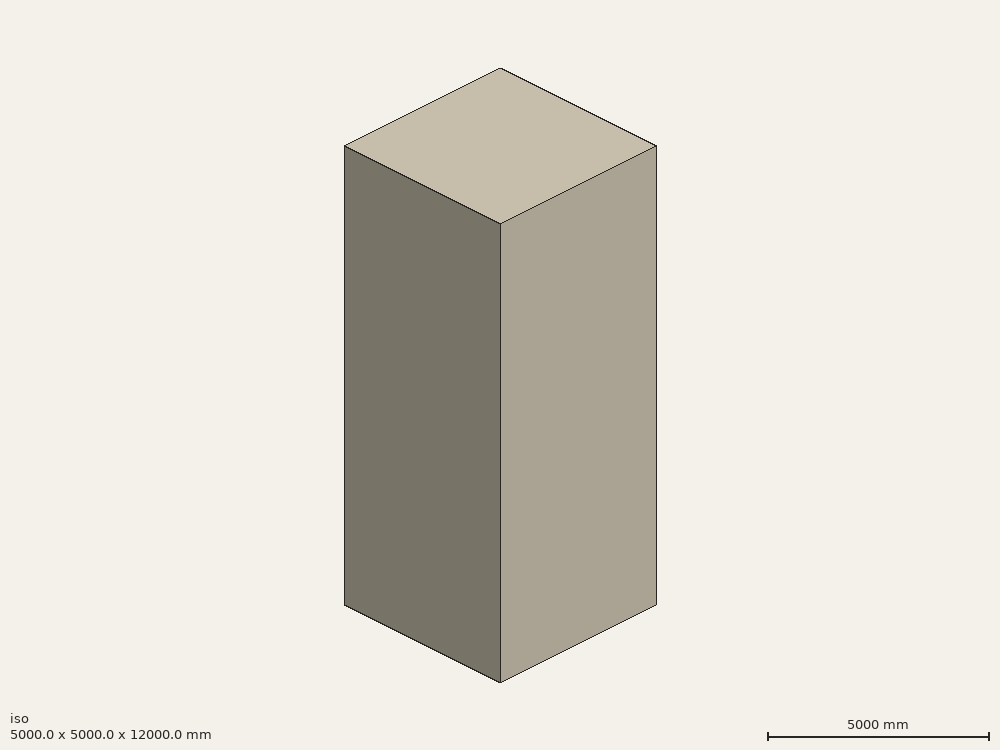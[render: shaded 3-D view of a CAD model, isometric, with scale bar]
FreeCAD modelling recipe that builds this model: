
FCSTD DOCUMENT  (FreeCAD 0.21R33694 (Git))
Label: revolveTester-6
License: All rights reserved
LicenseURL: http://en.wikipedia.org/wiki/All_rights_reserved
objects: App::DocumentObjectGroupPython×1248, App::Part×2, Part::FeaturePython×1, Sketcher::SketchObject×1, Part::Revolution×1, Part::Cylinder×1, Part::Cut×1
note: 5 computed .brp shape members not serialized (recipe doc carries the construction recipe); baked Part::Feature solids carry a one-line shape summary decoded from their .brp

FEATURE [App::DocumentObjectGroupPython] HALFPI  # scripted group (container) (typed FeaturePython)
  name = HALFPI
  value = pi/2.
FEATURE [App::DocumentObjectGroupPython] PI  # scripted group (container) (typed FeaturePython)
  name = PI
  value = 1.*pi
FEATURE [App::DocumentObjectGroupPython] TWOPI  # scripted group (container) (typed FeaturePython)
  name = TWOPI
  value = 2.*pi
FEATURE [App::DocumentObjectGroupPython] Constants  # scripted group (container) (typed FeaturePython)
  Group = -> [HALFPI,PI,TWOPI]
FEATURE [App::DocumentObjectGroupPython] Variables  # scripted group (container) (typed FeaturePython)
FEATURE [App::DocumentObjectGroupPython] Quantities  # scripted group (container) (typed FeaturePython)
FEATURE [App::DocumentObjectGroupPython] Isotopes  # scripted group (container) (typed FeaturePython)
FEATURE [App::DocumentObjectGroupPython] Elements  # scripted group (container) (typed FeaturePython)
FEATURE [App::DocumentObjectGroupPython] G4Isotopes  # scripted group (container) (typed FeaturePython)
FEATURE [App::DocumentObjectGroupPython] H_element  # scripted group (container) (typed FeaturePython)
  Z = 1
  atom_value = 1.008
  formula = H
  name = H_element
FEATURE [App::DocumentObjectGroupPython] He_element  # scripted group (container) (typed FeaturePython)
  Z = 2
  atom_value = 4.0026
  formula = He
  name = He_element
FEATURE [App::DocumentObjectGroupPython] Li_element  # scripted group (container) (typed FeaturePython)
  Z = 3
  atom_value = 6.94
  formula = Li
  name = Li_element
FEATURE [App::DocumentObjectGroupPython] Be_element  # scripted group (container) (typed FeaturePython)
  Z = 4
  atom_value = 9.01218
  formula = Be
  name = Be_element
FEATURE [App::DocumentObjectGroupPython] B_element  # scripted group (container) (typed FeaturePython)
  Z = 5
  atom_value = 10.81
  formula = B
  name = B_element
FEATURE [App::DocumentObjectGroupPython] C_element  # scripted group (container) (typed FeaturePython)
  Z = 6
  atom_value = 12.011
  formula = C
  name = C_element
FEATURE [App::DocumentObjectGroupPython] N_element  # scripted group (container) (typed FeaturePython)
  Z = 7
  atom_value = 14.007
  formula = N
  name = N_element
FEATURE [App::DocumentObjectGroupPython] O_element  # scripted group (container) (typed FeaturePython)
  Z = 8
  atom_value = 15.999
  formula = O
  name = O_element
FEATURE [App::DocumentObjectGroupPython] F_element  # scripted group (container) (typed FeaturePython)
  Z = 9
  atom_value = 18.9984
  formula = F
  name = F_element
FEATURE [App::DocumentObjectGroupPython] Ne_element  # scripted group (container) (typed FeaturePython)
  Z = 10
  atom_value = 20.1797
  formula = Ne
  name = Ne_element
FEATURE [App::DocumentObjectGroupPython] Na_element  # scripted group (container) (typed FeaturePython)
  Z = 11
  atom_value = 22.9898
  formula = Na
  name = Na_element
FEATURE [App::DocumentObjectGroupPython] Mg_element  # scripted group (container) (typed FeaturePython)
  Z = 12
  atom_value = 24.305
  formula = Mg
  name = Mg_element
FEATURE [App::DocumentObjectGroupPython] Al_element  # scripted group (container) (typed FeaturePython)
  Z = 13
  atom_value = 26.9815
  formula = Al
  name = Al_element
FEATURE [App::DocumentObjectGroupPython] Si_element  # scripted group (container) (typed FeaturePython)
  Z = 14
  atom_value = 28.085
  formula = Si
  name = Si_element
FEATURE [App::DocumentObjectGroupPython] P_element  # scripted group (container) (typed FeaturePython)
  Z = 15
  atom_value = 30.9738
  formula = P
  name = P_element
FEATURE [App::DocumentObjectGroupPython] S_element  # scripted group (container) (typed FeaturePython)
  Z = 16
  atom_value = 32.06
  formula = S
  name = S_element
FEATURE [App::DocumentObjectGroupPython] Cl_element  # scripted group (container) (typed FeaturePython)
  Z = 17
  atom_value = 35.45
  formula = Cl
  name = Cl_element
FEATURE [App::DocumentObjectGroupPython] Ar_element  # scripted group (container) (typed FeaturePython)
  Z = 18
  atom_value = 39.95
  formula = Ar
  name = Ar_element
FEATURE [App::DocumentObjectGroupPython] K_element  # scripted group (container) (typed FeaturePython)
  Z = 19
  atom_value = 39.0983
  formula = K
  name = K_element
FEATURE [App::DocumentObjectGroupPython] Ca_element  # scripted group (container) (typed FeaturePython)
  Z = 20
  atom_value = 40.078
  formula = Ca
  name = Ca_element
FEATURE [App::DocumentObjectGroupPython] Sc_element  # scripted group (container) (typed FeaturePython)
  Z = 21
  atom_value = 44.9559
  formula = Sc
  name = Sc_element
FEATURE [App::DocumentObjectGroupPython] Ti_element  # scripted group (container) (typed FeaturePython)
  Z = 22
  atom_value = 47.867
  formula = Ti
  name = Ti_element
FEATURE [App::DocumentObjectGroupPython] V_element  # scripted group (container) (typed FeaturePython)
  Z = 23
  atom_value = 50.9415
  formula = V
  name = V_element
FEATURE [App::DocumentObjectGroupPython] Cr_element  # scripted group (container) (typed FeaturePython)
  Z = 24
  atom_value = 51.9961
  formula = Cr
  name = Cr_element
FEATURE [App::DocumentObjectGroupPython] Mn_element  # scripted group (container) (typed FeaturePython)
  Z = 25
  atom_value = 54.938
  formula = Mn
  name = Mn_element
FEATURE [App::DocumentObjectGroupPython] Fe_element  # scripted group (container) (typed FeaturePython)
  Z = 26
  atom_value = 55.845
  formula = Fe
  name = Fe_element
FEATURE [App::DocumentObjectGroupPython] Co_element  # scripted group (container) (typed FeaturePython)
  Z = 27
  atom_value = 58.9332
  formula = Co
  name = Co_element
FEATURE [App::DocumentObjectGroupPython] Ni_element  # scripted group (container) (typed FeaturePython)
  Z = 28
  atom_value = 58.6934
  formula = Ni
  name = Ni_element
FEATURE [App::DocumentObjectGroupPython] Cu_element  # scripted group (container) (typed FeaturePython)
  Z = 29
  atom_value = 63.546
  formula = Cu
  name = Cu_element
FEATURE [App::DocumentObjectGroupPython] Zn_element  # scripted group (container) (typed FeaturePython)
  Z = 30
  atom_value = 65.38
  formula = Zn
  name = Zn_element
FEATURE [App::DocumentObjectGroupPython] Ga_element  # scripted group (container) (typed FeaturePython)
  Z = 31
  atom_value = 69.723
  formula = Ga
  name = Ga_element
FEATURE [App::DocumentObjectGroupPython] Ge_element  # scripted group (container) (typed FeaturePython)
  Z = 32
  atom_value = 72.63
  formula = Ge
  name = Ge_element
FEATURE [App::DocumentObjectGroupPython] As_element  # scripted group (container) (typed FeaturePython)
  Z = 33
  atom_value = 74.9216
  formula = As
  name = As_element
FEATURE [App::DocumentObjectGroupPython] Se_element  # scripted group (container) (typed FeaturePython)
  Z = 34
  atom_value = 78.971
  formula = Se
  name = Se_element
FEATURE [App::DocumentObjectGroupPython] Br_element  # scripted group (container) (typed FeaturePython)
  Z = 35
  atom_value = 79.904
  formula = Br
  name = Br_element
FEATURE [App::DocumentObjectGroupPython] Kr_element  # scripted group (container) (typed FeaturePython)
  Z = 36
  atom_value = 83.798
  formula = Kr
  name = Kr_element
FEATURE [App::DocumentObjectGroupPython] Rb_element  # scripted group (container) (typed FeaturePython)
  Z = 37
  atom_value = 85.4678
  formula = Rb
  name = Rb_element
FEATURE [App::DocumentObjectGroupPython] Sr_element  # scripted group (container) (typed FeaturePython)
  Z = 38
  atom_value = 87.62
  formula = Sr
  name = Sr_element
FEATURE [App::DocumentObjectGroupPython] Y_element  # scripted group (container) (typed FeaturePython)
  Z = 39
  atom_value = 88.9058
  formula = Y
  name = Y_element
FEATURE [App::DocumentObjectGroupPython] Zr_element  # scripted group (container) (typed FeaturePython)
  Z = 40
  atom_value = 91.224
  formula = Zr
  name = Zr_element
FEATURE [App::DocumentObjectGroupPython] Nb_element  # scripted group (container) (typed FeaturePython)
  Z = 41
  atom_value = 92.9064
  formula = Nb
  name = Nb_element
FEATURE [App::DocumentObjectGroupPython] Mo_element  # scripted group (container) (typed FeaturePython)
  Z = 42
  atom_value = 95.95
  formula = Mo
  name = Mo_element
FEATURE [App::DocumentObjectGroupPython] Tc_element  # scripted group (container) (typed FeaturePython)
  Z = 43
  atom_value = 97
  formula = Tc
  name = Tc_element
FEATURE [App::DocumentObjectGroupPython] Ru_element  # scripted group (container) (typed FeaturePython)
  Z = 44
  atom_value = 101.07
  formula = Ru
  name = Ru_element
FEATURE [App::DocumentObjectGroupPython] Rh_element  # scripted group (container) (typed FeaturePython)
  Z = 45
  atom_value = 102.905
  formula = Rh
  name = Rh_element
FEATURE [App::DocumentObjectGroupPython] Pd_element  # scripted group (container) (typed FeaturePython)
  Z = 46
  atom_value = 106.42
  formula = Pd
  name = Pd_element
FEATURE [App::DocumentObjectGroupPython] Ag_element  # scripted group (container) (typed FeaturePython)
  Z = 47
  atom_value = 107.868
  formula = Ag
  name = Ag_element
FEATURE [App::DocumentObjectGroupPython] Cd_element  # scripted group (container) (typed FeaturePython)
  Z = 48
  atom_value = 112.414
  formula = Cd
  name = Cd_element
FEATURE [App::DocumentObjectGroupPython] In_element  # scripted group (container) (typed FeaturePython)
  Z = 49
  atom_value = 114.818
  formula = In
  name = In_element
FEATURE [App::DocumentObjectGroupPython] Sn_element  # scripted group (container) (typed FeaturePython)
  Z = 50
  atom_value = 118.71
  formula = Sn
  name = Sn_element
FEATURE [App::DocumentObjectGroupPython] Sb_element  # scripted group (container) (typed FeaturePython)
  Z = 51
  atom_value = 121.76
  formula = Sb
  name = Sb_element
FEATURE [App::DocumentObjectGroupPython] Te_element  # scripted group (container) (typed FeaturePython)
  Z = 52
  atom_value = 127.6
  formula = Te
  name = Te_element
FEATURE [App::DocumentObjectGroupPython] I_element  # scripted group (container) (typed FeaturePython)
  Z = 53
  atom_value = 126.904
  formula = I
  name = I_element
FEATURE [App::DocumentObjectGroupPython] Xe_element  # scripted group (container) (typed FeaturePython)
  Z = 54
  atom_value = 131.293
  formula = Xe
  name = Xe_element
FEATURE [App::DocumentObjectGroupPython] Cs_element  # scripted group (container) (typed FeaturePython)
  Z = 55
  atom_value = 132.905
  formula = Cs
  name = Cs_element
FEATURE [App::DocumentObjectGroupPython] Ba_element  # scripted group (container) (typed FeaturePython)
  Z = 56
  atom_value = 137.327
  formula = Ba
  name = Ba_element
FEATURE [App::DocumentObjectGroupPython] La_element  # scripted group (container) (typed FeaturePython)
  Z = 57
  atom_value = 138.905
  formula = La
  name = La_element
FEATURE [App::DocumentObjectGroupPython] Ce_element  # scripted group (container) (typed FeaturePython)
  Z = 58
  atom_value = 140.116
  formula = Ce
  name = Ce_element
FEATURE [App::DocumentObjectGroupPython] Pr_element  # scripted group (container) (typed FeaturePython)
  Z = 59
  atom_value = 140.908
  formula = Pr
  name = Pr_element
FEATURE [App::DocumentObjectGroupPython] Nd_element  # scripted group (container) (typed FeaturePython)
  Z = 60
  atom_value = 144.242
  formula = Nd
  name = Nd_element
FEATURE [App::DocumentObjectGroupPython] Pm_element  # scripted group (container) (typed FeaturePython)
  Z = 61
  atom_value = 145
  formula = Pm
  name = Pm_element
FEATURE [App::DocumentObjectGroupPython] Sm_element  # scripted group (container) (typed FeaturePython)
  Z = 62
  atom_value = 150.36
  formula = Sm
  name = Sm_element
FEATURE [App::DocumentObjectGroupPython] Eu_element  # scripted group (container) (typed FeaturePython)
  Z = 63
  atom_value = 151.964
  formula = Eu
  name = Eu_element
FEATURE [App::DocumentObjectGroupPython] Gd_element  # scripted group (container) (typed FeaturePython)
  Z = 64
  atom_value = 157.25
  formula = Gd
  name = Gd_element
FEATURE [App::DocumentObjectGroupPython] Tb_element  # scripted group (container) (typed FeaturePython)
  Z = 65
  atom_value = 158.925
  formula = Tb
  name = Tb_element
FEATURE [App::DocumentObjectGroupPython] Dy_element  # scripted group (container) (typed FeaturePython)
  Z = 66
  atom_value = 162.5
  formula = Dy
  name = Dy_element
FEATURE [App::DocumentObjectGroupPython] Ho_element  # scripted group (container) (typed FeaturePython)
  Z = 67
  atom_value = 164.93
  formula = Ho
  name = Ho_element
FEATURE [App::DocumentObjectGroupPython] Er_element  # scripted group (container) (typed FeaturePython)
  Z = 68
  atom_value = 167.259
  formula = Er
  name = Er_element
FEATURE [App::DocumentObjectGroupPython] Tm_element  # scripted group (container) (typed FeaturePython)
  Z = 69
  atom_value = 168.934
  formula = Tm
  name = Tm_element
FEATURE [App::DocumentObjectGroupPython] Yb_element  # scripted group (container) (typed FeaturePython)
  Z = 70
  atom_value = 173.045
  formula = Yb
  name = Yb_element
FEATURE [App::DocumentObjectGroupPython] Lu_element  # scripted group (container) (typed FeaturePython)
  Z = 71
  atom_value = 174.967
  formula = Lu
  name = Lu_element
FEATURE [App::DocumentObjectGroupPython] Hf_element  # scripted group (container) (typed FeaturePython)
  Z = 72
  atom_value = 178.49
  formula = Hf
  name = Hf_element
FEATURE [App::DocumentObjectGroupPython] Ta_element  # scripted group (container) (typed FeaturePython)
  Z = 73
  atom_value = 180.948
  formula = Ta
  name = Ta_element
FEATURE [App::DocumentObjectGroupPython] W_element  # scripted group (container) (typed FeaturePython)
  Z = 74
  atom_value = 183.84
  formula = W
  name = W_element
FEATURE [App::DocumentObjectGroupPython] Re_element  # scripted group (container) (typed FeaturePython)
  Z = 75
  atom_value = 186.207
  formula = Re
  name = Re_element
FEATURE [App::DocumentObjectGroupPython] Os_element  # scripted group (container) (typed FeaturePython)
  Z = 76
  atom_value = 190.23
  formula = Os
  name = Os_element
FEATURE [App::DocumentObjectGroupPython] Ir_element  # scripted group (container) (typed FeaturePython)
  Z = 77
  atom_value = 192.217
  formula = Ir
  name = Ir_element
FEATURE [App::DocumentObjectGroupPython] Pt_element  # scripted group (container) (typed FeaturePython)
  Z = 78
  atom_value = 195.084
  formula = Pt
  name = Pt_element
FEATURE [App::DocumentObjectGroupPython] Au_element  # scripted group (container) (typed FeaturePython)
  Z = 79
  atom_value = 196.967
  formula = Au
  name = Au_element
FEATURE [App::DocumentObjectGroupPython] Hg_element  # scripted group (container) (typed FeaturePython)
  Z = 80
  atom_value = 200.592
  formula = Hg
  name = Hg_element
FEATURE [App::DocumentObjectGroupPython] Tl_element  # scripted group (container) (typed FeaturePython)
  Z = 81
  atom_value = 204.38
  formula = Tl
  name = Tl_element
FEATURE [App::DocumentObjectGroupPython] Pb_element  # scripted group (container) (typed FeaturePython)
  Z = 82
  atom_value = 207.2
  formula = Pb
  name = Pb_element
FEATURE [App::DocumentObjectGroupPython] Bi_element  # scripted group (container) (typed FeaturePython)
  Z = 83
  atom_value = 208.98
  formula = Bi
  name = Bi_element
FEATURE [App::DocumentObjectGroupPython] Po_element  # scripted group (container) (typed FeaturePython)
  Z = 84
  atom_value = 209
  formula = Po
  name = Po_element
FEATURE [App::DocumentObjectGroupPython] At_element  # scripted group (container) (typed FeaturePython)
  Z = 85
  atom_value = 210
  formula = At
  name = At_element
FEATURE [App::DocumentObjectGroupPython] Rn_element  # scripted group (container) (typed FeaturePython)
  Z = 86
  atom_value = 222
  formula = Rn
  name = Rn_element
FEATURE [App::DocumentObjectGroupPython] Fr_element  # scripted group (container) (typed FeaturePython)
  Z = 87
  atom_value = 223
  formula = Fr
  name = Fr_element
FEATURE [App::DocumentObjectGroupPython] Ra_element  # scripted group (container) (typed FeaturePython)
  Z = 88
  atom_value = 226
  formula = Ra
  name = Ra_element
FEATURE [App::DocumentObjectGroupPython] Ac_element  # scripted group (container) (typed FeaturePython)
  Z = 89
  atom_value = 227
  formula = Ac
  name = Ac_element
FEATURE [App::DocumentObjectGroupPython] Th_element  # scripted group (container) (typed FeaturePython)
  Z = 90
  atom_value = 232.038
  formula = Th
  name = Th_element
FEATURE [App::DocumentObjectGroupPython] Pa_element  # scripted group (container) (typed FeaturePython)
  Z = 91
  atom_value = 231.036
  formula = Pa
  name = Pa_element
FEATURE [App::DocumentObjectGroupPython] U_element  # scripted group (container) (typed FeaturePython)
  Z = 92
  atom_value = 238.029
  formula = U
  name = U_element
FEATURE [App::DocumentObjectGroupPython] Np_element  # scripted group (container) (typed FeaturePython)
  Z = 93
  atom_value = 237
  formula = Np
  name = Np_element
FEATURE [App::DocumentObjectGroupPython] Pu_element  # scripted group (container) (typed FeaturePython)
  Z = 94
  atom_value = 244
  formula = Pu
  name = Pu_element
FEATURE [App::DocumentObjectGroupPython] Am_element  # scripted group (container) (typed FeaturePython)
  Z = 95
  atom_value = 243
  formula = Am
  name = Am_element
FEATURE [App::DocumentObjectGroupPython] Cm_element  # scripted group (container) (typed FeaturePython)
  Z = 96
  atom_value = 247
  formula = Cm
  name = Cm_element
FEATURE [App::DocumentObjectGroupPython] Bk_element  # scripted group (container) (typed FeaturePython)
  Z = 97
  atom_value = 247
  formula = Bk
  name = Bk_element
FEATURE [App::DocumentObjectGroupPython] Cf_element  # scripted group (container) (typed FeaturePython)
  Z = 98
  atom_value = 251
  formula = Cf
  name = Cf_element
FEATURE [App::DocumentObjectGroupPython] G4Elements  # scripted group (container) (typed FeaturePython)
  Group = -> [H_element,He_element,Li_element,Be_element,B_element,C_element,N_element,O_element,F_element,Ne_element,Na_element,Mg_element,Al_element,Si_element,P_element,S_element,Cl_element,Ar_element,K_element,Ca_element,Sc_element,Ti_element,V_element,Cr_element,Mn_element,Fe_element,Co_element,Ni_element,Cu_element,Zn_element,Ga_element,Ge_element,As_element,Se_element,Br_element,Kr_element,Rb_element,+61 more]
FEATURE [App::DocumentObjectGroupPython] H_element001  label="H_element : 0.101"  # scripted group (container) (typed FeaturePython)
  n = 0.101327
FEATURE [App::DocumentObjectGroupPython] C_element001  label="C_element : 0.775"  # scripted group (container) (typed FeaturePython)
  n = 0.7755
FEATURE [App::DocumentObjectGroupPython] N_element001  label="N_element : 0.035"  # scripted group (container) (typed FeaturePython)
  n = 0.035057
FEATURE [App::DocumentObjectGroupPython] O_element001  label="O_element : 0.052"  # scripted group (container) (typed FeaturePython)
  n = 0.0523159
FEATURE [App::DocumentObjectGroupPython] F_element001  label="F_element : 0.017"  # scripted group (container) (typed FeaturePython)
  n = 0.017422
FEATURE [App::DocumentObjectGroupPython] Ca_element001  label="Ca_element : 0.018"  # scripted group (container) (typed FeaturePython)
  n = 0.018378
FEATURE [App::DocumentObjectGroupPython] G4_A_150_TISSUE  label="G4_A-150_TISSUE"  # scripted group (container) (typed FeaturePython)
  Dunit = g/cm3
  Dvalue = 1.127
  Group = -> [H_element001,C_element001,N_element001,O_element001,F_element001,Ca_element001]
  conduct = 2
  density = 1
  expand = 3
  formula = G4_A-150_TISSUE
  name = G4_A-150_TISSUE
  specific = 4
FEATURE [App::DocumentObjectGroupPython] C_element002  label="C_element : 3"  # scripted group (container) (typed FeaturePython)
  n = 3
  ref = C_element
FEATURE [App::DocumentObjectGroupPython] H_element002  label="H_element : 6"  # scripted group (container) (typed FeaturePython)
  n = 6
  ref = H_element
FEATURE [App::DocumentObjectGroupPython] O_element002  label="O_element : 1"  # scripted group (container) (typed FeaturePython)
  n = 1
  ref = O_element
FEATURE [App::DocumentObjectGroupPython] G4_ACETONE  # scripted group (container) (typed FeaturePython)
  Dunit = g/cm3
  Dvalue = 0.7899
  Group = -> [C_element002,H_element002,O_element002]
  conduct = 2
  density = 1
  expand = 3
  formula = G4_ACETONE
  name = G4_ACETONE
  specific = 4
FEATURE [App::DocumentObjectGroupPython] C_element003  label="C_element : 2"  # scripted group (container) (typed FeaturePython)
  n = 2
  ref = C_element
FEATURE [App::DocumentObjectGroupPython] H_element003  label="H_element : 2"  # scripted group (container) (typed FeaturePython)
  n = 2
  ref = H_element
FEATURE [App::DocumentObjectGroupPython] G4_ACETYLENE  # scripted group (container) (typed FeaturePython)
  Dunit = g/cm3
  Dvalue = 0.0010967
  Group = -> [C_element003,H_element003]
  conduct = 2
  density = 1
  expand = 3
  formula = G4_ACETYLENE
  name = G4_ACETYLENE
  specific = 4
FEATURE [App::DocumentObjectGroupPython] C_element004  label="C_element : 5"  # scripted group (container) (typed FeaturePython)
  n = 5
  ref = C_element
FEATURE [App::DocumentObjectGroupPython] H_element004  label="H_element : 5"  # scripted group (container) (typed FeaturePython)
  n = 5
  ref = H_element
FEATURE [App::DocumentObjectGroupPython] N_element002  label="N_element : 5"  # scripted group (container) (typed FeaturePython)
  n = 5
  ref = N_element
FEATURE [App::DocumentObjectGroupPython] G4_ADENINE  # scripted group (container) (typed FeaturePython)
  Dunit = g/cm3
  Dvalue = 1.6
  Group = -> [C_element004,H_element004,N_element002]
  conduct = 2
  density = 1
  expand = 3
  formula = G4_ADENINE
  name = G4_ADENINE
  specific = 4
FEATURE [App::DocumentObjectGroupPython] H_element005  label="H_element : 0.114"  # scripted group (container) (typed FeaturePython)
  n = 0.114
FEATURE [App::DocumentObjectGroupPython] C_element005  label="C_element : 0.598"  # scripted group (container) (typed FeaturePython)
  n = 0.598
FEATURE [App::DocumentObjectGroupPython] N_element003  label="N_element : 0.007"  # scripted group (container) (typed FeaturePython)
  n = 0.007
FEATURE [App::DocumentObjectGroupPython] O_element003  label="O_element : 0.278"  # scripted group (container) (typed FeaturePython)
  n = 0.278
FEATURE [App::DocumentObjectGroupPython] Na_element001  label="Na_element : 0.001"  # scripted group (container) (typed FeaturePython)
  n = 0.001
FEATURE [App::DocumentObjectGroupPython] S_element001  label="S_element : 0.001"  # scripted group (container) (typed FeaturePython)
  n = 0.001
FEATURE [App::DocumentObjectGroupPython] Cl_element001  label="Cl_element : 0.001"  # scripted group (container) (typed FeaturePython)
  n = 0.001
FEATURE [App::DocumentObjectGroupPython] G4_ADIPOSE_TISSUE_ICRP  # scripted group (container) (typed FeaturePython)
  Dunit = g/cm3
  Dvalue = 0.95
  Group = -> [H_element005,C_element005,N_element003,O_element003,Na_element001,S_element001,Cl_element001]
  conduct = 2
  density = 1
  expand = 3
  formula = G4_ADIPOSE_TISSUE_ICRP
  name = G4_ADIPOSE_TISSUE_ICRP
  specific = 4
FEATURE [App::DocumentObjectGroupPython] C_element006  label="C_element : 0.000"  # scripted group (container) (typed FeaturePython)
  n = 0.000124
FEATURE [App::DocumentObjectGroupPython] N_element004  label="N_element : 0.755"  # scripted group (container) (typed FeaturePython)
  n = 0.755268
FEATURE [App::DocumentObjectGroupPython] O_element004  label="O_element : 0.232"  # scripted group (container) (typed FeaturePython)
  n = 0.231781
FEATURE [App::DocumentObjectGroupPython] Ar_element001  label="Ar_element : 0.013"  # scripted group (container) (typed FeaturePython)
  n = 0.012827
FEATURE [App::DocumentObjectGroupPython] G4_AIR  # scripted group (container) (typed FeaturePython)
  Dunit = g/cm3
  Dvalue = 0.00120479
  Group = -> [C_element006,N_element004,O_element004,Ar_element001]
  conduct = 2
  density = 1
  expand = 3
  formula = G4_AIR
  name = G4_AIR
  specific = 4
FEATURE [App::DocumentObjectGroupPython] C_element007  label="C_element : 006"  # scripted group (container) (typed FeaturePython)
  n = 3
  ref = C_element
FEATURE [App::DocumentObjectGroupPython] H_element006  label="H_element : 7"  # scripted group (container) (typed FeaturePython)
  n = 7
  ref = H_element
FEATURE [App::DocumentObjectGroupPython] N_element005  label="N_element : 1"  # scripted group (container) (typed FeaturePython)
  n = 1
  ref = N_element
FEATURE [App::DocumentObjectGroupPython] O_element005  label="O_element : 2"  # scripted group (container) (typed FeaturePython)
  n = 2
  ref = O_element
FEATURE [App::DocumentObjectGroupPython] G4_ALANINE  # scripted group (container) (typed FeaturePython)
  Dunit = g/cm3
  Dvalue = 1.42
  Group = -> [C_element007,H_element006,N_element005,O_element005]
  conduct = 2
  density = 1
  expand = 3
  formula = G4_ALANINE
  name = G4_ALANINE
  specific = 4
FEATURE [App::DocumentObjectGroupPython] Al_element001  label="Al_element : 2"  # scripted group (container) (typed FeaturePython)
  n = 2
  ref = Al_element
FEATURE [App::DocumentObjectGroupPython] O_element006  label="O_element : 3"  # scripted group (container) (typed FeaturePython)
  n = 3
  ref = O_element
FEATURE [App::DocumentObjectGroupPython] G4_ALUMINUM_OXIDE  # scripted group (container) (typed FeaturePython)
  Dunit = g/cm3
  Dvalue = 3.97
  Group = -> [Al_element001,O_element006]
  conduct = 2
  density = 1
  expand = 3
  formula = G4_ALUMINUM_OXIDE
  name = G4_ALUMINUM_OXIDE
  specific = 4
FEATURE [App::DocumentObjectGroupPython] H_element007  label="H_element : 0.106"  # scripted group (container) (typed FeaturePython)
  n = 0.10593
FEATURE [App::DocumentObjectGroupPython] C_element008  label="C_element : 0.789"  # scripted group (container) (typed FeaturePython)
  n = 0.788974
FEATURE [App::DocumentObjectGroupPython] O_element007  label="O_element : 0.105"  # scripted group (container) (typed FeaturePython)
  n = 0.105096
FEATURE [App::DocumentObjectGroupPython] G4_AMBER  # scripted group (container) (typed FeaturePython)
  Dunit = g/cm3
  Dvalue = 1.1
  Group = -> [H_element007,C_element008,O_element007]
  conduct = 2
  density = 1
  expand = 3
  formula = G4_AMBER
  name = G4_AMBER
  specific = 4
FEATURE [App::DocumentObjectGroupPython] N_element006  label="N_element : 006"  # scripted group (container) (typed FeaturePython)
  n = 1
  ref = N_element
FEATURE [App::DocumentObjectGroupPython] H_element008  label="H_element : 3"  # scripted group (container) (typed FeaturePython)
  n = 3
  ref = H_element
FEATURE [App::DocumentObjectGroupPython] G4_AMMONIA  # scripted group (container) (typed FeaturePython)
  Dunit = g/cm3
  Dvalue = 0.000826019
  Group = -> [N_element006,H_element008]
  conduct = 2
  density = 1
  expand = 3
  formula = G4_AMMONIA
  name = G4_AMMONIA
  specific = 4
FEATURE [App::DocumentObjectGroupPython] C_element009  label="C_element : 6"  # scripted group (container) (typed FeaturePython)
  n = 6
  ref = C_element
FEATURE [App::DocumentObjectGroupPython] H_element009  label="H_element : 008"  # scripted group (container) (typed FeaturePython)
  n = 7
  ref = H_element
FEATURE [App::DocumentObjectGroupPython] N_element007  label="N_element : 007"  # scripted group (container) (typed FeaturePython)
  n = 1
  ref = N_element
FEATURE [App::DocumentObjectGroupPython] G4_ANILINE  # scripted group (container) (typed FeaturePython)
  Dunit = g/cm3
  Dvalue = 1.0235
  Group = -> [C_element009,H_element009,N_element007]
  conduct = 2
  density = 1
  expand = 3
  formula = G4_ANILINE
  name = G4_ANILINE
  specific = 4
FEATURE [App::DocumentObjectGroupPython] C_element010  label="C_element : 14"  # scripted group (container) (typed FeaturePython)
  n = 14
  ref = C_element
FEATURE [App::DocumentObjectGroupPython] H_element010  label="H_element : 10"  # scripted group (container) (typed FeaturePython)
  n = 10
  ref = H_element
FEATURE [App::DocumentObjectGroupPython] G4_ANTHRACENE  # scripted group (container) (typed FeaturePython)
  Dunit = g/cm3
  Dvalue = 1.283
  Group = -> [C_element010,H_element010]
  conduct = 2
  density = 1
  expand = 3
  formula = G4_ANTHRACENE
  name = G4_ANTHRACENE
  specific = 4
FEATURE [App::DocumentObjectGroupPython] H_element011  label="H_element : 0.065"  # scripted group (container) (typed FeaturePython)
  n = 0.0654709
FEATURE [App::DocumentObjectGroupPython] C_element011  label="C_element : 0.537"  # scripted group (container) (typed FeaturePython)
  n = 0.536944
FEATURE [App::DocumentObjectGroupPython] N_element008  label="N_element : 0.021"  # scripted group (container) (typed FeaturePython)
  n = 0.0215
FEATURE [App::DocumentObjectGroupPython] O_element008  label="O_element : 0.032"  # scripted group (container) (typed FeaturePython)
  n = 0.032085
FEATURE [App::DocumentObjectGroupPython] F_element002  label="F_element : 0.167"  # scripted group (container) (typed FeaturePython)
  n = 0.167411
FEATURE [App::DocumentObjectGroupPython] Ca_element002  label="Ca_element : 0.177"  # scripted group (container) (typed FeaturePython)
  n = 0.176589
FEATURE [App::DocumentObjectGroupPython] G4_B_100_BONE  label="G4_B-100_BONE"  # scripted group (container) (typed FeaturePython)
  Dunit = g/cm3
  Dvalue = 1.45
  Group = -> [H_element011,C_element011,N_element008,O_element008,F_element002,Ca_element002]
  conduct = 2
  density = 1
  expand = 3
  formula = G4_B-100_BONE
  name = G4_B-100_BONE
  specific = 4
FEATURE [App::DocumentObjectGroupPython] H_element012  label="H_element : 0.057"  # scripted group (container) (typed FeaturePython)
  n = 0.057441
FEATURE [App::DocumentObjectGroupPython] C_element012  label="C_element : 0.790"  # scripted group (container) (typed FeaturePython)
  n = 0.774591
FEATURE [App::DocumentObjectGroupPython] O_element009  label="O_element : 0.168"  # scripted group (container) (typed FeaturePython)
  n = 0.167968
FEATURE [App::DocumentObjectGroupPython] G4_BAKELITE  # scripted group (container) (typed FeaturePython)
  Dunit = g/cm3
  Dvalue = 1.25
  Group = -> [H_element012,C_element012,O_element009]
  conduct = 2
  density = 1
  expand = 3
  formula = G4_BAKELITE
  name = G4_BAKELITE
  specific = 4
FEATURE [App::DocumentObjectGroupPython] Ba_element001  label="Ba_element : 1"  # scripted group (container) (typed FeaturePython)
  n = 1
  ref = Ba_element
FEATURE [App::DocumentObjectGroupPython] F_element003  label="F_element : 2"  # scripted group (container) (typed FeaturePython)
  n = 2
  ref = F_element
FEATURE [App::DocumentObjectGroupPython] G4_BARIUM_FLUORIDE  # scripted group (container) (typed FeaturePython)
  Dunit = g/cm3
  Dvalue = 4.89
  Group = -> [Ba_element001,F_element003]
  conduct = 2
  density = 1
  expand = 3
  formula = G4_BARIUM_FLUORIDE
  name = G4_BARIUM_FLUORIDE
  specific = 4
FEATURE [App::DocumentObjectGroupPython] Ba_element002  label="Ba_element : 002"  # scripted group (container) (typed FeaturePython)
  n = 1
  ref = Ba_element
FEATURE [App::DocumentObjectGroupPython] S_element002  label="S_element : 1"  # scripted group (container) (typed FeaturePython)
  n = 1
  ref = S_element
FEATURE [App::DocumentObjectGroupPython] O_element010  label="O_element : 4"  # scripted group (container) (typed FeaturePython)
  n = 4
  ref = O_element
FEATURE [App::DocumentObjectGroupPython] G4_BARIUM_SULFATE  # scripted group (container) (typed FeaturePython)
  Dunit = g/cm3
  Dvalue = 4.5
  Group = -> [Ba_element002,S_element002,O_element010]
  conduct = 2
  density = 1
  expand = 3
  formula = G4_BARIUM_SULFATE
  name = G4_BARIUM_SULFATE
  specific = 4
FEATURE [App::DocumentObjectGroupPython] C_element013  label="C_element : 007"  # scripted group (container) (typed FeaturePython)
  n = 6
  ref = C_element
FEATURE [App::DocumentObjectGroupPython] H_element013  label="H_element : 009"  # scripted group (container) (typed FeaturePython)
  n = 6
  ref = H_element
FEATURE [App::DocumentObjectGroupPython] G4_BENZENE  # scripted group (container) (typed FeaturePython)
  Dunit = g/cm3
  Dvalue = 0.87865
  Group = -> [C_element013,H_element013]
  conduct = 2
  density = 1
  expand = 3
  formula = G4_BENZENE
  name = G4_BENZENE
  specific = 4
FEATURE [App::DocumentObjectGroupPython] Be_element001  label="Be_element : 1"  # scripted group (container) (typed FeaturePython)
  n = 1
  ref = Be_element
FEATURE [App::DocumentObjectGroupPython] O_element011  label="O_element : 005"  # scripted group (container) (typed FeaturePython)
  n = 1
  ref = O_element
FEATURE [App::DocumentObjectGroupPython] G4_BERYLLIUM_OXIDE  # scripted group (container) (typed FeaturePython)
  Dunit = g/cm3
  Dvalue = 3.01
  Group = -> [Be_element001,O_element011]
  conduct = 2
  density = 1
  expand = 3
  formula = G4_BERYLLIUM_OXIDE
  name = G4_BERYLLIUM_OXIDE
  specific = 4
FEATURE [App::DocumentObjectGroupPython] Bi_element001  label="Bi_element : 4"  # scripted group (container) (typed FeaturePython)
  n = 4
  ref = Bi_element
FEATURE [App::DocumentObjectGroupPython] Ge_element001  label="Ge_element : 3"  # scripted group (container) (typed FeaturePython)
  n = 3
  ref = Ge_element
FEATURE [App::DocumentObjectGroupPython] O_element012  label="O_element : 12"  # scripted group (container) (typed FeaturePython)
  n = 12
  ref = O_element
FEATURE [App::DocumentObjectGroupPython] G4_BGO  # scripted group (container) (typed FeaturePython)
  Dunit = g/cm3
  Dvalue = 7.13
  Group = -> [Bi_element001,Ge_element001,O_element012]
  conduct = 2
  density = 1
  expand = 3
  formula = G4_BGO
  name = G4_BGO
  specific = 4
FEATURE [App::DocumentObjectGroupPython] H_element014  label="H_element : 0.102"  # scripted group (container) (typed FeaturePython)
  n = 0.102
FEATURE [App::DocumentObjectGroupPython] C_element014  label="C_element : 0.110"  # scripted group (container) (typed FeaturePython)
  n = 0.11
FEATURE [App::DocumentObjectGroupPython] N_element009  label="N_element : 0.033"  # scripted group (container) (typed FeaturePython)
  n = 0.033
FEATURE [App::DocumentObjectGroupPython] O_element013  label="O_element : 0.745"  # scripted group (container) (typed FeaturePython)
  n = 0.745
FEATURE [App::DocumentObjectGroupPython] Na_element002  label="Na_element : 0.002"  # scripted group (container) (typed FeaturePython)
  n = 0.001
FEATURE [App::DocumentObjectGroupPython] P_element001  label="P_element : 0.001"  # scripted group (container) (typed FeaturePython)
  n = 0.001
FEATURE [App::DocumentObjectGroupPython] S_element003  label="S_element : 0.002"  # scripted group (container) (typed FeaturePython)
  n = 0.002
FEATURE [App::DocumentObjectGroupPython] Cl_element002  label="Cl_element : 0.003"  # scripted group (container) (typed FeaturePython)
  n = 0.003
FEATURE [App::DocumentObjectGroupPython] K_element001  label="K_element : 0.002"  # scripted group (container) (typed FeaturePython)
  n = 0.002
FEATURE [App::DocumentObjectGroupPython] Fe_element001  label="Fe_element : 0.001"  # scripted group (container) (typed FeaturePython)
  n = 0.001
FEATURE [App::DocumentObjectGroupPython] G4_BLOOD_ICRP  # scripted group (container) (typed FeaturePython)
  Dunit = g/cm3
  Dvalue = 1.06
  Group = -> [H_element014,C_element014,N_element009,O_element013,Na_element002,P_element001,S_element003,Cl_element002,K_element001,Fe_element001]
  conduct = 2
  density = 1
  expand = 3
  formula = G4_BLOOD_ICRP
  name = G4_BLOOD_ICRP
  specific = 4
FEATURE [App::DocumentObjectGroupPython] H_element015  label="H_element : 0.064"  # scripted group (container) (typed FeaturePython)
  n = 0.064
FEATURE [App::DocumentObjectGroupPython] C_element015  label="C_element : 0.278"  # scripted group (container) (typed FeaturePython)
  n = 0.278
FEATURE [App::DocumentObjectGroupPython] N_element010  label="N_element : 0.027"  # scripted group (container) (typed FeaturePython)
  n = 0.027
FEATURE [App::DocumentObjectGroupPython] O_element014  label="O_element : 0.410"  # scripted group (container) (typed FeaturePython)
  n = 0.41
FEATURE [App::DocumentObjectGroupPython] Mg_element001  label="Mg_element : 0.002"  # scripted group (container) (typed FeaturePython)
  n = 0.002
FEATURE [App::DocumentObjectGroupPython] P_element002  label="P_element : 0.070"  # scripted group (container) (typed FeaturePython)
  n = 0.07
FEATURE [App::DocumentObjectGroupPython] S_element004  label="S_element : 0.003"  # scripted group (container) (typed FeaturePython)
  n = 0.002
FEATURE [App::DocumentObjectGroupPython] Ca_element003  label="Ca_element : 0.147"  # scripted group (container) (typed FeaturePython)
  n = 0.147
FEATURE [App::DocumentObjectGroupPython] G4_BONE_COMPACT_ICRU  # scripted group (container) (typed FeaturePython)
  Dunit = g/cm3
  Dvalue = 1.85
  Group = -> [H_element015,C_element015,N_element010,O_element014,Mg_element001,P_element002,S_element004,Ca_element003]
  conduct = 2
  density = 1
  expand = 3
  formula = G4_BONE_COMPACT_ICRU
  name = G4_BONE_COMPACT_ICRU
  specific = 4
FEATURE [App::DocumentObjectGroupPython] H_element016  label="H_element : 0.034"  # scripted group (container) (typed FeaturePython)
  n = 0.034
FEATURE [App::DocumentObjectGroupPython] C_element016  label="C_element : 0.155"  # scripted group (container) (typed FeaturePython)
  n = 0.155
FEATURE [App::DocumentObjectGroupPython] N_element011  label="N_element : 0.042"  # scripted group (container) (typed FeaturePython)
  n = 0.042
FEATURE [App::DocumentObjectGroupPython] O_element015  label="O_element : 0.435"  # scripted group (container) (typed FeaturePython)
  n = 0.435
FEATURE [App::DocumentObjectGroupPython] Na_element003  label="Na_element : 0.003"  # scripted group (container) (typed FeaturePython)
  n = 0.001
FEATURE [App::DocumentObjectGroupPython] Mg_element002  label="Mg_element : 0.003"  # scripted group (container) (typed FeaturePython)
  n = 0.002
FEATURE [App::DocumentObjectGroupPython] P_element003  label="P_element : 0.103"  # scripted group (container) (typed FeaturePython)
  n = 0.103
FEATURE [App::DocumentObjectGroupPython] S_element005  label="S_element : 0.004"  # scripted group (container) (typed FeaturePython)
  n = 0.003
FEATURE [App::DocumentObjectGroupPython] Ca_element004  label="Ca_element : 0.225"  # scripted group (container) (typed FeaturePython)
  n = 0.225
FEATURE [App::DocumentObjectGroupPython] G4_BONE_CORTICAL_ICRP  # scripted group (container) (typed FeaturePython)
  Dunit = g/cm3
  Dvalue = 1.92
  Group = -> [H_element016,C_element016,N_element011,O_element015,Na_element003,Mg_element002,P_element003,S_element005,Ca_element004]
  conduct = 2
  density = 1
  expand = 3
  formula = G4_BONE_CORTICAL_ICRP
  name = G4_BONE_CORTICAL_ICRP
  specific = 4
FEATURE [App::DocumentObjectGroupPython] B_element001  label="B_element : 4"  # scripted group (container) (typed FeaturePython)
  n = 4
  ref = B_element
FEATURE [App::DocumentObjectGroupPython] C_element017  label="C_element : 1"  # scripted group (container) (typed FeaturePython)
  n = 1
  ref = C_element
FEATURE [App::DocumentObjectGroupPython] G4_BORON_CARBIDE  # scripted group (container) (typed FeaturePython)
  Dunit = g/cm3
  Dvalue = 2.52
  Group = -> [B_element001,C_element017]
  conduct = 2
  density = 1
  expand = 3
  formula = G4_BORON_CARBIDE
  name = G4_BORON_CARBIDE
  specific = 4
FEATURE [App::DocumentObjectGroupPython] B_element002  label="B_element : 2"  # scripted group (container) (typed FeaturePython)
  n = 2
  ref = B_element
FEATURE [App::DocumentObjectGroupPython] O_element016  label="O_element : 006"  # scripted group (container) (typed FeaturePython)
  n = 3
  ref = O_element
FEATURE [App::DocumentObjectGroupPython] G4_BORON_OXIDE  # scripted group (container) (typed FeaturePython)
  Dunit = g/cm3
  Dvalue = 1.812
  Group = -> [B_element002,O_element016]
  conduct = 2
  density = 1
  expand = 3
  formula = G4_BORON_OXIDE
  name = G4_BORON_OXIDE
  specific = 4
FEATURE [App::DocumentObjectGroupPython] H_element017  label="H_element : 0.107"  # scripted group (container) (typed FeaturePython)
  n = 0.107
FEATURE [App::DocumentObjectGroupPython] C_element018  label="C_element : 0.145"  # scripted group (container) (typed FeaturePython)
  n = 0.145
FEATURE [App::DocumentObjectGroupPython] N_element012  label="N_element : 0.022"  # scripted group (container) (typed FeaturePython)
  n = 0.022
FEATURE [App::DocumentObjectGroupPython] O_element017  label="O_element : 0.712"  # scripted group (container) (typed FeaturePython)
  n = 0.712
FEATURE [App::DocumentObjectGroupPython] Na_element004  label="Na_element : 0.004"  # scripted group (container) (typed FeaturePython)
  n = 0.002
FEATURE [App::DocumentObjectGroupPython] P_element004  label="P_element : 0.004"  # scripted group (container) (typed FeaturePython)
  n = 0.004
FEATURE [App::DocumentObjectGroupPython] S_element006  label="S_element : 0.005"  # scripted group (container) (typed FeaturePython)
  n = 0.002
FEATURE [App::DocumentObjectGroupPython] Cl_element003  label="Cl_element : 0.004"  # scripted group (container) (typed FeaturePython)
  n = 0.003
FEATURE [App::DocumentObjectGroupPython] K_element002  label="K_element : 0.003"  # scripted group (container) (typed FeaturePython)
  n = 0.003
FEATURE [App::DocumentObjectGroupPython] G4_BRAIN_ICRP  # scripted group (container) (typed FeaturePython)
  Dunit = g/cm3
  Dvalue = 1.04
  Group = -> [H_element017,C_element018,N_element012,O_element017,Na_element004,P_element004,S_element006,Cl_element003,K_element002]
  conduct = 2
  density = 1
  expand = 3
  formula = G4_BRAIN_ICRP
  name = G4_BRAIN_ICRP
  specific = 4
FEATURE [App::DocumentObjectGroupPython] C_element019  label="C_element : 4"  # scripted group (container) (typed FeaturePython)
  n = 4
  ref = C_element
FEATURE [App::DocumentObjectGroupPython] H_element018  label="H_element : 010"  # scripted group (container) (typed FeaturePython)
  n = 10
  ref = H_element
FEATURE [App::DocumentObjectGroupPython] G4_BUTANE  # scripted group (container) (typed FeaturePython)
  Dunit = g/cm3
  Dvalue = 0.00249343
  Group = -> [C_element019,H_element018]
  conduct = 2
  density = 1
  expand = 3
  formula = G4_BUTANE
  name = G4_BUTANE
  specific = 4
FEATURE [App::DocumentObjectGroupPython] C_element020  label="C_element : 008"  # scripted group (container) (typed FeaturePython)
  n = 4
  ref = C_element
FEATURE [App::DocumentObjectGroupPython] H_element019  label="H_element : 011"  # scripted group (container) (typed FeaturePython)
  n = 10
  ref = H_element
FEATURE [App::DocumentObjectGroupPython] O_element018  label="O_element : 007"  # scripted group (container) (typed FeaturePython)
  n = 1
  ref = O_element
FEATURE [App::DocumentObjectGroupPython] G4_N_BUTYL_ALCOHOL  label="G4_N-BUTYL_ALCOHOL"  # scripted group (container) (typed FeaturePython)
  Dunit = g/cm3
  Dvalue = 0.8098
  Group = -> [C_element020,H_element019,O_element018]
  conduct = 2
  density = 1
  expand = 3
  formula = G4_N-BUTYL_ALCOHOL
  name = G4_N-BUTYL_ALCOHOL
  specific = 4
FEATURE [App::DocumentObjectGroupPython] H_element020  label="H_element : 0.025"  # scripted group (container) (typed FeaturePython)
  n = 0.02468
FEATURE [App::DocumentObjectGroupPython] C_element021  label="C_element : 0.502"  # scripted group (container) (typed FeaturePython)
  n = 0.501611
FEATURE [App::DocumentObjectGroupPython] O_element019  label="O_element : 0.005"  # scripted group (container) (typed FeaturePython)
  n = 0.004527
FEATURE [App::DocumentObjectGroupPython] F_element004  label="F_element : 0.465"  # scripted group (container) (typed FeaturePython)
  n = 0.465209
FEATURE [App::DocumentObjectGroupPython] Si_element001  label="Si_element : 0.004"  # scripted group (container) (typed FeaturePython)
  n = 0.003973
FEATURE [App::DocumentObjectGroupPython] G4_C_552  label="G4_C-552"  # scripted group (container) (typed FeaturePython)
  Dunit = g/cm3
  Dvalue = 1.76
  Group = -> [H_element020,C_element021,O_element019,F_element004,Si_element001]
  conduct = 2
  density = 1
  expand = 3
  formula = G4_C-552
  name = G4_C-552
  specific = 4
FEATURE [App::DocumentObjectGroupPython] Cd_element001  label="Cd_element : 1"  # scripted group (container) (typed FeaturePython)
  n = 1
  ref = Cd_element
FEATURE [App::DocumentObjectGroupPython] Te_element001  label="Te_element : 1"  # scripted group (container) (typed FeaturePython)
  n = 1
  ref = Te_element
FEATURE [App::DocumentObjectGroupPython] G4_CADMIUM_TELLURIDE  # scripted group (container) (typed FeaturePython)
  Dunit = g/cm3
  Dvalue = 6.2
  Group = -> [Cd_element001,Te_element001]
  conduct = 2
  density = 1
  expand = 3
  formula = G4_CADMIUM_TELLURIDE
  name = G4_CADMIUM_TELLURIDE
  specific = 4
FEATURE [App::DocumentObjectGroupPython] Cd_element002  label="Cd_element : 002"  # scripted group (container) (typed FeaturePython)
  n = 1
  ref = Cd_element
FEATURE [App::DocumentObjectGroupPython] W_element001  label="W_element : 1"  # scripted group (container) (typed FeaturePython)
  n = 1
  ref = W_element
FEATURE [App::DocumentObjectGroupPython] O_element020  label="O_element : 008"  # scripted group (container) (typed FeaturePython)
  n = 4
  ref = O_element
FEATURE [App::DocumentObjectGroupPython] G4_CADMIUM_TUNGSTATE  # scripted group (container) (typed FeaturePython)
  Dunit = g/cm3
  Dvalue = 7.9
  Group = -> [Cd_element002,W_element001,O_element020]
  conduct = 2
  density = 1
  expand = 3
  formula = G4_CADMIUM_TUNGSTATE
  name = G4_CADMIUM_TUNGSTATE
  specific = 4
FEATURE [App::DocumentObjectGroupPython] Ca_element005  label="Ca_element : 1"  # scripted group (container) (typed FeaturePython)
  n = 1
  ref = Ca_element
FEATURE [App::DocumentObjectGroupPython] C_element022  label="C_element : 009"  # scripted group (container) (typed FeaturePython)
  n = 1
  ref = C_element
FEATURE [App::DocumentObjectGroupPython] O_element021  label="O_element : 009"  # scripted group (container) (typed FeaturePython)
  n = 3
  ref = O_element
FEATURE [App::DocumentObjectGroupPython] G4_CALCIUM_CARBONATE  # scripted group (container) (typed FeaturePython)
  Dunit = g/cm3
  Dvalue = 2.8
  Group = -> [Ca_element005,C_element022,O_element021]
  conduct = 2
  density = 1
  expand = 3
  formula = G4_CALCIUM_CARBONATE
  name = G4_CALCIUM_CARBONATE
  specific = 4
FEATURE [App::DocumentObjectGroupPython] Ca_element006  label="Ca_element : 002"  # scripted group (container) (typed FeaturePython)
  n = 1
  ref = Ca_element
FEATURE [App::DocumentObjectGroupPython] F_element005  label="F_element : 003"  # scripted group (container) (typed FeaturePython)
  n = 2
  ref = F_element
FEATURE [App::DocumentObjectGroupPython] G4_CALCIUM_FLUORIDE  # scripted group (container) (typed FeaturePython)
  Dunit = g/cm3
  Dvalue = 3.18
  Group = -> [Ca_element006,F_element005]
  conduct = 2
  density = 1
  expand = 3
  formula = G4_CALCIUM_FLUORIDE
  name = G4_CALCIUM_FLUORIDE
  specific = 4
FEATURE [App::DocumentObjectGroupPython] Ca_element007  label="Ca_element : 003"  # scripted group (container) (typed FeaturePython)
  n = 1
  ref = Ca_element
FEATURE [App::DocumentObjectGroupPython] O_element022  label="O_element : 010"  # scripted group (container) (typed FeaturePython)
  n = 1
  ref = O_element
FEATURE [App::DocumentObjectGroupPython] G4_CALCIUM_OXIDE  # scripted group (container) (typed FeaturePython)
  Dunit = g/cm3
  Dvalue = 3.3
  Group = -> [Ca_element007,O_element022]
  conduct = 2
  density = 1
  expand = 3
  formula = G4_CALCIUM_OXIDE
  name = G4_CALCIUM_OXIDE
  specific = 4
FEATURE [App::DocumentObjectGroupPython] Ca_element008  label="Ca_element : 004"  # scripted group (container) (typed FeaturePython)
  n = 1
  ref = Ca_element
FEATURE [App::DocumentObjectGroupPython] S_element007  label="S_element : 002"  # scripted group (container) (typed FeaturePython)
  n = 1
  ref = S_element
FEATURE [App::DocumentObjectGroupPython] O_element023  label="O_element : 011"  # scripted group (container) (typed FeaturePython)
  n = 4
  ref = O_element
FEATURE [App::DocumentObjectGroupPython] G4_CALCIUM_SULFATE  # scripted group (container) (typed FeaturePython)
  Dunit = g/cm3
  Dvalue = 2.96
  Group = -> [Ca_element008,S_element007,O_element023]
  conduct = 2
  density = 1
  expand = 3
  formula = G4_CALCIUM_SULFATE
  name = G4_CALCIUM_SULFATE
  specific = 4
FEATURE [App::DocumentObjectGroupPython] Ca_element009  label="Ca_element : 005"  # scripted group (container) (typed FeaturePython)
  n = 1
  ref = Ca_element
FEATURE [App::DocumentObjectGroupPython] W_element002  label="W_element : 002"  # scripted group (container) (typed FeaturePython)
  n = 1
  ref = W_element
FEATURE [App::DocumentObjectGroupPython] O_element024  label="O_element : 012"  # scripted group (container) (typed FeaturePython)
  n = 4
  ref = O_element
FEATURE [App::DocumentObjectGroupPython] G4_CALCIUM_TUNGSTATE  # scripted group (container) (typed FeaturePython)
  Dunit = g/cm3
  Dvalue = 6.062
  Group = -> [Ca_element009,W_element002,O_element024]
  conduct = 2
  density = 1
  expand = 3
  formula = G4_CALCIUM_TUNGSTATE
  name = G4_CALCIUM_TUNGSTATE
  specific = 4
FEATURE [App::DocumentObjectGroupPython] C_element023  label="C_element : 010"  # scripted group (container) (typed FeaturePython)
  n = 1
  ref = C_element
FEATURE [App::DocumentObjectGroupPython] O_element025  label="O_element : 013"  # scripted group (container) (typed FeaturePython)
  n = 2
  ref = O_element
FEATURE [App::DocumentObjectGroupPython] G4_CARBON_DIOXIDE  # scripted group (container) (typed FeaturePython)
  Dunit = g/cm3
  Dvalue = 0.00184212
  Group = -> [C_element023,O_element025]
  conduct = 2
  density = 1
  expand = 3
  formula = G4_CARBON_DIOXIDE
  name = G4_CARBON_DIOXIDE
  specific = 4
FEATURE [App::DocumentObjectGroupPython] C_element024  label="C_element : 011"  # scripted group (container) (typed FeaturePython)
  n = 1
  ref = C_element
FEATURE [App::DocumentObjectGroupPython] Cl_element004  label="Cl_element : 4"  # scripted group (container) (typed FeaturePython)
  n = 4
  ref = Cl_element
FEATURE [App::DocumentObjectGroupPython] G4_CARBON_TETRACHLORIDE  # scripted group (container) (typed FeaturePython)
  Dunit = g/cm3
  Dvalue = 1.594
  Group = -> [C_element024,Cl_element004]
  conduct = 2
  density = 1
  expand = 3
  formula = G4_CARBON_TETRACHLORIDE
  name = G4_CARBON_TETRACHLORIDE
  specific = 4
FEATURE [App::DocumentObjectGroupPython] C_element025  label="C_element : 012"  # scripted group (container) (typed FeaturePython)
  n = 6
  ref = C_element
FEATURE [App::DocumentObjectGroupPython] H_element021  label="H_element : 012"  # scripted group (container) (typed FeaturePython)
  n = 10
  ref = H_element
FEATURE [App::DocumentObjectGroupPython] O_element026  label="O_element : 5"  # scripted group (container) (typed FeaturePython)
  n = 5
  ref = O_element
FEATURE [App::DocumentObjectGroupPython] G4_CELLULOSE_CELLOPHANE  # scripted group (container) (typed FeaturePython)
  Dunit = g/cm3
  Dvalue = 1.42
  Group = -> [C_element025,H_element021,O_element026]
  conduct = 2
  density = 1
  expand = 3
  formula = G4_CELLULOSE_CELLOPHANE
  name = G4_CELLULOSE_CELLOPHANE
  specific = 4
FEATURE [App::DocumentObjectGroupPython] H_element022  label="H_element : 0.067"  # scripted group (container) (typed FeaturePython)
  n = 0.067125
FEATURE [App::DocumentObjectGroupPython] C_element026  label="C_element : 0.545"  # scripted group (container) (typed FeaturePython)
  n = 0.545403
FEATURE [App::DocumentObjectGroupPython] O_element027  label="O_element : 0.387"  # scripted group (container) (typed FeaturePython)
  n = 0.387472
FEATURE [App::DocumentObjectGroupPython] G4_CELLULOSE_BUTYRATE  # scripted group (container) (typed FeaturePython)
  Dunit = g/cm3
  Dvalue = 1.2
  Group = -> [H_element022,C_element026,O_element027]
  conduct = 2
  density = 1
  expand = 3
  formula = G4_CELLULOSE_BUTYRATE
  name = G4_CELLULOSE_BUTYRATE
  specific = 4
FEATURE [App::DocumentObjectGroupPython] H_element023  label="H_element : 0.029"  # scripted group (container) (typed FeaturePython)
  n = 0.029216
FEATURE [App::DocumentObjectGroupPython] C_element027  label="C_element : 0.271"  # scripted group (container) (typed FeaturePython)
  n = 0.271296
FEATURE [App::DocumentObjectGroupPython] N_element013  label="N_element : 0.121"  # scripted group (container) (typed FeaturePython)
  n = 0.121276
FEATURE [App::DocumentObjectGroupPython] O_element028  label="O_element : 0.578"  # scripted group (container) (typed FeaturePython)
  n = 0.578212
FEATURE [App::DocumentObjectGroupPython] G4_CELLULOSE_NITRATE  # scripted group (container) (typed FeaturePython)
  Dunit = g/cm3
  Dvalue = 1.49
  Group = -> [H_element023,C_element027,N_element013,O_element028]
  conduct = 2
  density = 1
  expand = 3
  formula = G4_CELLULOSE_NITRATE
  name = G4_CELLULOSE_NITRATE
  specific = 4
FEATURE [App::DocumentObjectGroupPython] H_element024  label="H_element : 0.108"  # scripted group (container) (typed FeaturePython)
  n = 0.107596
FEATURE [App::DocumentObjectGroupPython] N_element014  label="N_element : 0.001"  # scripted group (container) (typed FeaturePython)
  n = 0.0008
FEATURE [App::DocumentObjectGroupPython] O_element029  label="O_element : 0.875"  # scripted group (container) (typed FeaturePython)
  n = 0.874976
FEATURE [App::DocumentObjectGroupPython] S_element008  label="S_element : 0.015"  # scripted group (container) (typed FeaturePython)
  n = 0.014627
FEATURE [App::DocumentObjectGroupPython] Ce_element001  label="Ce_element : 0.002"  # scripted group (container) (typed FeaturePython)
  n = 0.002001
FEATURE [App::DocumentObjectGroupPython] G4_CERIC_SULFATE  # scripted group (container) (typed FeaturePython)
  Dunit = g/cm3
  Dvalue = 1.03
  Group = -> [H_element024,N_element014,O_element029,S_element008,Ce_element001]
  conduct = 2
  density = 1
  expand = 3
  formula = G4_CERIC_SULFATE
  name = G4_CERIC_SULFATE
  specific = 4
FEATURE [App::DocumentObjectGroupPython] Cs_element001  label="Cs_element : 1"  # scripted group (container) (typed FeaturePython)
  n = 1
  ref = Cs_element
FEATURE [App::DocumentObjectGroupPython] F_element006  label="F_element : 1"  # scripted group (container) (typed FeaturePython)
  n = 1
  ref = F_element
FEATURE [App::DocumentObjectGroupPython] G4_CESIUM_FLUORIDE  # scripted group (container) (typed FeaturePython)
  Dunit = g/cm3
  Dvalue = 4.115
  Group = -> [Cs_element001,F_element006]
  conduct = 2
  density = 1
  expand = 3
  formula = G4_CESIUM_FLUORIDE
  name = G4_CESIUM_FLUORIDE
  specific = 4
FEATURE [App::DocumentObjectGroupPython] Cs_element002  label="Cs_element : 002"  # scripted group (container) (typed FeaturePython)
  n = 1
  ref = Cs_element
FEATURE [App::DocumentObjectGroupPython] I_element001  label="I_element : 1"  # scripted group (container) (typed FeaturePython)
  n = 1
  ref = I_element
FEATURE [App::DocumentObjectGroupPython] G4_CESIUM_IODIDE  # scripted group (container) (typed FeaturePython)
  Dunit = g/cm3
  Dvalue = 4.51
  Group = -> [Cs_element002,I_element001]
  conduct = 2
  density = 1
  expand = 3
  formula = G4_CESIUM_IODIDE
  name = G4_CESIUM_IODIDE
  specific = 4
FEATURE [App::DocumentObjectGroupPython] C_element028  label="C_element : 013"  # scripted group (container) (typed FeaturePython)
  n = 6
  ref = C_element
FEATURE [App::DocumentObjectGroupPython] H_element025  label="H_element : 013"  # scripted group (container) (typed FeaturePython)
  n = 5
  ref = H_element
FEATURE [App::DocumentObjectGroupPython] Cl_element005  label="Cl_element : 1"  # scripted group (container) (typed FeaturePython)
  n = 1
  ref = Cl_element
FEATURE [App::DocumentObjectGroupPython] G4_CHLOROBENZENE  # scripted group (container) (typed FeaturePython)
  Dunit = g/cm3
  Dvalue = 1.1058
  Group = -> [C_element028,H_element025,Cl_element005]
  conduct = 2
  density = 1
  expand = 3
  formula = G4_CHLOROBENZENE
  name = G4_CHLOROBENZENE
  specific = 4
FEATURE [App::DocumentObjectGroupPython] C_element029  label="C_element : 014"  # scripted group (container) (typed FeaturePython)
  n = 1
  ref = C_element
FEATURE [App::DocumentObjectGroupPython] H_element026  label="H_element : 1"  # scripted group (container) (typed FeaturePython)
  n = 1
  ref = H_element
FEATURE [App::DocumentObjectGroupPython] Cl_element006  label="Cl_element : 3"  # scripted group (container) (typed FeaturePython)
  n = 3
  ref = Cl_element
FEATURE [App::DocumentObjectGroupPython] G4_CHLOROFORM  # scripted group (container) (typed FeaturePython)
  Dunit = g/cm3
  Dvalue = 1.4832
  Group = -> [C_element029,H_element026,Cl_element006]
  conduct = 2
  density = 1
  expand = 3
  formula = G4_CHLOROFORM
  name = G4_CHLOROFORM
  specific = 4
FEATURE [App::DocumentObjectGroupPython] H_element027  label="H_element : 0.010"  # scripted group (container) (typed FeaturePython)
  n = 0.01
FEATURE [App::DocumentObjectGroupPython] C_element030  label="C_element : 0.001"  # scripted group (container) (typed FeaturePython)
  n = 0.001
FEATURE [App::DocumentObjectGroupPython] O_element030  label="O_element : 0.529"  # scripted group (container) (typed FeaturePython)
  n = 0.529107
FEATURE [App::DocumentObjectGroupPython] Na_element005  label="Na_element : 0.016"  # scripted group (container) (typed FeaturePython)
  n = 0.016
FEATURE [App::DocumentObjectGroupPython] Mg_element003  label="Mg_element : 0.004"  # scripted group (container) (typed FeaturePython)
  n = 0.002
FEATURE [App::DocumentObjectGroupPython] Al_element002  label="Al_element : 0.034"  # scripted group (container) (typed FeaturePython)
  n = 0.033872
FEATURE [App::DocumentObjectGroupPython] Si_element002  label="Si_element : 0.337"  # scripted group (container) (typed FeaturePython)
  n = 0.337021
FEATURE [App::DocumentObjectGroupPython] K_element003  label="K_element : 0.013"  # scripted group (container) (typed FeaturePython)
  n = 0.013
FEATURE [App::DocumentObjectGroupPython] Ca_element010  label="Ca_element : 0.044"  # scripted group (container) (typed FeaturePython)
  n = 0.044
FEATURE [App::DocumentObjectGroupPython] Fe_element002  label="Fe_element : 0.014"  # scripted group (container) (typed FeaturePython)
  n = 0.014
FEATURE [App::DocumentObjectGroupPython] G4_CONCRETE  # scripted group (container) (typed FeaturePython)
  Dunit = g/cm3
  Dvalue = 2.3
  Group = -> [H_element027,C_element030,O_element030,Na_element005,Mg_element003,Al_element002,Si_element002,K_element003,Ca_element010,Fe_element002]
  conduct = 2
  density = 1
  expand = 3
  formula = G4_CONCRETE
  name = G4_CONCRETE
  specific = 4
FEATURE [App::DocumentObjectGroupPython] C_element031  label="C_element : 015"  # scripted group (container) (typed FeaturePython)
  n = 6
  ref = C_element
FEATURE [App::DocumentObjectGroupPython] H_element028  label="H_element : 12"  # scripted group (container) (typed FeaturePython)
  n = 12
  ref = H_element
FEATURE [App::DocumentObjectGroupPython] G4_CYCLOHEXANE  # scripted group (container) (typed FeaturePython)
  Dunit = g/cm3
  Dvalue = 0.779
  Group = -> [C_element031,H_element028]
  conduct = 2
  density = 1
  expand = 3
  formula = G4_CYCLOHEXANE
  name = G4_CYCLOHEXANE
  specific = 4
FEATURE [App::DocumentObjectGroupPython] C_element032  label="C_element : 016"  # scripted group (container) (typed FeaturePython)
  n = 6
  ref = C_element
FEATURE [App::DocumentObjectGroupPython] H_element029  label="H_element : 4"  # scripted group (container) (typed FeaturePython)
  n = 4
  ref = H_element
FEATURE [App::DocumentObjectGroupPython] Cl_element007  label="Cl_element : 2"  # scripted group (container) (typed FeaturePython)
  n = 2
  ref = Cl_element
FEATURE [App::DocumentObjectGroupPython] G4_1_2_DICHLOROBENZENE  label="G4_1.2-DICHLOROBENZENE"  # scripted group (container) (typed FeaturePython)
  Dunit = g/cm3
  Dvalue = 1.3048
  Group = -> [C_element032,H_element029,Cl_element007]
  conduct = 2
  density = 1
  expand = 3
  formula = G4_1.2-DICHLOROBENZENE
  name = G4_1.2-DICHLOROBENZENE
  specific = 4
FEATURE [App::DocumentObjectGroupPython] C_element033  label="C_element : 017"  # scripted group (container) (typed FeaturePython)
  n = 4
  ref = C_element
FEATURE [App::DocumentObjectGroupPython] H_element030  label="H_element : 8"  # scripted group (container) (typed FeaturePython)
  n = 8
  ref = H_element
FEATURE [App::DocumentObjectGroupPython] O_element031  label="O_element : 014"  # scripted group (container) (typed FeaturePython)
  n = 1
  ref = O_element
FEATURE [App::DocumentObjectGroupPython] Cl_element008  label="Cl_element : 005"  # scripted group (container) (typed FeaturePython)
  n = 2
  ref = Cl_element
FEATURE [App::DocumentObjectGroupPython] G4_DICHLORODIETHYL_ETHER  # scripted group (container) (typed FeaturePython)
  Dunit = g/cm3
  Dvalue = 1.2199
  Group = -> [C_element033,H_element030,O_element031,Cl_element008]
  conduct = 2
  density = 1
  expand = 3
  formula = G4_DICHLORODIETHYL_ETHER
  name = G4_DICHLORODIETHYL_ETHER
  specific = 4
FEATURE [App::DocumentObjectGroupPython] C_element034  label="C_element : 018"  # scripted group (container) (typed FeaturePython)
  n = 2
  ref = C_element
FEATURE [App::DocumentObjectGroupPython] H_element031  label="H_element : 014"  # scripted group (container) (typed FeaturePython)
  n = 4
  ref = H_element
FEATURE [App::DocumentObjectGroupPython] Cl_element009  label="Cl_element : 006"  # scripted group (container) (typed FeaturePython)
  n = 2
  ref = Cl_element
FEATURE [App::DocumentObjectGroupPython] G4_1_2_DICHLOROETHANE  label="G4_1.2-DICHLOROETHANE"  # scripted group (container) (typed FeaturePython)
  Dunit = g/cm3
  Dvalue = 1.2351
  Group = -> [C_element034,H_element031,Cl_element009]
  conduct = 2
  density = 1
  expand = 3
  formula = G4_1.2-DICHLOROETHANE
  name = G4_1.2-DICHLOROETHANE
  specific = 4
FEATURE [App::DocumentObjectGroupPython] C_element035  label="C_element : 019"  # scripted group (container) (typed FeaturePython)
  n = 4
  ref = C_element
FEATURE [App::DocumentObjectGroupPython] H_element032  label="H_element : 015"  # scripted group (container) (typed FeaturePython)
  n = 10
  ref = H_element
FEATURE [App::DocumentObjectGroupPython] O_element032  label="O_element : 015"  # scripted group (container) (typed FeaturePython)
  n = 1
  ref = O_element
FEATURE [App::DocumentObjectGroupPython] G4_DIETHYL_ETHER  # scripted group (container) (typed FeaturePython)
  Dunit = g/cm3
  Dvalue = 0.71378
  Group = -> [C_element035,H_element032,O_element032]
  conduct = 2
  density = 1
  expand = 3
  formula = G4_DIETHYL_ETHER
  name = G4_DIETHYL_ETHER
  specific = 4
FEATURE [App::DocumentObjectGroupPython] C_element036  label="C_element : 020"  # scripted group (container) (typed FeaturePython)
  n = 3
  ref = C_element
FEATURE [App::DocumentObjectGroupPython] H_element033  label="H_element : 016"  # scripted group (container) (typed FeaturePython)
  n = 7
  ref = H_element
FEATURE [App::DocumentObjectGroupPython] N_element015  label="N_element : 008"  # scripted group (container) (typed FeaturePython)
  n = 1
  ref = N_element
FEATURE [App::DocumentObjectGroupPython] O_element033  label="O_element : 016"  # scripted group (container) (typed FeaturePython)
  n = 1
  ref = O_element
FEATURE [App::DocumentObjectGroupPython] G4_N_N_DIMETHYL_FORMAMIDE  label="G4_N.N-DIMETHYL_FORMAMIDE"  # scripted group (container) (typed FeaturePython)
  Dunit = g/cm3
  Dvalue = 0.9487
  Group = -> [C_element036,H_element033,N_element015,O_element033]
  conduct = 2
  density = 1
  expand = 3
  formula = G4_N.N-DIMETHYL_FORMAMIDE
  name = G4_N.N-DIMETHYL_FORMAMIDE
  specific = 4
FEATURE [App::DocumentObjectGroupPython] C_element037  label="C_element : 021"  # scripted group (container) (typed FeaturePython)
  n = 2
  ref = C_element
FEATURE [App::DocumentObjectGroupPython] H_element034  label="H_element : 017"  # scripted group (container) (typed FeaturePython)
  n = 6
  ref = H_element
FEATURE [App::DocumentObjectGroupPython] O_element034  label="O_element : 017"  # scripted group (container) (typed FeaturePython)
  n = 1
  ref = O_element
FEATURE [App::DocumentObjectGroupPython] S_element009  label="S_element : 003"  # scripted group (container) (typed FeaturePython)
  n = 1
  ref = S_element
FEATURE [App::DocumentObjectGroupPython] G4_DIMETHYL_SULFOXIDE  # scripted group (container) (typed FeaturePython)
  Dunit = g/cm3
  Dvalue = 1.1014
  Group = -> [C_element037,H_element034,O_element034,S_element009]
  conduct = 2
  density = 1
  expand = 3
  formula = G4_DIMETHYL_SULFOXIDE
  name = G4_DIMETHYL_SULFOXIDE
  specific = 4
FEATURE [App::DocumentObjectGroupPython] C_element038  label="C_element : 022"  # scripted group (container) (typed FeaturePython)
  n = 2
  ref = C_element
FEATURE [App::DocumentObjectGroupPython] H_element035  label="H_element : 018"  # scripted group (container) (typed FeaturePython)
  n = 6
  ref = H_element
FEATURE [App::DocumentObjectGroupPython] G4_ETHANE  # scripted group (container) (typed FeaturePython)
  Dunit = g/cm3
  Dvalue = 0.00125324
  Group = -> [C_element038,H_element035]
  conduct = 2
  density = 1
  expand = 3
  formula = G4_ETHANE
  name = G4_ETHANE
  specific = 4
FEATURE [App::DocumentObjectGroupPython] C_element039  label="C_element : 023"  # scripted group (container) (typed FeaturePython)
  n = 2
  ref = C_element
FEATURE [App::DocumentObjectGroupPython] H_element036  label="H_element : 019"  # scripted group (container) (typed FeaturePython)
  n = 6
  ref = H_element
FEATURE [App::DocumentObjectGroupPython] O_element035  label="O_element : 018"  # scripted group (container) (typed FeaturePython)
  n = 1
  ref = O_element
FEATURE [App::DocumentObjectGroupPython] G4_ETHYL_ALCOHOL  # scripted group (container) (typed FeaturePython)
  Dunit = g/cm3
  Dvalue = 0.7893
  Group = -> [C_element039,H_element036,O_element035]
  conduct = 2
  density = 1
  expand = 3
  formula = G4_ETHYL_ALCOHOL
  name = G4_ETHYL_ALCOHOL
  specific = 4
FEATURE [App::DocumentObjectGroupPython] H_element037  label="H_element : 0.090"  # scripted group (container) (typed FeaturePython)
  n = 0.090027
FEATURE [App::DocumentObjectGroupPython] C_element040  label="C_element : 0.585"  # scripted group (container) (typed FeaturePython)
  n = 0.585182
FEATURE [App::DocumentObjectGroupPython] O_element036  label="O_element : 0.325"  # scripted group (container) (typed FeaturePython)
  n = 0.324791
FEATURE [App::DocumentObjectGroupPython] G4_ETHYL_CELLULOSE  # scripted group (container) (typed FeaturePython)
  Dunit = g/cm3
  Dvalue = 1.13
  Group = -> [H_element037,C_element040,O_element036]
  conduct = 2
  density = 1
  expand = 3
  formula = G4_ETHYL_CELLULOSE
  name = G4_ETHYL_CELLULOSE
  specific = 4
FEATURE [App::DocumentObjectGroupPython] C_element041  label="C_element : 024"  # scripted group (container) (typed FeaturePython)
  n = 2
  ref = C_element
FEATURE [App::DocumentObjectGroupPython] H_element038  label="H_element : 020"  # scripted group (container) (typed FeaturePython)
  n = 4
  ref = H_element
FEATURE [App::DocumentObjectGroupPython] G4_ETHYLENE  # scripted group (container) (typed FeaturePython)
  Dunit = g/cm3
  Dvalue = 0.00117497
  Group = -> [C_element041,H_element038]
  conduct = 2
  density = 1
  expand = 3
  formula = G4_ETHYLENE
  name = G4_ETHYLENE
  specific = 4
FEATURE [App::DocumentObjectGroupPython] H_element039  label="H_element : 0.096"  # scripted group (container) (typed FeaturePython)
  n = 0.096
FEATURE [App::DocumentObjectGroupPython] C_element042  label="C_element : 0.195"  # scripted group (container) (typed FeaturePython)
  n = 0.195
FEATURE [App::DocumentObjectGroupPython] N_element016  label="N_element : 0.057"  # scripted group (container) (typed FeaturePython)
  n = 0.057
FEATURE [App::DocumentObjectGroupPython] O_element037  label="O_element : 0.646"  # scripted group (container) (typed FeaturePython)
  n = 0.646
FEATURE [App::DocumentObjectGroupPython] Na_element006  label="Na_element : 0.017"  # scripted group (container) (typed FeaturePython)
  n = 0.001
FEATURE [App::DocumentObjectGroupPython] P_element005  label="P_element : 0.104"  # scripted group (container) (typed FeaturePython)
  n = 0.001
FEATURE [App::DocumentObjectGroupPython] S_element010  label="S_element : 0.016"  # scripted group (container) (typed FeaturePython)
  n = 0.003
FEATURE [App::DocumentObjectGroupPython] Cl_element010  label="Cl_element : 0.005"  # scripted group (container) (typed FeaturePython)
  n = 0.001
FEATURE [App::DocumentObjectGroupPython] G4_EYE_LENS_ICRP  # scripted group (container) (typed FeaturePython)
  Dunit = g/cm3
  Dvalue = 1.07
  Group = -> [H_element039,C_element042,N_element016,O_element037,Na_element006,P_element005,S_element010,Cl_element010]
  conduct = 2
  density = 1
  expand = 3
  formula = G4_EYE_LENS_ICRP
  name = G4_EYE_LENS_ICRP
  specific = 4
FEATURE [App::DocumentObjectGroupPython] Fe_element003  label="Fe_element : 2"  # scripted group (container) (typed FeaturePython)
  n = 2
  ref = Fe_element
FEATURE [App::DocumentObjectGroupPython] O_element038  label="O_element : 019"  # scripted group (container) (typed FeaturePython)
  n = 3
  ref = O_element
FEATURE [App::DocumentObjectGroupPython] G4_FERRIC_OXIDE  # scripted group (container) (typed FeaturePython)
  Dunit = g/cm3
  Dvalue = 5.2
  Group = -> [Fe_element003,O_element038]
  conduct = 2
  density = 1
  expand = 3
  formula = G4_FERRIC_OXIDE
  name = G4_FERRIC_OXIDE
  specific = 4
FEATURE [App::DocumentObjectGroupPython] Fe_element004  label="Fe_element : 1"  # scripted group (container) (typed FeaturePython)
  n = 1
  ref = Fe_element
FEATURE [App::DocumentObjectGroupPython] B_element003  label="B_element : 1"  # scripted group (container) (typed FeaturePython)
  n = 1
  ref = B_element
FEATURE [App::DocumentObjectGroupPython] G4_FERROBORIDE  # scripted group (container) (typed FeaturePython)
  Dunit = g/cm3
  Dvalue = 7.15
  Group = -> [Fe_element004,B_element003]
  conduct = 2
  density = 1
  expand = 3
  formula = G4_FERROBORIDE
  name = G4_FERROBORIDE
  specific = 4
FEATURE [App::DocumentObjectGroupPython] Fe_element005  label="Fe_element : 003"  # scripted group (container) (typed FeaturePython)
  n = 1
  ref = Fe_element
FEATURE [App::DocumentObjectGroupPython] O_element039  label="O_element : 020"  # scripted group (container) (typed FeaturePython)
  n = 1
  ref = O_element
FEATURE [App::DocumentObjectGroupPython] G4_FERROUS_OXIDE  # scripted group (container) (typed FeaturePython)
  Dunit = g/cm3
  Dvalue = 5.7
  Group = -> [Fe_element005,O_element039]
  conduct = 2
  density = 1
  expand = 3
  formula = G4_FERROUS_OXIDE
  name = G4_FERROUS_OXIDE
  specific = 4
FEATURE [App::DocumentObjectGroupPython] H_element040  label="H_element : 0.115"  # scripted group (container) (typed FeaturePython)
  n = 0.108259
FEATURE [App::DocumentObjectGroupPython] N_element017  label="N_element : 0.000"  # scripted group (container) (typed FeaturePython)
  n = 2.7e-05
FEATURE [App::DocumentObjectGroupPython] O_element040  label="O_element : 0.879"  # scripted group (container) (typed FeaturePython)
  n = 0.878636
FEATURE [App::DocumentObjectGroupPython] Na_element007  label="Na_element : 0.000"  # scripted group (container) (typed FeaturePython)
  n = 2.2e-05
FEATURE [App::DocumentObjectGroupPython] S_element011  label="S_element : 0.013"  # scripted group (container) (typed FeaturePython)
  n = 0.012968
FEATURE [App::DocumentObjectGroupPython] Cl_element011  label="Cl_element : 0.000"  # scripted group (container) (typed FeaturePython)
  n = 3.4e-05
FEATURE [App::DocumentObjectGroupPython] Fe_element006  label="Fe_element : 0.000"  # scripted group (container) (typed FeaturePython)
  n = 5.4e-05
FEATURE [App::DocumentObjectGroupPython] G4_FERROUS_SULFATE  # scripted group (container) (typed FeaturePython)
  Dunit = g/cm3
  Dvalue = 1.024
  Group = -> [H_element040,N_element017,O_element040,Na_element007,S_element011,Cl_element011,Fe_element006]
  conduct = 2
  density = 1
  expand = 3
  formula = G4_FERROUS_SULFATE
  name = G4_FERROUS_SULFATE
  specific = 4
FEATURE [App::DocumentObjectGroupPython] C_element043  label="C_element : 0.099"  # scripted group (container) (typed FeaturePython)
  n = 0.099335
FEATURE [App::DocumentObjectGroupPython] F_element007  label="F_element : 0.314"  # scripted group (container) (typed FeaturePython)
  n = 0.314247
FEATURE [App::DocumentObjectGroupPython] Cl_element012  label="Cl_element : 0.586"  # scripted group (container) (typed FeaturePython)
  n = 0.586418
FEATURE [App::DocumentObjectGroupPython] G4_FREON_12  label="G4_FREON-12"  # scripted group (container) (typed FeaturePython)
  Dunit = g/cm3
  Dvalue = 1.12
  Group = -> [C_element043,F_element007,Cl_element012]
  conduct = 2
  density = 1
  expand = 3
  formula = G4_FREON-12
  name = G4_FREON-12
  specific = 4
FEATURE [App::DocumentObjectGroupPython] C_element044  label="C_element : 0.057"  # scripted group (container) (typed FeaturePython)
  n = 0.057245
FEATURE [App::DocumentObjectGroupPython] F_element008  label="F_element : 0.181"  # scripted group (container) (typed FeaturePython)
  n = 0.181096
FEATURE [App::DocumentObjectGroupPython] Br_element001  label="Br_element : 0.762"  # scripted group (container) (typed FeaturePython)
  n = 0.761659
FEATURE [App::DocumentObjectGroupPython] G4_FREON_12B2  label="G4_FREON-12B2"  # scripted group (container) (typed FeaturePython)
  Dunit = g/cm3
  Dvalue = 1.8
  Group = -> [C_element044,F_element008,Br_element001]
  conduct = 2
  density = 1
  expand = 3
  formula = G4_FREON-12B2
  name = G4_FREON-12B2
  specific = 4
FEATURE [App::DocumentObjectGroupPython] C_element045  label="C_element : 0.115"  # scripted group (container) (typed FeaturePython)
  n = 0.114983
FEATURE [App::DocumentObjectGroupPython] F_element009  label="F_element : 0.546"  # scripted group (container) (typed FeaturePython)
  n = 0.545621
FEATURE [App::DocumentObjectGroupPython] Cl_element013  label="Cl_element : 0.339"  # scripted group (container) (typed FeaturePython)
  n = 0.339396
FEATURE [App::DocumentObjectGroupPython] G4_FREON_13  label="G4_FREON-13"  # scripted group (container) (typed FeaturePython)
  Dunit = g/cm3
  Dvalue = 0.95
  Group = -> [C_element045,F_element009,Cl_element013]
  conduct = 2
  density = 1
  expand = 3
  formula = G4_FREON-13
  name = G4_FREON-13
  specific = 4
FEATURE [App::DocumentObjectGroupPython] C_element046  label="C_element : 025"  # scripted group (container) (typed FeaturePython)
  n = 1
  ref = C_element
FEATURE [App::DocumentObjectGroupPython] F_element010  label="F_element : 3"  # scripted group (container) (typed FeaturePython)
  n = 3
  ref = F_element
FEATURE [App::DocumentObjectGroupPython] Br_element002  label="Br_element : 1"  # scripted group (container) (typed FeaturePython)
  n = 1
  ref = Br_element
FEATURE [App::DocumentObjectGroupPython] G4_FREON_13B1  label="G4_FREON-13B1"  # scripted group (container) (typed FeaturePython)
  Dunit = g/cm3
  Dvalue = 1.5
  Group = -> [C_element046,F_element010,Br_element002]
  conduct = 2
  density = 1
  expand = 3
  formula = G4_FREON-13B1
  name = G4_FREON-13B1
  specific = 4
FEATURE [App::DocumentObjectGroupPython] C_element047  label="C_element : 0.061"  # scripted group (container) (typed FeaturePython)
  n = 0.061309
FEATURE [App::DocumentObjectGroupPython] F_element011  label="F_element : 0.291"  # scripted group (container) (typed FeaturePython)
  n = 0.290924
FEATURE [App::DocumentObjectGroupPython] I_element002  label="I_element : 0.648"  # scripted group (container) (typed FeaturePython)
  n = 0.647767
FEATURE [App::DocumentObjectGroupPython] G4_FREON_13I1  label="G4_FREON-13I1"  # scripted group (container) (typed FeaturePython)
  Dunit = g/cm3
  Dvalue = 1.8
  Group = -> [C_element047,F_element011,I_element002]
  conduct = 2
  density = 1
  expand = 3
  formula = G4_FREON-13I1
  name = G4_FREON-13I1
  specific = 4
FEATURE [App::DocumentObjectGroupPython] Gd_element001  label="Gd_element : 2"  # scripted group (container) (typed FeaturePython)
  n = 2
  ref = Gd_element
FEATURE [App::DocumentObjectGroupPython] O_element041  label="O_element : 021"  # scripted group (container) (typed FeaturePython)
  n = 2
  ref = O_element
FEATURE [App::DocumentObjectGroupPython] S_element012  label="S_element : 004"  # scripted group (container) (typed FeaturePython)
  n = 1
  ref = S_element
FEATURE [App::DocumentObjectGroupPython] G4_GADOLINIUM_OXYSULFIDE  # scripted group (container) (typed FeaturePython)
  Dunit = g/cm3
  Dvalue = 7.44
  Group = -> [Gd_element001,O_element041,S_element012]
  conduct = 2
  density = 1
  expand = 3
  formula = G4_GADOLINIUM_OXYSULFIDE
  name = G4_GADOLINIUM_OXYSULFIDE
  specific = 4
FEATURE [App::DocumentObjectGroupPython] Ga_element001  label="Ga_element : 1"  # scripted group (container) (typed FeaturePython)
  n = 1
  ref = Ga_element
FEATURE [App::DocumentObjectGroupPython] As_element001  label="As_element : 1"  # scripted group (container) (typed FeaturePython)
  n = 1
  ref = As_element
FEATURE [App::DocumentObjectGroupPython] G4_GALLIUM_ARSENIDE  # scripted group (container) (typed FeaturePython)
  Dunit = g/cm3
  Dvalue = 5.31
  Group = -> [Ga_element001,As_element001]
  conduct = 2
  density = 1
  expand = 3
  formula = G4_GALLIUM_ARSENIDE
  name = G4_GALLIUM_ARSENIDE
  specific = 4
FEATURE [App::DocumentObjectGroupPython] H_element041  label="H_element : 0.081"  # scripted group (container) (typed FeaturePython)
  n = 0.08118
FEATURE [App::DocumentObjectGroupPython] C_element048  label="C_element : 0.416"  # scripted group (container) (typed FeaturePython)
  n = 0.41606
FEATURE [App::DocumentObjectGroupPython] N_element018  label="N_element : 0.111"  # scripted group (container) (typed FeaturePython)
  n = 0.11124
FEATURE [App::DocumentObjectGroupPython] O_element042  label="O_element : 0.381"  # scripted group (container) (typed FeaturePython)
  n = 0.38064
FEATURE [App::DocumentObjectGroupPython] S_element013  label="S_element : 0.011"  # scripted group (container) (typed FeaturePython)
  n = 0.01088
FEATURE [App::DocumentObjectGroupPython] G4_GEL_PHOTO_EMULSION  # scripted group (container) (typed FeaturePython)
  Dunit = g/cm3
  Dvalue = 1.2914
  Group = -> [H_element041,C_element048,N_element018,O_element042,S_element013]
  conduct = 2
  density = 1
  expand = 3
  formula = G4_GEL_PHOTO_EMULSION
  name = G4_GEL_PHOTO_EMULSION
  specific = 4
FEATURE [App::DocumentObjectGroupPython] B_element004  label="B_element : 0.040"  # scripted group (container) (typed FeaturePython)
  n = 0.0400639
FEATURE [App::DocumentObjectGroupPython] O_element043  label="O_element : 0.540"  # scripted group (container) (typed FeaturePython)
  n = 0.539561
FEATURE [App::DocumentObjectGroupPython] Na_element008  label="Na_element : 0.028"  # scripted group (container) (typed FeaturePython)
  n = 0.0281909
FEATURE [App::DocumentObjectGroupPython] Al_element003  label="Al_element : 0.012"  # scripted group (container) (typed FeaturePython)
  n = 0.011644
FEATURE [App::DocumentObjectGroupPython] Si_element003  label="Si_element : 0.377"  # scripted group (container) (typed FeaturePython)
  n = 0.377219
FEATURE [App::DocumentObjectGroupPython] K_element004  label="K_element : 0.014"  # scripted group (container) (typed FeaturePython)
  n = 0.00332099
FEATURE [App::DocumentObjectGroupPython] G4_Pyrex_Glass  # scripted group (container) (typed FeaturePython)
  Dunit = g/cm3
  Dvalue = 2.23
  Group = -> [B_element004,O_element043,Na_element008,Al_element003,Si_element003,K_element004]
  conduct = 2
  density = 1
  expand = 3
  formula = G4_Pyrex_Glass
  name = G4_Pyrex_Glass
  specific = 4
FEATURE [App::DocumentObjectGroupPython] O_element044  label="O_element : 0.156"  # scripted group (container) (typed FeaturePython)
  n = 0.156453
FEATURE [App::DocumentObjectGroupPython] Si_element004  label="Si_element : 0.081"  # scripted group (container) (typed FeaturePython)
  n = 0.080866
FEATURE [App::DocumentObjectGroupPython] Ti_element001  label="Ti_element : 0.008"  # scripted group (container) (typed FeaturePython)
  n = 0.008092
FEATURE [App::DocumentObjectGroupPython] As_element002  label="As_element : 0.003"  # scripted group (container) (typed FeaturePython)
  n = 0.002651
FEATURE [App::DocumentObjectGroupPython] Pb_element001  label="Pb_element : 0.752"  # scripted group (container) (typed FeaturePython)
  n = 0.751938
FEATURE [App::DocumentObjectGroupPython] G4_GLASS_LEAD  # scripted group (container) (typed FeaturePython)
  Dunit = g/cm3
  Dvalue = 6.22
  Group = -> [O_element044,Si_element004,Ti_element001,As_element002,Pb_element001]
  conduct = 2
  density = 1
  expand = 3
  formula = G4_GLASS_LEAD
  name = G4_GLASS_LEAD
  specific = 4
FEATURE [App::DocumentObjectGroupPython] O_element045  label="O_element : 0.460"  # scripted group (container) (typed FeaturePython)
  n = 0.4598
FEATURE [App::DocumentObjectGroupPython] Na_element009  label="Na_element : 0.096"  # scripted group (container) (typed FeaturePython)
  n = 0.0964411
FEATURE [App::DocumentObjectGroupPython] Si_element005  label="Si_element : 0.378"  # scripted group (container) (typed FeaturePython)
  n = 0.336553
FEATURE [App::DocumentObjectGroupPython] Ca_element011  label="Ca_element : 0.107"  # scripted group (container) (typed FeaturePython)
  n = 0.107205
FEATURE [App::DocumentObjectGroupPython] G4_GLASS_PLATE  # scripted group (container) (typed FeaturePython)
  Dunit = g/cm3
  Dvalue = 2.4
  Group = -> [O_element045,Na_element009,Si_element005,Ca_element011]
  conduct = 2
  density = 1
  expand = 3
  formula = G4_GLASS_PLATE
  name = G4_GLASS_PLATE
  specific = 4
FEATURE [App::DocumentObjectGroupPython] C_element049  label="C_element : 026"  # scripted group (container) (typed FeaturePython)
  n = 5
  ref = C_element
FEATURE [App::DocumentObjectGroupPython] H_element042  label="H_element : 021"  # scripted group (container) (typed FeaturePython)
  n = 10
  ref = H_element
FEATURE [App::DocumentObjectGroupPython] N_element019  label="N_element : 2"  # scripted group (container) (typed FeaturePython)
  n = 2
  ref = N_element
FEATURE [App::DocumentObjectGroupPython] O_element046  label="O_element : 022"  # scripted group (container) (typed FeaturePython)
  n = 3
  ref = O_element
FEATURE [App::DocumentObjectGroupPython] G4_GLUTAMINE  # scripted group (container) (typed FeaturePython)
  Dunit = g/cm3
  Dvalue = 1.46
  Group = -> [C_element049,H_element042,N_element019,O_element046]
  conduct = 2
  density = 1
  expand = 3
  formula = G4_GLUTAMINE
  name = G4_GLUTAMINE
  specific = 4
FEATURE [App::DocumentObjectGroupPython] C_element050  label="C_element : 027"  # scripted group (container) (typed FeaturePython)
  n = 3
  ref = C_element
FEATURE [App::DocumentObjectGroupPython] H_element043  label="H_element : 022"  # scripted group (container) (typed FeaturePython)
  n = 8
  ref = H_element
FEATURE [App::DocumentObjectGroupPython] O_element047  label="O_element : 023"  # scripted group (container) (typed FeaturePython)
  n = 3
  ref = O_element
FEATURE [App::DocumentObjectGroupPython] G4_GLYCEROL  # scripted group (container) (typed FeaturePython)
  Dunit = g/cm3
  Dvalue = 1.2613
  Group = -> [C_element050,H_element043,O_element047]
  conduct = 2
  density = 1
  expand = 3
  formula = G4_GLYCEROL
  name = G4_GLYCEROL
  specific = 4
FEATURE [App::DocumentObjectGroupPython] C_element051  label="C_element : 028"  # scripted group (container) (typed FeaturePython)
  n = 5
  ref = C_element
FEATURE [App::DocumentObjectGroupPython] H_element044  label="H_element : 023"  # scripted group (container) (typed FeaturePython)
  n = 5
  ref = H_element
FEATURE [App::DocumentObjectGroupPython] N_element020  label="N_element : 009"  # scripted group (container) (typed FeaturePython)
  n = 5
  ref = N_element
FEATURE [App::DocumentObjectGroupPython] O_element048  label="O_element : 024"  # scripted group (container) (typed FeaturePython)
  n = 1
  ref = O_element
FEATURE [App::DocumentObjectGroupPython] G4_GUANINE  # scripted group (container) (typed FeaturePython)
  Dunit = g/cm3
  Dvalue = 2.2
  Group = -> [C_element051,H_element044,N_element020,O_element048]
  conduct = 2
  density = 1
  expand = 3
  formula = G4_GUANINE
  name = G4_GUANINE
  specific = 4
FEATURE [App::DocumentObjectGroupPython] Ca_element012  label="Ca_element : 006"  # scripted group (container) (typed FeaturePython)
  n = 1
  ref = Ca_element
FEATURE [App::DocumentObjectGroupPython] S_element014  label="S_element : 005"  # scripted group (container) (typed FeaturePython)
  n = 1
  ref = S_element
FEATURE [App::DocumentObjectGroupPython] O_element049  label="O_element : 6"  # scripted group (container) (typed FeaturePython)
  n = 6
  ref = O_element
FEATURE [App::DocumentObjectGroupPython] H_element045  label="H_element : 024"  # scripted group (container) (typed FeaturePython)
  n = 4
  ref = H_element
FEATURE [App::DocumentObjectGroupPython] G4_GYPSUM  # scripted group (container) (typed FeaturePython)
  Dunit = g/cm3
  Dvalue = 2.32
  Group = -> [Ca_element012,S_element014,O_element049,H_element045]
  conduct = 2
  density = 1
  expand = 3
  formula = G4_GYPSUM
  name = G4_GYPSUM
  specific = 4
FEATURE [App::DocumentObjectGroupPython] C_element052  label="C_element : 7"  # scripted group (container) (typed FeaturePython)
  n = 7
  ref = C_element
FEATURE [App::DocumentObjectGroupPython] H_element046  label="H_element : 16"  # scripted group (container) (typed FeaturePython)
  n = 16
  ref = H_element
FEATURE [App::DocumentObjectGroupPython] G4_N_HEPTANE  label="G4_N-HEPTANE"  # scripted group (container) (typed FeaturePython)
  Dunit = g/cm3
  Dvalue = 0.68376
  Group = -> [C_element052,H_element046]
  conduct = 2
  density = 1
  expand = 3
  formula = G4_N-HEPTANE
  name = G4_N-HEPTANE
  specific = 4
FEATURE [App::DocumentObjectGroupPython] C_element053  label="C_element : 029"  # scripted group (container) (typed FeaturePython)
  n = 6
  ref = C_element
FEATURE [App::DocumentObjectGroupPython] H_element047  label="H_element : 14"  # scripted group (container) (typed FeaturePython)
  n = 14
  ref = H_element
FEATURE [App::DocumentObjectGroupPython] G4_N_HEXANE  label="G4_N-HEXANE"  # scripted group (container) (typed FeaturePython)
  Dunit = g/cm3
  Dvalue = 0.6603
  Group = -> [C_element053,H_element047]
  conduct = 2
  density = 1
  expand = 3
  formula = G4_N-HEXANE
  name = G4_N-HEXANE
  specific = 4
FEATURE [App::DocumentObjectGroupPython] C_element054  label="C_element : 22"  # scripted group (container) (typed FeaturePython)
  n = 22
  ref = C_element
FEATURE [App::DocumentObjectGroupPython] H_element048  label="H_element : 025"  # scripted group (container) (typed FeaturePython)
  n = 10
  ref = H_element
FEATURE [App::DocumentObjectGroupPython] N_element021  label="N_element : 010"  # scripted group (container) (typed FeaturePython)
  n = 2
  ref = N_element
FEATURE [App::DocumentObjectGroupPython] O_element050  label="O_element : 025"  # scripted group (container) (typed FeaturePython)
  n = 5
  ref = O_element
FEATURE [App::DocumentObjectGroupPython] G4_KAPTON  # scripted group (container) (typed FeaturePython)
  Dunit = g/cm3
  Dvalue = 1.42
  Group = -> [C_element054,H_element048,N_element021,O_element050]
  conduct = 2
  density = 1
  expand = 3
  formula = G4_KAPTON
  name = G4_KAPTON
  specific = 4
FEATURE [App::DocumentObjectGroupPython] La_element001  label="La_element : 1"  # scripted group (container) (typed FeaturePython)
  n = 1
  ref = La_element
FEATURE [App::DocumentObjectGroupPython] Br_element003  label="Br_element : 002"  # scripted group (container) (typed FeaturePython)
  n = 1
  ref = Br_element
FEATURE [App::DocumentObjectGroupPython] O_element051  label="O_element : 026"  # scripted group (container) (typed FeaturePython)
  n = 1
  ref = O_element
FEATURE [App::DocumentObjectGroupPython] G4_LANTHANUM_OXYBROMIDE  # scripted group (container) (typed FeaturePython)
  Dunit = g/cm3
  Dvalue = 6.28
  Group = -> [La_element001,Br_element003,O_element051]
  conduct = 2
  density = 1
  expand = 3
  formula = G4_LANTHANUM_OXYBROMIDE
  name = G4_LANTHANUM_OXYBROMIDE
  specific = 4
FEATURE [App::DocumentObjectGroupPython] La_element002  label="La_element : 2"  # scripted group (container) (typed FeaturePython)
  n = 2
  ref = La_element
FEATURE [App::DocumentObjectGroupPython] O_element052  label="O_element : 027"  # scripted group (container) (typed FeaturePython)
  n = 2
  ref = O_element
FEATURE [App::DocumentObjectGroupPython] S_element015  label="S_element : 006"  # scripted group (container) (typed FeaturePython)
  n = 1
  ref = S_element
FEATURE [App::DocumentObjectGroupPython] G4_LANTHANUM_OXYSULFIDE  # scripted group (container) (typed FeaturePython)
  Dunit = g/cm3
  Dvalue = 5.86
  Group = -> [La_element002,O_element052,S_element015]
  conduct = 2
  density = 1
  expand = 3
  formula = G4_LANTHANUM_OXYSULFIDE
  name = G4_LANTHANUM_OXYSULFIDE
  specific = 4
FEATURE [App::DocumentObjectGroupPython] O_element053  label="O_element : 0.072"  # scripted group (container) (typed FeaturePython)
  n = 0.071682
FEATURE [App::DocumentObjectGroupPython] Pb_element002  label="Pb_element : 0.928"  # scripted group (container) (typed FeaturePython)
  n = 0.928318
FEATURE [App::DocumentObjectGroupPython] G4_LEAD_OXIDE  # scripted group (container) (typed FeaturePython)
  Dunit = g/cm3
  Dvalue = 9.53
  Group = -> [O_element053,Pb_element002]
  conduct = 2
  density = 1
  expand = 3
  formula = G4_LEAD_OXIDE
  name = G4_LEAD_OXIDE
  specific = 4
FEATURE [App::DocumentObjectGroupPython] Li_element001  label="Li_element : 1"  # scripted group (container) (typed FeaturePython)
  n = 1
  ref = Li_element
FEATURE [App::DocumentObjectGroupPython] N_element022  label="N_element : 011"  # scripted group (container) (typed FeaturePython)
  n = 1
  ref = N_element
FEATURE [App::DocumentObjectGroupPython] H_element049  label="H_element : 026"  # scripted group (container) (typed FeaturePython)
  n = 2
  ref = H_element
FEATURE [App::DocumentObjectGroupPython] G4_LITHIUM_AMIDE  # scripted group (container) (typed FeaturePython)
  Dunit = g/cm3
  Dvalue = 1.178
  Group = -> [Li_element001,N_element022,H_element049]
  conduct = 2
  density = 1
  expand = 3
  formula = G4_LITHIUM_AMIDE
  name = G4_LITHIUM_AMIDE
  specific = 4
FEATURE [App::DocumentObjectGroupPython] Li_element002  label="Li_element : 2"  # scripted group (container) (typed FeaturePython)
  n = 2
  ref = Li_element
FEATURE [App::DocumentObjectGroupPython] C_element055  label="C_element : 030"  # scripted group (container) (typed FeaturePython)
  n = 1
  ref = C_element
FEATURE [App::DocumentObjectGroupPython] O_element054  label="O_element : 028"  # scripted group (container) (typed FeaturePython)
  n = 3
  ref = O_element
FEATURE [App::DocumentObjectGroupPython] G4_LITHIUM_CARBONATE  # scripted group (container) (typed FeaturePython)
  Dunit = g/cm3
  Dvalue = 2.11
  Group = -> [Li_element002,C_element055,O_element054]
  conduct = 2
  density = 1
  expand = 3
  formula = G4_LITHIUM_CARBONATE
  name = G4_LITHIUM_CARBONATE
  specific = 4
FEATURE [App::DocumentObjectGroupPython] Li_element003  label="Li_element : 003"  # scripted group (container) (typed FeaturePython)
  n = 1
  ref = Li_element
FEATURE [App::DocumentObjectGroupPython] F_element012  label="F_element : 004"  # scripted group (container) (typed FeaturePython)
  n = 1
  ref = F_element
FEATURE [App::DocumentObjectGroupPython] G4_LITHIUM_FLUORIDE  # scripted group (container) (typed FeaturePython)
  Dunit = g/cm3
  Dvalue = 2.635
  Group = -> [Li_element003,F_element012]
  conduct = 2
  density = 1
  expand = 3
  formula = G4_LITHIUM_FLUORIDE
  name = G4_LITHIUM_FLUORIDE
  specific = 4
FEATURE [App::DocumentObjectGroupPython] Li_element004  label="Li_element : 004"  # scripted group (container) (typed FeaturePython)
  n = 1
  ref = Li_element
FEATURE [App::DocumentObjectGroupPython] H_element050  label="H_element : 027"  # scripted group (container) (typed FeaturePython)
  n = 1
  ref = H_element
FEATURE [App::DocumentObjectGroupPython] G4_LITHIUM_HYDRIDE  # scripted group (container) (typed FeaturePython)
  Dunit = g/cm3
  Dvalue = 0.82
  Group = -> [Li_element004,H_element050]
  conduct = 2
  density = 1
  expand = 3
  formula = G4_LITHIUM_HYDRIDE
  name = G4_LITHIUM_HYDRIDE
  specific = 4
FEATURE [App::DocumentObjectGroupPython] Li_element005  label="Li_element : 005"  # scripted group (container) (typed FeaturePython)
  n = 1
  ref = Li_element
FEATURE [App::DocumentObjectGroupPython] I_element003  label="I_element : 002"  # scripted group (container) (typed FeaturePython)
  n = 1
  ref = I_element
FEATURE [App::DocumentObjectGroupPython] G4_LITHIUM_IODIDE  # scripted group (container) (typed FeaturePython)
  Dunit = g/cm3
  Dvalue = 3.494
  Group = -> [Li_element005,I_element003]
  conduct = 2
  density = 1
  expand = 3
  formula = G4_LITHIUM_IODIDE
  name = G4_LITHIUM_IODIDE
  specific = 4
FEATURE [App::DocumentObjectGroupPython] Li_element006  label="Li_element : 006"  # scripted group (container) (typed FeaturePython)
  n = 2
  ref = Li_element
FEATURE [App::DocumentObjectGroupPython] O_element055  label="O_element : 029"  # scripted group (container) (typed FeaturePython)
  n = 1
  ref = O_element
FEATURE [App::DocumentObjectGroupPython] G4_LITHIUM_OXIDE  # scripted group (container) (typed FeaturePython)
  Dunit = g/cm3
  Dvalue = 2.013
  Group = -> [Li_element006,O_element055]
  conduct = 2
  density = 1
  expand = 3
  formula = G4_LITHIUM_OXIDE
  name = G4_LITHIUM_OXIDE
  specific = 4
FEATURE [App::DocumentObjectGroupPython] Li_element007  label="Li_element : 007"  # scripted group (container) (typed FeaturePython)
  n = 2
  ref = Li_element
FEATURE [App::DocumentObjectGroupPython] B_element005  label="B_element : 005"  # scripted group (container) (typed FeaturePython)
  n = 4
  ref = B_element
FEATURE [App::DocumentObjectGroupPython] O_element056  label="O_element : 7"  # scripted group (container) (typed FeaturePython)
  n = 7
  ref = O_element
FEATURE [App::DocumentObjectGroupPython] G4_LITHIUM_TETRABORATE  # scripted group (container) (typed FeaturePython)
  Dunit = g/cm3
  Dvalue = 2.44
  Group = -> [Li_element007,B_element005,O_element056]
  conduct = 2
  density = 1
  expand = 3
  formula = G4_LITHIUM_TETRABORATE
  name = G4_LITHIUM_TETRABORATE
  specific = 4
FEATURE [App::DocumentObjectGroupPython] H_element051  label="H_element : 0.105"  # scripted group (container) (typed FeaturePython)
  n = 0.105
FEATURE [App::DocumentObjectGroupPython] C_element056  label="C_element : 0.083"  # scripted group (container) (typed FeaturePython)
  n = 0.083
FEATURE [App::DocumentObjectGroupPython] N_element023  label="N_element : 0.023"  # scripted group (container) (typed FeaturePython)
  n = 0.023
FEATURE [App::DocumentObjectGroupPython] O_element057  label="O_element : 0.779"  # scripted group (container) (typed FeaturePython)
  n = 0.779
FEATURE [App::DocumentObjectGroupPython] Na_element010  label="Na_element : 0.097"  # scripted group (container) (typed FeaturePython)
  n = 0.002
FEATURE [App::DocumentObjectGroupPython] P_element006  label="P_element : 0.105"  # scripted group (container) (typed FeaturePython)
  n = 0.001
FEATURE [App::DocumentObjectGroupPython] S_element016  label="S_element : 0.017"  # scripted group (container) (typed FeaturePython)
  n = 0.002
FEATURE [App::DocumentObjectGroupPython] Cl_element014  label="Cl_element : 0.587"  # scripted group (container) (typed FeaturePython)
  n = 0.003
FEATURE [App::DocumentObjectGroupPython] K_element005  label="K_element : 0.015"  # scripted group (container) (typed FeaturePython)
  n = 0.002
FEATURE [App::DocumentObjectGroupPython] G4_LUNG_ICRP  # scripted group (container) (typed FeaturePython)
  Dunit = g/cm3
  Dvalue = 1.04
  Group = -> [H_element051,C_element056,N_element023,O_element057,Na_element010,P_element006,S_element016,Cl_element014,K_element005]
  conduct = 2
  density = 1
  expand = 3
  formula = G4_LUNG_ICRP
  name = G4_LUNG_ICRP
  specific = 4
FEATURE [App::DocumentObjectGroupPython] H_element052  label="H_element : 0.116"  # scripted group (container) (typed FeaturePython)
  n = 0.114318
FEATURE [App::DocumentObjectGroupPython] C_element057  label="C_element : 0.656"  # scripted group (container) (typed FeaturePython)
  n = 0.655824
FEATURE [App::DocumentObjectGroupPython] O_element058  label="O_element : 0.092"  # scripted group (container) (typed FeaturePython)
  n = 0.0921831
FEATURE [App::DocumentObjectGroupPython] Mg_element004  label="Mg_element : 0.135"  # scripted group (container) (typed FeaturePython)
  n = 0.134792
FEATURE [App::DocumentObjectGroupPython] Ca_element013  label="Ca_element : 0.003"  # scripted group (container) (typed FeaturePython)
  n = 0.002883
FEATURE [App::DocumentObjectGroupPython] G4_M3_WAX  # scripted group (container) (typed FeaturePython)
  Dunit = g/cm3
  Dvalue = 1.05
  Group = -> [H_element052,C_element057,O_element058,Mg_element004,Ca_element013]
  conduct = 2
  density = 1
  expand = 3
  formula = G4_M3_WAX
  name = G4_M3_WAX
  specific = 4
FEATURE [App::DocumentObjectGroupPython] Mg_element005  label="Mg_element : 1"  # scripted group (container) (typed FeaturePython)
  n = 1
  ref = Mg_element
FEATURE [App::DocumentObjectGroupPython] C_element058  label="C_element : 031"  # scripted group (container) (typed FeaturePython)
  n = 1
  ref = C_element
FEATURE [App::DocumentObjectGroupPython] O_element059  label="O_element : 030"  # scripted group (container) (typed FeaturePython)
  n = 3
  ref = O_element
FEATURE [App::DocumentObjectGroupPython] G4_MAGNESIUM_CARBONATE  # scripted group (container) (typed FeaturePython)
  Dunit = g/cm3
  Dvalue = 2.958
  Group = -> [Mg_element005,C_element058,O_element059]
  conduct = 2
  density = 1
  expand = 3
  formula = G4_MAGNESIUM_CARBONATE
  name = G4_MAGNESIUM_CARBONATE
  specific = 4
FEATURE [App::DocumentObjectGroupPython] Mg_element006  label="Mg_element : 002"  # scripted group (container) (typed FeaturePython)
  n = 1
  ref = Mg_element
FEATURE [App::DocumentObjectGroupPython] F_element013  label="F_element : 005"  # scripted group (container) (typed FeaturePython)
  n = 2
  ref = F_element
FEATURE [App::DocumentObjectGroupPython] G4_MAGNESIUM_FLUORIDE  # scripted group (container) (typed FeaturePython)
  Dunit = g/cm3
  Dvalue = 3
  Group = -> [Mg_element006,F_element013]
  conduct = 2
  density = 1
  expand = 3
  formula = G4_MAGNESIUM_FLUORIDE
  name = G4_MAGNESIUM_FLUORIDE
  specific = 4
FEATURE [App::DocumentObjectGroupPython] Mg_element007  label="Mg_element : 003"  # scripted group (container) (typed FeaturePython)
  n = 1
  ref = Mg_element
FEATURE [App::DocumentObjectGroupPython] O_element060  label="O_element : 031"  # scripted group (container) (typed FeaturePython)
  n = 1
  ref = O_element
FEATURE [App::DocumentObjectGroupPython] G4_MAGNESIUM_OXIDE  # scripted group (container) (typed FeaturePython)
  Dunit = g/cm3
  Dvalue = 3.58
  Group = -> [Mg_element007,O_element060]
  conduct = 2
  density = 1
  expand = 3
  formula = G4_MAGNESIUM_OXIDE
  name = G4_MAGNESIUM_OXIDE
  specific = 4
FEATURE [App::DocumentObjectGroupPython] Mg_element008  label="Mg_element : 004"  # scripted group (container) (typed FeaturePython)
  n = 1
  ref = Mg_element
FEATURE [App::DocumentObjectGroupPython] B_element006  label="B_element : 006"  # scripted group (container) (typed FeaturePython)
  n = 4
  ref = B_element
FEATURE [App::DocumentObjectGroupPython] O_element061  label="O_element : 032"  # scripted group (container) (typed FeaturePython)
  n = 7
  ref = O_element
FEATURE [App::DocumentObjectGroupPython] G4_MAGNESIUM_TETRABORATE  # scripted group (container) (typed FeaturePython)
  Dunit = g/cm3
  Dvalue = 2.53
  Group = -> [Mg_element008,B_element006,O_element061]
  conduct = 2
  density = 1
  expand = 3
  formula = G4_MAGNESIUM_TETRABORATE
  name = G4_MAGNESIUM_TETRABORATE
  specific = 4
FEATURE [App::DocumentObjectGroupPython] Hg_element001  label="Hg_element : 1"  # scripted group (container) (typed FeaturePython)
  n = 1
  ref = Hg_element
FEATURE [App::DocumentObjectGroupPython] I_element004  label="I_element : 2"  # scripted group (container) (typed FeaturePython)
  n = 2
  ref = I_element
FEATURE [App::DocumentObjectGroupPython] G4_MERCURIC_IODIDE  # scripted group (container) (typed FeaturePython)
  Dunit = g/cm3
  Dvalue = 6.36
  Group = -> [Hg_element001,I_element004]
  conduct = 2
  density = 1
  expand = 3
  formula = G4_MERCURIC_IODIDE
  name = G4_MERCURIC_IODIDE
  specific = 4
FEATURE [App::DocumentObjectGroupPython] C_element059  label="C_element : 032"  # scripted group (container) (typed FeaturePython)
  n = 1
  ref = C_element
FEATURE [App::DocumentObjectGroupPython] H_element053  label="H_element : 028"  # scripted group (container) (typed FeaturePython)
  n = 4
  ref = H_element
FEATURE [App::DocumentObjectGroupPython] G4_METHANE  # scripted group (container) (typed FeaturePython)
  Dunit = g/cm3
  Dvalue = 0.000667151
  Group = -> [C_element059,H_element053]
  conduct = 2
  density = 1
  expand = 3
  formula = G4_METHANE
  name = G4_METHANE
  specific = 4
FEATURE [App::DocumentObjectGroupPython] C_element060  label="C_element : 033"  # scripted group (container) (typed FeaturePython)
  n = 1
  ref = C_element
FEATURE [App::DocumentObjectGroupPython] H_element054  label="H_element : 029"  # scripted group (container) (typed FeaturePython)
  n = 4
  ref = H_element
FEATURE [App::DocumentObjectGroupPython] O_element062  label="O_element : 033"  # scripted group (container) (typed FeaturePython)
  n = 1
  ref = O_element
FEATURE [App::DocumentObjectGroupPython] G4_METHANOL  # scripted group (container) (typed FeaturePython)
  Dunit = g/cm3
  Dvalue = 0.7914
  Group = -> [C_element060,H_element054,O_element062]
  conduct = 2
  density = 1
  expand = 3
  formula = G4_METHANOL
  name = G4_METHANOL
  specific = 4
FEATURE [App::DocumentObjectGroupPython] H_element055  label="H_element : 0.134"  # scripted group (container) (typed FeaturePython)
  n = 0.13404
FEATURE [App::DocumentObjectGroupPython] C_element061  label="C_element : 0.778"  # scripted group (container) (typed FeaturePython)
  n = 0.77796
FEATURE [App::DocumentObjectGroupPython] O_element063  label="O_element : 0.035"  # scripted group (container) (typed FeaturePython)
  n = 0.03502
FEATURE [App::DocumentObjectGroupPython] Mg_element009  label="Mg_element : 0.039"  # scripted group (container) (typed FeaturePython)
  n = 0.038594
FEATURE [App::DocumentObjectGroupPython] Ti_element002  label="Ti_element : 0.014"  # scripted group (container) (typed FeaturePython)
  n = 0.014386
FEATURE [App::DocumentObjectGroupPython] G4_MIX_D_WAX  # scripted group (container) (typed FeaturePython)
  Dunit = g/cm3
  Dvalue = 0.99
  Group = -> [H_element055,C_element061,O_element063,Mg_element009,Ti_element002]
  conduct = 2
  density = 1
  expand = 3
  formula = G4_MIX_D_WAX
  name = G4_MIX_D_WAX
  specific = 4
FEATURE [App::DocumentObjectGroupPython] H_element056  label="H_element : 0.135"  # scripted group (container) (typed FeaturePython)
  n = 0.081192
FEATURE [App::DocumentObjectGroupPython] C_element062  label="C_element : 0.583"  # scripted group (container) (typed FeaturePython)
  n = 0.583442
FEATURE [App::DocumentObjectGroupPython] N_element024  label="N_element : 0.018"  # scripted group (container) (typed FeaturePython)
  n = 0.017798
FEATURE [App::DocumentObjectGroupPython] O_element064  label="O_element : 0.186"  # scripted group (container) (typed FeaturePython)
  n = 0.186381
FEATURE [App::DocumentObjectGroupPython] Mg_element010  label="Mg_element : 0.130"  # scripted group (container) (typed FeaturePython)
  n = 0.130287
FEATURE [App::DocumentObjectGroupPython] Cl_element015  label="Cl_element : 0.588"  # scripted group (container) (typed FeaturePython)
  n = 0.0009
FEATURE [App::DocumentObjectGroupPython] G4_MS20_TISSUE  # scripted group (container) (typed FeaturePython)
  Dunit = g/cm3
  Dvalue = 1
  Group = -> [H_element056,C_element062,N_element024,O_element064,Mg_element010,Cl_element015]
  conduct = 2
  density = 1
  expand = 3
  formula = G4_MS20_TISSUE
  name = G4_MS20_TISSUE
  specific = 4
FEATURE [App::DocumentObjectGroupPython] H_element057  label="H_element : 0.136"  # scripted group (container) (typed FeaturePython)
  n = 0.102
FEATURE [App::DocumentObjectGroupPython] C_element063  label="C_element : 0.143"  # scripted group (container) (typed FeaturePython)
  n = 0.143
FEATURE [App::DocumentObjectGroupPython] N_element025  label="N_element : 0.034"  # scripted group (container) (typed FeaturePython)
  n = 0.034
FEATURE [App::DocumentObjectGroupPython] O_element065  label="O_element : 0.710"  # scripted group (container) (typed FeaturePython)
  n = 0.71
FEATURE [App::DocumentObjectGroupPython] Na_element011  label="Na_element : 0.098"  # scripted group (container) (typed FeaturePython)
  n = 0.001
FEATURE [App::DocumentObjectGroupPython] P_element007  label="P_element : 0.002"  # scripted group (container) (typed FeaturePython)
  n = 0.002
FEATURE [App::DocumentObjectGroupPython] S_element017  label="S_element : 0.018"  # scripted group (container) (typed FeaturePython)
  n = 0.003
FEATURE [App::DocumentObjectGroupPython] Cl_element016  label="Cl_element : 0.589"  # scripted group (container) (typed FeaturePython)
  n = 0.001
FEATURE [App::DocumentObjectGroupPython] K_element006  label="K_element : 0.004"  # scripted group (container) (typed FeaturePython)
  n = 0.004
FEATURE [App::DocumentObjectGroupPython] G4_MUSCLE_SKELETAL_ICRP  # scripted group (container) (typed FeaturePython)
  Dunit = g/cm3
  Dvalue = 1.05
  Group = -> [H_element057,C_element063,N_element025,O_element065,Na_element011,P_element007,S_element017,Cl_element016,K_element006]
  conduct = 2
  density = 1
  expand = 3
  formula = G4_MUSCLE_SKELETAL_ICRP
  name = G4_MUSCLE_SKELETAL_ICRP
  specific = 4
FEATURE [App::DocumentObjectGroupPython] H_element058  label="H_element : 0.137"  # scripted group (container) (typed FeaturePython)
  n = 0.102102
FEATURE [App::DocumentObjectGroupPython] C_element064  label="C_element : 0.123"  # scripted group (container) (typed FeaturePython)
  n = 0.123123
FEATURE [App::DocumentObjectGroupPython] N_element026  label="N_element : 0.756"  # scripted group (container) (typed FeaturePython)
  n = 0.035035
FEATURE [App::DocumentObjectGroupPython] O_element066  label="O_element : 0.730"  # scripted group (container) (typed FeaturePython)
  n = 0.72973
FEATURE [App::DocumentObjectGroupPython] Na_element012  label="Na_element : 0.099"  # scripted group (container) (typed FeaturePython)
  n = 0.001001
FEATURE [App::DocumentObjectGroupPython] P_element008  label="P_element : 0.106"  # scripted group (container) (typed FeaturePython)
  n = 0.002002
FEATURE [App::DocumentObjectGroupPython] S_element018  label="S_element : 0.019"  # scripted group (container) (typed FeaturePython)
  n = 0.004004
FEATURE [App::DocumentObjectGroupPython] K_element007  label="K_element : 0.016"  # scripted group (container) (typed FeaturePython)
  n = 0.003003
FEATURE [App::DocumentObjectGroupPython] G4_MUSCLE_STRIATED_ICRU  # scripted group (container) (typed FeaturePython)
  Dunit = g/cm3
  Dvalue = 1.04
  Group = -> [H_element058,C_element064,N_element026,O_element066,Na_element012,P_element008,S_element018,K_element007]
  conduct = 2
  density = 1
  expand = 3
  formula = G4_MUSCLE_STRIATED_ICRU
  name = G4_MUSCLE_STRIATED_ICRU
  specific = 4
FEATURE [App::DocumentObjectGroupPython] H_element059  label="H_element : 0.098"  # scripted group (container) (typed FeaturePython)
  n = 0.0982341
FEATURE [App::DocumentObjectGroupPython] C_element065  label="C_element : 0.156"  # scripted group (container) (typed FeaturePython)
  n = 0.156214
FEATURE [App::DocumentObjectGroupPython] N_element027  label="N_element : 0.757"  # scripted group (container) (typed FeaturePython)
  n = 0.035451
FEATURE [App::DocumentObjectGroupPython] O_element067  label="O_element : 0.880"  # scripted group (container) (typed FeaturePython)
  n = 0.710101
FEATURE [App::DocumentObjectGroupPython] G4_MUSCLE_WITH_SUCROSE  # scripted group (container) (typed FeaturePython)
  Dunit = g/cm3
  Dvalue = 1.11
  Group = -> [H_element059,C_element065,N_element027,O_element067]
  conduct = 2
  density = 1
  expand = 3
  formula = G4_MUSCLE_WITH_SUCROSE
  name = G4_MUSCLE_WITH_SUCROSE
  specific = 4
FEATURE [App::DocumentObjectGroupPython] H_element060  label="H_element : 0.138"  # scripted group (container) (typed FeaturePython)
  n = 0.101969
FEATURE [App::DocumentObjectGroupPython] C_element066  label="C_element : 0.120"  # scripted group (container) (typed FeaturePython)
  n = 0.120058
FEATURE [App::DocumentObjectGroupPython] N_element028  label="N_element : 0.758"  # scripted group (container) (typed FeaturePython)
  n = 0.035451
FEATURE [App::DocumentObjectGroupPython] O_element068  label="O_element : 0.743"  # scripted group (container) (typed FeaturePython)
  n = 0.742522
FEATURE [App::DocumentObjectGroupPython] G4_MUSCLE_WITHOUT_SUCROSE  # scripted group (container) (typed FeaturePython)
  Dunit = g/cm3
  Dvalue = 1.07
  Group = -> [H_element060,C_element066,N_element028,O_element068]
  conduct = 2
  density = 1
  expand = 3
  formula = G4_MUSCLE_WITHOUT_SUCROSE
  name = G4_MUSCLE_WITHOUT_SUCROSE
  specific = 4
FEATURE [App::DocumentObjectGroupPython] C_element067  label="C_element : 10"  # scripted group (container) (typed FeaturePython)
  n = 10
  ref = C_element
FEATURE [App::DocumentObjectGroupPython] H_element061  label="H_element : 030"  # scripted group (container) (typed FeaturePython)
  n = 8
  ref = H_element
FEATURE [App::DocumentObjectGroupPython] G4_NAPHTHALENE  # scripted group (container) (typed FeaturePython)
  Dunit = g/cm3
  Dvalue = 1.145
  Group = -> [C_element067,H_element061]
  conduct = 2
  density = 1
  expand = 3
  formula = G4_NAPHTHALENE
  name = G4_NAPHTHALENE
  specific = 4
FEATURE [App::DocumentObjectGroupPython] C_element068  label="C_element : 034"  # scripted group (container) (typed FeaturePython)
  n = 6
  ref = C_element
FEATURE [App::DocumentObjectGroupPython] H_element062  label="H_element : 031"  # scripted group (container) (typed FeaturePython)
  n = 5
  ref = H_element
FEATURE [App::DocumentObjectGroupPython] N_element029  label="N_element : 012"  # scripted group (container) (typed FeaturePython)
  n = 1
  ref = N_element
FEATURE [App::DocumentObjectGroupPython] O_element069  label="O_element : 034"  # scripted group (container) (typed FeaturePython)
  n = 2
  ref = O_element
FEATURE [App::DocumentObjectGroupPython] G4_NITROBENZENE  # scripted group (container) (typed FeaturePython)
  Dunit = g/cm3
  Dvalue = 1.19867
  Group = -> [C_element068,H_element062,N_element029,O_element069]
  conduct = 2
  density = 1
  expand = 3
  formula = G4_NITROBENZENE
  name = G4_NITROBENZENE
  specific = 4
FEATURE [App::DocumentObjectGroupPython] N_element030  label="N_element : 013"  # scripted group (container) (typed FeaturePython)
  n = 2
  ref = N_element
FEATURE [App::DocumentObjectGroupPython] O_element070  label="O_element : 035"  # scripted group (container) (typed FeaturePython)
  n = 1
  ref = O_element
FEATURE [App::DocumentObjectGroupPython] G4_NITROUS_OXIDE  # scripted group (container) (typed FeaturePython)
  Dunit = g/cm3
  Dvalue = 0.00183094
  Group = -> [N_element030,O_element070]
  conduct = 2
  density = 1
  expand = 3
  formula = G4_NITROUS_OXIDE
  name = G4_NITROUS_OXIDE
  specific = 4
FEATURE [App::DocumentObjectGroupPython] H_element063  label="H_element : 0.104"  # scripted group (container) (typed FeaturePython)
  n = 0.103509
FEATURE [App::DocumentObjectGroupPython] C_element069  label="C_element : 0.648"  # scripted group (container) (typed FeaturePython)
  n = 0.648416
FEATURE [App::DocumentObjectGroupPython] N_element031  label="N_element : 0.100"  # scripted group (container) (typed FeaturePython)
  n = 0.0995361
FEATURE [App::DocumentObjectGroupPython] O_element071  label="O_element : 0.149"  # scripted group (container) (typed FeaturePython)
  n = 0.148539
FEATURE [App::DocumentObjectGroupPython] G4_NYLON_8062  label="G4_NYLON-8062"  # scripted group (container) (typed FeaturePython)
  Dunit = g/cm3
  Dvalue = 1.08
  Group = -> [H_element063,C_element069,N_element031,O_element071]
  conduct = 2
  density = 1
  expand = 3
  formula = G4_NYLON-8062
  name = G4_NYLON-8062
  specific = 4
FEATURE [App::DocumentObjectGroupPython] C_element070  label="C_element : 035"  # scripted group (container) (typed FeaturePython)
  n = 6
  ref = C_element
FEATURE [App::DocumentObjectGroupPython] H_element064  label="H_element : 11"  # scripted group (container) (typed FeaturePython)
  n = 11
  ref = H_element
FEATURE [App::DocumentObjectGroupPython] N_element032  label="N_element : 014"  # scripted group (container) (typed FeaturePython)
  n = 1
  ref = N_element
FEATURE [App::DocumentObjectGroupPython] O_element072  label="O_element : 036"  # scripted group (container) (typed FeaturePython)
  n = 1
  ref = O_element
FEATURE [App::DocumentObjectGroupPython] G4_NYLON_6_6  label="G4_NYLON-6-6"  # scripted group (container) (typed FeaturePython)
  Dunit = g/cm3
  Dvalue = 1.14
  Group = -> [C_element070,H_element064,N_element032,O_element072]
  conduct = 2
  density = 1
  expand = 3
  formula = G4_NYLON-6-6
  name = G4_NYLON-6-6
  specific = 4
FEATURE [App::DocumentObjectGroupPython] H_element065  label="H_element : 0.139"  # scripted group (container) (typed FeaturePython)
  n = 0.107062
FEATURE [App::DocumentObjectGroupPython] C_element071  label="C_element : 0.680"  # scripted group (container) (typed FeaturePython)
  n = 0.680449
FEATURE [App::DocumentObjectGroupPython] N_element033  label="N_element : 0.099"  # scripted group (container) (typed FeaturePython)
  n = 0.099189
FEATURE [App::DocumentObjectGroupPython] O_element073  label="O_element : 0.113"  # scripted group (container) (typed FeaturePython)
  n = 0.1133
FEATURE [App::DocumentObjectGroupPython] G4_NYLON_6_10  label="G4_NYLON-6-10"  # scripted group (container) (typed FeaturePython)
  Dunit = g/cm3
  Dvalue = 1.14
  Group = -> [H_element065,C_element071,N_element033,O_element073]
  conduct = 2
  density = 1
  expand = 3
  formula = G4_NYLON-6-10
  name = G4_NYLON-6-10
  specific = 4
FEATURE [App::DocumentObjectGroupPython] H_element066  label="H_element : 0.140"  # scripted group (container) (typed FeaturePython)
  n = 0.115476
FEATURE [App::DocumentObjectGroupPython] C_element072  label="C_element : 0.721"  # scripted group (container) (typed FeaturePython)
  n = 0.720818
FEATURE [App::DocumentObjectGroupPython] N_element034  label="N_element : 0.076"  # scripted group (container) (typed FeaturePython)
  n = 0.0764169
FEATURE [App::DocumentObjectGroupPython] O_element074  label="O_element : 0.087"  # scripted group (container) (typed FeaturePython)
  n = 0.0872889
FEATURE [App::DocumentObjectGroupPython] G4_NYLON_11_RILSAN  label="G4_NYLON-11_RILSAN"  # scripted group (container) (typed FeaturePython)
  Dunit = g/cm3
  Dvalue = 1.425
  Group = -> [H_element066,C_element072,N_element034,O_element074]
  conduct = 2
  density = 1
  expand = 3
  formula = G4_NYLON-11_RILSAN
  name = G4_NYLON-11_RILSAN
  specific = 4
FEATURE [App::DocumentObjectGroupPython] C_element073  label="C_element : 8"  # scripted group (container) (typed FeaturePython)
  n = 8
  ref = C_element
FEATURE [App::DocumentObjectGroupPython] H_element067  label="H_element : 18"  # scripted group (container) (typed FeaturePython)
  n = 18
  ref = H_element
FEATURE [App::DocumentObjectGroupPython] G4_OCTANE  # scripted group (container) (typed FeaturePython)
  Dunit = g/cm3
  Dvalue = 0.7026
  Group = -> [C_element073,H_element067]
  conduct = 2
  density = 1
  expand = 3
  formula = G4_OCTANE
  name = G4_OCTANE
  specific = 4
FEATURE [App::DocumentObjectGroupPython] C_element074  label="C_element : 25"  # scripted group (container) (typed FeaturePython)
  n = 25
  ref = C_element
FEATURE [App::DocumentObjectGroupPython] H_element068  label="H_element : 52"  # scripted group (container) (typed FeaturePython)
  n = 52
  ref = H_element
FEATURE [App::DocumentObjectGroupPython] G4_PARAFFIN  # scripted group (container) (typed FeaturePython)
  Dunit = g/cm3
  Dvalue = 0.93
  Group = -> [C_element074,H_element068]
  conduct = 2
  density = 1
  expand = 3
  formula = G4_PARAFFIN
  name = G4_PARAFFIN
  specific = 4
FEATURE [App::DocumentObjectGroupPython] C_element075  label="C_element : 036"  # scripted group (container) (typed FeaturePython)
  n = 5
  ref = C_element
FEATURE [App::DocumentObjectGroupPython] H_element069  label="H_element : 032"  # scripted group (container) (typed FeaturePython)
  n = 12
  ref = H_element
FEATURE [App::DocumentObjectGroupPython] G4_N_PENTANE  label="G4_N-PENTANE"  # scripted group (container) (typed FeaturePython)
  Dunit = g/cm3
  Dvalue = 0.6262
  Group = -> [C_element075,H_element069]
  conduct = 2
  density = 1
  expand = 3
  formula = G4_N-PENTANE
  name = G4_N-PENTANE
  specific = 4
FEATURE [App::DocumentObjectGroupPython] H_element070  label="H_element : 0.014"  # scripted group (container) (typed FeaturePython)
  n = 0.0141
FEATURE [App::DocumentObjectGroupPython] C_element076  label="C_element : 0.072"  # scripted group (container) (typed FeaturePython)
  n = 0.072261
FEATURE [App::DocumentObjectGroupPython] N_element035  label="N_element : 0.019"  # scripted group (container) (typed FeaturePython)
  n = 0.01932
FEATURE [App::DocumentObjectGroupPython] O_element075  label="O_element : 0.066"  # scripted group (container) (typed FeaturePython)
  n = 0.066101
FEATURE [App::DocumentObjectGroupPython] S_element019  label="S_element : 0.020"  # scripted group (container) (typed FeaturePython)
  n = 0.00189
FEATURE [App::DocumentObjectGroupPython] Br_element004  label="Br_element : 0.349"  # scripted group (container) (typed FeaturePython)
  n = 0.349103
FEATURE [App::DocumentObjectGroupPython] Ag_element001  label="Ag_element : 0.474"  # scripted group (container) (typed FeaturePython)
  n = 0.474105
FEATURE [App::DocumentObjectGroupPython] I_element005  label="I_element : 0.003"  # scripted group (container) (typed FeaturePython)
  n = 0.00312
FEATURE [App::DocumentObjectGroupPython] G4_PHOTO_EMULSION  # scripted group (container) (typed FeaturePython)
  Dunit = g/cm3
  Dvalue = 3.815
  Group = -> [H_element070,C_element076,N_element035,O_element075,S_element019,Br_element004,Ag_element001,I_element005]
  conduct = 2
  density = 1
  expand = 3
  formula = G4_PHOTO_EMULSION
  name = G4_PHOTO_EMULSION
  specific = 4
FEATURE [App::DocumentObjectGroupPython] C_element077  label="C_element : 9"  # scripted group (container) (typed FeaturePython)
  n = 9
  ref = C_element
FEATURE [App::DocumentObjectGroupPython] H_element071  label="H_element : 033"  # scripted group (container) (typed FeaturePython)
  n = 10
  ref = H_element
FEATURE [App::DocumentObjectGroupPython] G4_PLASTIC_SC_VINYLTOLUENE  # scripted group (container) (typed FeaturePython)
  Dunit = g/cm3
  Dvalue = 1.032
  Group = -> [C_element077,H_element071]
  conduct = 2
  density = 1
  expand = 3
  formula = G4_PLASTIC_SC_VINYLTOLUENE
  name = G4_PLASTIC_SC_VINYLTOLUENE
  specific = 4
FEATURE [App::DocumentObjectGroupPython] Pu_element001  label="Pu_element : 1"  # scripted group (container) (typed FeaturePython)
  n = 1
  ref = Pu_element
FEATURE [App::DocumentObjectGroupPython] O_element076  label="O_element : 037"  # scripted group (container) (typed FeaturePython)
  n = 2
  ref = O_element
FEATURE [App::DocumentObjectGroupPython] G4_PLUTONIUM_DIOXIDE  # scripted group (container) (typed FeaturePython)
  Dunit = g/cm3
  Dvalue = 11.46
  Group = -> [Pu_element001,O_element076]
  conduct = 2
  density = 1
  expand = 3
  formula = G4_PLUTONIUM_DIOXIDE
  name = G4_PLUTONIUM_DIOXIDE
  specific = 4
FEATURE [App::DocumentObjectGroupPython] C_element078  label="C_element : 037"  # scripted group (container) (typed FeaturePython)
  n = 3
  ref = C_element
FEATURE [App::DocumentObjectGroupPython] H_element072  label="H_element : 034"  # scripted group (container) (typed FeaturePython)
  n = 3
  ref = H_element
FEATURE [App::DocumentObjectGroupPython] N_element036  label="N_element : 015"  # scripted group (container) (typed FeaturePython)
  n = 1
  ref = N_element
FEATURE [App::DocumentObjectGroupPython] G4_POLYACRYLONITRILE  # scripted group (container) (typed FeaturePython)
  Dunit = g/cm3
  Dvalue = 1.17
  Group = -> [C_element078,H_element072,N_element036]
  conduct = 2
  density = 1
  expand = 3
  formula = G4_POLYACRYLONITRILE
  name = G4_POLYACRYLONITRILE
  specific = 4
FEATURE [App::DocumentObjectGroupPython] C_element079  label="C_element : 16"  # scripted group (container) (typed FeaturePython)
  n = 16
  ref = C_element
FEATURE [App::DocumentObjectGroupPython] H_element073  label="H_element : 035"  # scripted group (container) (typed FeaturePython)
  n = 14
  ref = H_element
FEATURE [App::DocumentObjectGroupPython] O_element077  label="O_element : 038"  # scripted group (container) (typed FeaturePython)
  n = 3
  ref = O_element
FEATURE [App::DocumentObjectGroupPython] G4_POLYCARBONATE  # scripted group (container) (typed FeaturePython)
  Dunit = g/cm3
  Dvalue = 1.2
  Group = -> [C_element079,H_element073,O_element077]
  conduct = 2
  density = 1
  expand = 3
  formula = G4_POLYCARBONATE
  name = G4_POLYCARBONATE
  specific = 4
FEATURE [App::DocumentObjectGroupPython] C_element080  label="C_element : 038"  # scripted group (container) (typed FeaturePython)
  n = 8
  ref = C_element
FEATURE [App::DocumentObjectGroupPython] H_element074  label="H_element : 036"  # scripted group (container) (typed FeaturePython)
  n = 7
  ref = H_element
FEATURE [App::DocumentObjectGroupPython] Cl_element017  label="Cl_element : 007"  # scripted group (container) (typed FeaturePython)
  n = 1
  ref = Cl_element
FEATURE [App::DocumentObjectGroupPython] G4_POLYCHLOROSTYRENE  # scripted group (container) (typed FeaturePython)
  Dunit = g/cm3
  Dvalue = 1.3
  Group = -> [C_element080,H_element074,Cl_element017]
  conduct = 2
  density = 1
  expand = 3
  formula = G4_POLYCHLOROSTYRENE
  name = G4_POLYCHLOROSTYRENE
  specific = 4
FEATURE [App::DocumentObjectGroupPython] C_element081  label="C_element : 039"  # scripted group (container) (typed FeaturePython)
  n = 1
  ref = C_element
FEATURE [App::DocumentObjectGroupPython] H_element075  label="H_element : 037"  # scripted group (container) (typed FeaturePython)
  n = 2
  ref = H_element
FEATURE [App::DocumentObjectGroupPython] G4_POLYETHYLENE  # scripted group (container) (typed FeaturePython)
  Dunit = g/cm3
  Dvalue = 0.94
  Group = -> [C_element081,H_element075]
  conduct = 2
  density = 1
  expand = 3
  formula = G4_POLYETHYLENE
  name = G4_POLYETHYLENE
  specific = 4
FEATURE [App::DocumentObjectGroupPython] C_element082  label="C_element : 040"  # scripted group (container) (typed FeaturePython)
  n = 10
  ref = C_element
FEATURE [App::DocumentObjectGroupPython] H_element076  label="H_element : 038"  # scripted group (container) (typed FeaturePython)
  n = 8
  ref = H_element
FEATURE [App::DocumentObjectGroupPython] O_element078  label="O_element : 039"  # scripted group (container) (typed FeaturePython)
  n = 4
  ref = O_element
FEATURE [App::DocumentObjectGroupPython] G4_MYLAR  # scripted group (container) (typed FeaturePython)
  Dunit = g/cm3
  Dvalue = 1.4
  Group = -> [C_element082,H_element076,O_element078]
  conduct = 2
  density = 1
  expand = 3
  formula = G4_MYLAR
  name = G4_MYLAR
  specific = 4
FEATURE [App::DocumentObjectGroupPython] C_element083  label="C_element : 041"  # scripted group (container) (typed FeaturePython)
  n = 5
  ref = C_element
FEATURE [App::DocumentObjectGroupPython] H_element077  label="H_element : 039"  # scripted group (container) (typed FeaturePython)
  n = 8
  ref = H_element
FEATURE [App::DocumentObjectGroupPython] O_element079  label="O_element : 040"  # scripted group (container) (typed FeaturePython)
  n = 2
  ref = O_element
FEATURE [App::DocumentObjectGroupPython] G4_PLEXIGLASS  # scripted group (container) (typed FeaturePython)
  Dunit = g/cm3
  Dvalue = 1.19
  Group = -> [C_element083,H_element077,O_element079]
  conduct = 2
  density = 1
  expand = 3
  formula = G4_PLEXIGLASS
  name = G4_PLEXIGLASS
  specific = 4
FEATURE [App::DocumentObjectGroupPython] C_element084  label="C_element : 042"  # scripted group (container) (typed FeaturePython)
  n = 1
  ref = C_element
FEATURE [App::DocumentObjectGroupPython] H_element078  label="H_element : 040"  # scripted group (container) (typed FeaturePython)
  n = 2
  ref = H_element
FEATURE [App::DocumentObjectGroupPython] O_element080  label="O_element : 041"  # scripted group (container) (typed FeaturePython)
  n = 1
  ref = O_element
FEATURE [App::DocumentObjectGroupPython] G4_POLYOXYMETHYLENE  # scripted group (container) (typed FeaturePython)
  Dunit = g/cm3
  Dvalue = 1.425
  Group = -> [C_element084,H_element078,O_element080]
  conduct = 2
  density = 1
  expand = 3
  formula = G4_POLYOXYMETHYLENE
  name = G4_POLYOXYMETHYLENE
  specific = 4
FEATURE [App::DocumentObjectGroupPython] C_element085  label="C_element : 043"  # scripted group (container) (typed FeaturePython)
  n = 2
  ref = C_element
FEATURE [App::DocumentObjectGroupPython] H_element079  label="H_element : 041"  # scripted group (container) (typed FeaturePython)
  n = 4
  ref = H_element
FEATURE [App::DocumentObjectGroupPython] G4_POLYPROPYLENE  # scripted group (container) (typed FeaturePython)
  Dunit = g/cm3
  Dvalue = 0.9
  Group = -> [C_element085,H_element079]
  conduct = 2
  density = 1
  expand = 3
  formula = G4_POLYPROPYLENE
  name = G4_POLYPROPYLENE
  specific = 4
FEATURE [App::DocumentObjectGroupPython] C_element086  label="C_element : 044"  # scripted group (container) (typed FeaturePython)
  n = 8
  ref = C_element
FEATURE [App::DocumentObjectGroupPython] H_element080  label="H_element : 042"  # scripted group (container) (typed FeaturePython)
  n = 8
  ref = H_element
FEATURE [App::DocumentObjectGroupPython] G4_POLYSTYRENE  # scripted group (container) (typed FeaturePython)
  Dunit = g/cm3
  Dvalue = 1.06
  Group = -> [C_element086,H_element080]
  conduct = 2
  density = 1
  expand = 3
  formula = G4_POLYSTYRENE
  name = G4_POLYSTYRENE
  specific = 4
FEATURE [App::DocumentObjectGroupPython] C_element087  label="C_element : 045"  # scripted group (container) (typed FeaturePython)
  n = 2
  ref = C_element
FEATURE [App::DocumentObjectGroupPython] F_element014  label="F_element : 4"  # scripted group (container) (typed FeaturePython)
  n = 4
  ref = F_element
FEATURE [App::DocumentObjectGroupPython] G4_TEFLON  # scripted group (container) (typed FeaturePython)
  Dunit = g/cm3
  Dvalue = 2.2
  Group = -> [C_element087,F_element014]
  conduct = 2
  density = 1
  expand = 3
  formula = G4_TEFLON
  name = G4_TEFLON
  specific = 4
FEATURE [App::DocumentObjectGroupPython] C_element088  label="C_element : 046"  # scripted group (container) (typed FeaturePython)
  n = 2
  ref = C_element
FEATURE [App::DocumentObjectGroupPython] F_element015  label="F_element : 006"  # scripted group (container) (typed FeaturePython)
  n = 3
  ref = F_element
FEATURE [App::DocumentObjectGroupPython] Cl_element018  label="Cl_element : 008"  # scripted group (container) (typed FeaturePython)
  n = 1
  ref = Cl_element
FEATURE [App::DocumentObjectGroupPython] G4_POLYTRIFLUOROCHLOROETHYLENE  # scripted group (container) (typed FeaturePython)
  Dunit = g/cm3
  Dvalue = 2.1
  Group = -> [C_element088,F_element015,Cl_element018]
  conduct = 2
  density = 1
  expand = 3
  formula = G4_POLYTRIFLUOROCHLOROETHYLENE
  name = G4_POLYTRIFLUOROCHLOROETHYLENE
  specific = 4
FEATURE [App::DocumentObjectGroupPython] C_element089  label="C_element : 047"  # scripted group (container) (typed FeaturePython)
  n = 4
  ref = C_element
FEATURE [App::DocumentObjectGroupPython] H_element081  label="H_element : 043"  # scripted group (container) (typed FeaturePython)
  n = 6
  ref = H_element
FEATURE [App::DocumentObjectGroupPython] O_element081  label="O_element : 042"  # scripted group (container) (typed FeaturePython)
  n = 2
  ref = O_element
FEATURE [App::DocumentObjectGroupPython] G4_POLYVINYL_ACETATE  # scripted group (container) (typed FeaturePython)
  Dunit = g/cm3
  Dvalue = 1.19
  Group = -> [C_element089,H_element081,O_element081]
  conduct = 2
  density = 1
  expand = 3
  formula = G4_POLYVINYL_ACETATE
  name = G4_POLYVINYL_ACETATE
  specific = 4
FEATURE [App::DocumentObjectGroupPython] C_element090  label="C_element : 048"  # scripted group (container) (typed FeaturePython)
  n = 2
  ref = C_element
FEATURE [App::DocumentObjectGroupPython] H_element082  label="H_element : 044"  # scripted group (container) (typed FeaturePython)
  n = 4
  ref = H_element
FEATURE [App::DocumentObjectGroupPython] O_element082  label="O_element : 043"  # scripted group (container) (typed FeaturePython)
  n = 1
  ref = O_element
FEATURE [App::DocumentObjectGroupPython] G4_POLYVINYL_ALCOHOL  # scripted group (container) (typed FeaturePython)
  Dunit = g/cm3
  Dvalue = 1.3
  Group = -> [C_element090,H_element082,O_element082]
  conduct = 2
  density = 1
  expand = 3
  formula = G4_POLYVINYL_ALCOHOL
  name = G4_POLYVINYL_ALCOHOL
  specific = 4
FEATURE [App::DocumentObjectGroupPython] C_element091  label="C_element : 049"  # scripted group (container) (typed FeaturePython)
  n = 8
  ref = C_element
FEATURE [App::DocumentObjectGroupPython] H_element083  label="H_element : 045"  # scripted group (container) (typed FeaturePython)
  n = 14
  ref = H_element
FEATURE [App::DocumentObjectGroupPython] O_element083  label="O_element : 044"  # scripted group (container) (typed FeaturePython)
  n = 2
  ref = O_element
FEATURE [App::DocumentObjectGroupPython] G4_POLYVINYL_BUTYRAL  # scripted group (container) (typed FeaturePython)
  Dunit = g/cm3
  Dvalue = 1.12
  Group = -> [C_element091,H_element083,O_element083]
  conduct = 2
  density = 1
  expand = 3
  formula = G4_POLYVINYL_BUTYRAL
  name = G4_POLYVINYL_BUTYRAL
  specific = 4
FEATURE [App::DocumentObjectGroupPython] C_element092  label="C_element : 050"  # scripted group (container) (typed FeaturePython)
  n = 2
  ref = C_element
FEATURE [App::DocumentObjectGroupPython] H_element084  label="H_element : 046"  # scripted group (container) (typed FeaturePython)
  n = 3
  ref = H_element
FEATURE [App::DocumentObjectGroupPython] Cl_element019  label="Cl_element : 009"  # scripted group (container) (typed FeaturePython)
  n = 1
  ref = Cl_element
FEATURE [App::DocumentObjectGroupPython] G4_POLYVINYL_CHLORIDE  # scripted group (container) (typed FeaturePython)
  Dunit = g/cm3
  Dvalue = 1.3
  Group = -> [C_element092,H_element084,Cl_element019]
  conduct = 2
  density = 1
  expand = 3
  formula = G4_POLYVINYL_CHLORIDE
  name = G4_POLYVINYL_CHLORIDE
  specific = 4
FEATURE [App::DocumentObjectGroupPython] C_element093  label="C_element : 051"  # scripted group (container) (typed FeaturePython)
  n = 2
  ref = C_element
FEATURE [App::DocumentObjectGroupPython] H_element085  label="H_element : 047"  # scripted group (container) (typed FeaturePython)
  n = 2
  ref = H_element
FEATURE [App::DocumentObjectGroupPython] Cl_element020  label="Cl_element : 010"  # scripted group (container) (typed FeaturePython)
  n = 2
  ref = Cl_element
FEATURE [App::DocumentObjectGroupPython] G4_POLYVINYLIDENE_CHLORIDE  # scripted group (container) (typed FeaturePython)
  Dunit = g/cm3
  Dvalue = 1.7
  Group = -> [C_element093,H_element085,Cl_element020]
  conduct = 2
  density = 1
  expand = 3
  formula = G4_POLYVINYLIDENE_CHLORIDE
  name = G4_POLYVINYLIDENE_CHLORIDE
  specific = 4
FEATURE [App::DocumentObjectGroupPython] C_element094  label="C_element : 052"  # scripted group (container) (typed FeaturePython)
  n = 2
  ref = C_element
FEATURE [App::DocumentObjectGroupPython] H_element086  label="H_element : 048"  # scripted group (container) (typed FeaturePython)
  n = 2
  ref = H_element
FEATURE [App::DocumentObjectGroupPython] F_element016  label="F_element : 007"  # scripted group (container) (typed FeaturePython)
  n = 2
  ref = F_element
FEATURE [App::DocumentObjectGroupPython] G4_POLYVINYLIDENE_FLUORIDE  # scripted group (container) (typed FeaturePython)
  Dunit = g/cm3
  Dvalue = 1.76
  Group = -> [C_element094,H_element086,F_element016]
  conduct = 2
  density = 1
  expand = 3
  formula = G4_POLYVINYLIDENE_FLUORIDE
  name = G4_POLYVINYLIDENE_FLUORIDE
  specific = 4
FEATURE [App::DocumentObjectGroupPython] C_element095  label="C_element : 053"  # scripted group (container) (typed FeaturePython)
  n = 6
  ref = C_element
FEATURE [App::DocumentObjectGroupPython] H_element087  label="H_element : 9"  # scripted group (container) (typed FeaturePython)
  n = 9
  ref = H_element
FEATURE [App::DocumentObjectGroupPython] N_element037  label="N_element : 016"  # scripted group (container) (typed FeaturePython)
  n = 1
  ref = N_element
FEATURE [App::DocumentObjectGroupPython] O_element084  label="O_element : 045"  # scripted group (container) (typed FeaturePython)
  n = 1
  ref = O_element
FEATURE [App::DocumentObjectGroupPython] G4_POLYVINYL_PYRROLIDONE  # scripted group (container) (typed FeaturePython)
  Dunit = g/cm3
  Dvalue = 1.25
  Group = -> [C_element095,H_element087,N_element037,O_element084]
  conduct = 2
  density = 1
  expand = 3
  formula = G4_POLYVINYL_PYRROLIDONE
  name = G4_POLYVINYL_PYRROLIDONE
  specific = 4
FEATURE [App::DocumentObjectGroupPython] K_element008  label="K_element : 1"  # scripted group (container) (typed FeaturePython)
  n = 1
  ref = K_element
FEATURE [App::DocumentObjectGroupPython] I_element006  label="I_element : 003"  # scripted group (container) (typed FeaturePython)
  n = 1
  ref = I_element
FEATURE [App::DocumentObjectGroupPython] G4_POTASSIUM_IODIDE  # scripted group (container) (typed FeaturePython)
  Dunit = g/cm3
  Dvalue = 3.13
  Group = -> [K_element008,I_element006]
  conduct = 2
  density = 1
  expand = 3
  formula = G4_POTASSIUM_IODIDE
  name = G4_POTASSIUM_IODIDE
  specific = 4
FEATURE [App::DocumentObjectGroupPython] K_element009  label="K_element : 2"  # scripted group (container) (typed FeaturePython)
  n = 2
  ref = K_element
FEATURE [App::DocumentObjectGroupPython] O_element085  label="O_element : 046"  # scripted group (container) (typed FeaturePython)
  n = 1
  ref = O_element
FEATURE [App::DocumentObjectGroupPython] G4_POTASSIUM_OXIDE  # scripted group (container) (typed FeaturePython)
  Dunit = g/cm3
  Dvalue = 2.32
  Group = -> [K_element009,O_element085]
  conduct = 2
  density = 1
  expand = 3
  formula = G4_POTASSIUM_OXIDE
  name = G4_POTASSIUM_OXIDE
  specific = 4
FEATURE [App::DocumentObjectGroupPython] C_element096  label="C_element : 054"  # scripted group (container) (typed FeaturePython)
  n = 3
  ref = C_element
FEATURE [App::DocumentObjectGroupPython] H_element088  label="H_element : 049"  # scripted group (container) (typed FeaturePython)
  n = 8
  ref = H_element
FEATURE [App::DocumentObjectGroupPython] G4_PROPANE  # scripted group (container) (typed FeaturePython)
  Dunit = g/cm3
  Dvalue = 0.00187939
  Group = -> [C_element096,H_element088]
  conduct = 2
  density = 1
  expand = 3
  formula = G4_PROPANE
  name = G4_PROPANE
  specific = 4
FEATURE [App::DocumentObjectGroupPython] C_element097  label="C_element : 055"  # scripted group (container) (typed FeaturePython)
  n = 3
  ref = C_element
FEATURE [App::DocumentObjectGroupPython] H_element089  label="H_element : 050"  # scripted group (container) (typed FeaturePython)
  n = 8
  ref = H_element
FEATURE [App::DocumentObjectGroupPython] G4_lPROPANE  # scripted group (container) (typed FeaturePython)
  Dunit = g/cm3
  Dvalue = 0.43
  Group = -> [C_element097,H_element089]
  conduct = 2
  density = 1
  expand = 3
  formula = G4_lPROPANE
  name = G4_lPROPANE
  specific = 4
FEATURE [App::DocumentObjectGroupPython] C_element098  label="C_element : 056"  # scripted group (container) (typed FeaturePython)
  n = 3
  ref = C_element
FEATURE [App::DocumentObjectGroupPython] H_element090  label="H_element : 051"  # scripted group (container) (typed FeaturePython)
  n = 8
  ref = H_element
FEATURE [App::DocumentObjectGroupPython] O_element086  label="O_element : 047"  # scripted group (container) (typed FeaturePython)
  n = 1
  ref = O_element
FEATURE [App::DocumentObjectGroupPython] G4_N_PROPYL_ALCOHOL  label="G4_N-PROPYL_ALCOHOL"  # scripted group (container) (typed FeaturePython)
  Dunit = g/cm3
  Dvalue = 0.8035
  Group = -> [C_element098,H_element090,O_element086]
  conduct = 2
  density = 1
  expand = 3
  formula = G4_N-PROPYL_ALCOHOL
  name = G4_N-PROPYL_ALCOHOL
  specific = 4
FEATURE [App::DocumentObjectGroupPython] C_element099  label="C_element : 057"  # scripted group (container) (typed FeaturePython)
  n = 5
  ref = C_element
FEATURE [App::DocumentObjectGroupPython] H_element091  label="H_element : 052"  # scripted group (container) (typed FeaturePython)
  n = 5
  ref = H_element
FEATURE [App::DocumentObjectGroupPython] N_element038  label="N_element : 017"  # scripted group (container) (typed FeaturePython)
  n = 1
  ref = N_element
FEATURE [App::DocumentObjectGroupPython] G4_PYRIDINE  # scripted group (container) (typed FeaturePython)
  Dunit = g/cm3
  Dvalue = 0.9819
  Group = -> [C_element099,H_element091,N_element038]
  conduct = 2
  density = 1
  expand = 3
  formula = G4_PYRIDINE
  name = G4_PYRIDINE
  specific = 4
FEATURE [App::DocumentObjectGroupPython] H_element092  label="H_element : 0.144"  # scripted group (container) (typed FeaturePython)
  n = 0.143711
FEATURE [App::DocumentObjectGroupPython] C_element100  label="C_element : 0.856"  # scripted group (container) (typed FeaturePython)
  n = 0.856289
FEATURE [App::DocumentObjectGroupPython] G4_RUBBER_BUTYL  # scripted group (container) (typed FeaturePython)
  Dunit = g/cm3
  Dvalue = 0.92
  Group = -> [H_element092,C_element100]
  conduct = 2
  density = 1
  expand = 3
  formula = G4_RUBBER_BUTYL
  name = G4_RUBBER_BUTYL
  specific = 4
FEATURE [App::DocumentObjectGroupPython] H_element093  label="H_element : 0.118"  # scripted group (container) (typed FeaturePython)
  n = 0.118371
FEATURE [App::DocumentObjectGroupPython] C_element101  label="C_element : 0.882"  # scripted group (container) (typed FeaturePython)
  n = 0.881629
FEATURE [App::DocumentObjectGroupPython] G4_RUBBER_NATURAL  # scripted group (container) (typed FeaturePython)
  Dunit = g/cm3
  Dvalue = 0.92
  Group = -> [H_element093,C_element101]
  conduct = 2
  density = 1
  expand = 3
  formula = G4_RUBBER_NATURAL
  name = G4_RUBBER_NATURAL
  specific = 4
FEATURE [App::DocumentObjectGroupPython] H_element094  label="H_element : 0.145"  # scripted group (container) (typed FeaturePython)
  n = 0.05692
FEATURE [App::DocumentObjectGroupPython] C_element102  label="C_element : 0.543"  # scripted group (container) (typed FeaturePython)
  n = 0.542646
FEATURE [App::DocumentObjectGroupPython] Cl_element021  label="Cl_element : 0.400"  # scripted group (container) (typed FeaturePython)
  n = 0.400434
FEATURE [App::DocumentObjectGroupPython] G4_RUBBER_NEOPRENE  # scripted group (container) (typed FeaturePython)
  Dunit = g/cm3
  Dvalue = 1.23
  Group = -> [H_element094,C_element102,Cl_element021]
  conduct = 2
  density = 1
  expand = 3
  formula = G4_RUBBER_NEOPRENE
  name = G4_RUBBER_NEOPRENE
  specific = 4
FEATURE [App::DocumentObjectGroupPython] Si_element006  label="Si_element : 1"  # scripted group (container) (typed FeaturePython)
  n = 1
  ref = Si_element
FEATURE [App::DocumentObjectGroupPython] O_element087  label="O_element : 048"  # scripted group (container) (typed FeaturePython)
  n = 2
  ref = O_element
FEATURE [App::DocumentObjectGroupPython] G4_SILICON_DIOXIDE  # scripted group (container) (typed FeaturePython)
  Dunit = g/cm3
  Dvalue = 2.32
  Group = -> [Si_element006,O_element087]
  conduct = 2
  density = 1
  expand = 3
  formula = G4_SILICON_DIOXIDE
  name = G4_SILICON_DIOXIDE
  specific = 4
FEATURE [App::DocumentObjectGroupPython] Ag_element002  label="Ag_element : 1"  # scripted group (container) (typed FeaturePython)
  n = 1
  ref = Ag_element
FEATURE [App::DocumentObjectGroupPython] Br_element005  label="Br_element : 003"  # scripted group (container) (typed FeaturePython)
  n = 1
  ref = Br_element
FEATURE [App::DocumentObjectGroupPython] G4_SILVER_BROMIDE  # scripted group (container) (typed FeaturePython)
  Dunit = g/cm3
  Dvalue = 6.473
  Group = -> [Ag_element002,Br_element005]
  conduct = 2
  density = 1
  expand = 3
  formula = G4_SILVER_BROMIDE
  name = G4_SILVER_BROMIDE
  specific = 4
FEATURE [App::DocumentObjectGroupPython] Ag_element003  label="Ag_element : 002"  # scripted group (container) (typed FeaturePython)
  n = 1
  ref = Ag_element
FEATURE [App::DocumentObjectGroupPython] Cl_element022  label="Cl_element : 011"  # scripted group (container) (typed FeaturePython)
  n = 1
  ref = Cl_element
FEATURE [App::DocumentObjectGroupPython] G4_SILVER_CHLORIDE  # scripted group (container) (typed FeaturePython)
  Dunit = g/cm3
  Dvalue = 5.56
  Group = -> [Ag_element003,Cl_element022]
  conduct = 2
  density = 1
  expand = 3
  formula = G4_SILVER_CHLORIDE
  name = G4_SILVER_CHLORIDE
  specific = 4
FEATURE [App::DocumentObjectGroupPython] Br_element006  label="Br_element : 0.423"  # scripted group (container) (typed FeaturePython)
  n = 0.422895
FEATURE [App::DocumentObjectGroupPython] Ag_element004  label="Ag_element : 0.574"  # scripted group (container) (typed FeaturePython)
  n = 0.573748
FEATURE [App::DocumentObjectGroupPython] I_element007  label="I_element : 0.649"  # scripted group (container) (typed FeaturePython)
  n = 0.003357
FEATURE [App::DocumentObjectGroupPython] G4_SILVER_HALIDES  # scripted group (container) (typed FeaturePython)
  Dunit = g/cm3
  Dvalue = 6.47
  Group = -> [Br_element006,Ag_element004,I_element007]
  conduct = 2
  density = 1
  expand = 3
  formula = G4_SILVER_HALIDES
  name = G4_SILVER_HALIDES
  specific = 4
FEATURE [App::DocumentObjectGroupPython] Ag_element005  label="Ag_element : 003"  # scripted group (container) (typed FeaturePython)
  n = 1
  ref = Ag_element
FEATURE [App::DocumentObjectGroupPython] I_element008  label="I_element : 004"  # scripted group (container) (typed FeaturePython)
  n = 1
  ref = I_element
FEATURE [App::DocumentObjectGroupPython] G4_SILVER_IODIDE  # scripted group (container) (typed FeaturePython)
  Dunit = g/cm3
  Dvalue = 6.01
  Group = -> [Ag_element005,I_element008]
  conduct = 2
  density = 1
  expand = 3
  formula = G4_SILVER_IODIDE
  name = G4_SILVER_IODIDE
  specific = 4
FEATURE [App::DocumentObjectGroupPython] H_element095  label="H_element : 0.100"  # scripted group (container) (typed FeaturePython)
  n = 0.1
FEATURE [App::DocumentObjectGroupPython] C_element103  label="C_element : 0.204"  # scripted group (container) (typed FeaturePython)
  n = 0.204
FEATURE [App::DocumentObjectGroupPython] N_element039  label="N_element : 0.759"  # scripted group (container) (typed FeaturePython)
  n = 0.042
FEATURE [App::DocumentObjectGroupPython] O_element088  label="O_element : 0.645"  # scripted group (container) (typed FeaturePython)
  n = 0.645
FEATURE [App::DocumentObjectGroupPython] Na_element013  label="Na_element : 0.100"  # scripted group (container) (typed FeaturePython)
  n = 0.002
FEATURE [App::DocumentObjectGroupPython] P_element009  label="P_element : 0.107"  # scripted group (container) (typed FeaturePython)
  n = 0.001
FEATURE [App::DocumentObjectGroupPython] S_element020  label="S_element : 0.021"  # scripted group (container) (typed FeaturePython)
  n = 0.002
FEATURE [App::DocumentObjectGroupPython] Cl_element023  label="Cl_element : 0.590"  # scripted group (container) (typed FeaturePython)
  n = 0.003
FEATURE [App::DocumentObjectGroupPython] K_element010  label="K_element : 0.001"  # scripted group (container) (typed FeaturePython)
  n = 0.001
FEATURE [App::DocumentObjectGroupPython] G4_SKIN_ICRP  # scripted group (container) (typed FeaturePython)
  Dunit = g/cm3
  Dvalue = 1.09
  Group = -> [H_element095,C_element103,N_element039,O_element088,Na_element013,P_element009,S_element020,Cl_element023,K_element010]
  conduct = 2
  density = 1
  expand = 3
  formula = G4_SKIN_ICRP
  name = G4_SKIN_ICRP
  specific = 4
FEATURE [App::DocumentObjectGroupPython] Na_element014  label="Na_element : 2"  # scripted group (container) (typed FeaturePython)
  n = 2
  ref = Na_element
FEATURE [App::DocumentObjectGroupPython] C_element104  label="C_element : 058"  # scripted group (container) (typed FeaturePython)
  n = 1
  ref = C_element
FEATURE [App::DocumentObjectGroupPython] O_element089  label="O_element : 049"  # scripted group (container) (typed FeaturePython)
  n = 3
  ref = O_element
FEATURE [App::DocumentObjectGroupPython] G4_SODIUM_CARBONATE  # scripted group (container) (typed FeaturePython)
  Dunit = g/cm3
  Dvalue = 2.532
  Group = -> [Na_element014,C_element104,O_element089]
  conduct = 2
  density = 1
  expand = 3
  formula = G4_SODIUM_CARBONATE
  name = G4_SODIUM_CARBONATE
  specific = 4
FEATURE [App::DocumentObjectGroupPython] Na_element015  label="Na_element : 1"  # scripted group (container) (typed FeaturePython)
  n = 1
  ref = Na_element
FEATURE [App::DocumentObjectGroupPython] I_element009  label="I_element : 005"  # scripted group (container) (typed FeaturePython)
  n = 1
  ref = I_element
FEATURE [App::DocumentObjectGroupPython] G4_SODIUM_IODIDE  # scripted group (container) (typed FeaturePython)
  Dunit = g/cm3
  Dvalue = 3.667
  Group = -> [Na_element015,I_element009]
  conduct = 2
  density = 1
  expand = 3
  formula = G4_SODIUM_IODIDE
  name = G4_SODIUM_IODIDE
  specific = 4
FEATURE [App::DocumentObjectGroupPython] Na_element016  label="Na_element : 003"  # scripted group (container) (typed FeaturePython)
  n = 2
  ref = Na_element
FEATURE [App::DocumentObjectGroupPython] O_element090  label="O_element : 050"  # scripted group (container) (typed FeaturePython)
  n = 1
  ref = O_element
FEATURE [App::DocumentObjectGroupPython] G4_SODIUM_MONOXIDE  # scripted group (container) (typed FeaturePython)
  Dunit = g/cm3
  Dvalue = 2.27
  Group = -> [Na_element016,O_element090]
  conduct = 2
  density = 1
  expand = 3
  formula = G4_SODIUM_MONOXIDE
  name = G4_SODIUM_MONOXIDE
  specific = 4
FEATURE [App::DocumentObjectGroupPython] Na_element017  label="Na_element : 004"  # scripted group (container) (typed FeaturePython)
  n = 1
  ref = Na_element
FEATURE [App::DocumentObjectGroupPython] N_element040  label="N_element : 018"  # scripted group (container) (typed FeaturePython)
  n = 1
  ref = N_element
FEATURE [App::DocumentObjectGroupPython] O_element091  label="O_element : 051"  # scripted group (container) (typed FeaturePython)
  n = 3
  ref = O_element
FEATURE [App::DocumentObjectGroupPython] G4_SODIUM_NITRATE  # scripted group (container) (typed FeaturePython)
  Dunit = g/cm3
  Dvalue = 2.261
  Group = -> [Na_element017,N_element040,O_element091]
  conduct = 2
  density = 1
  expand = 3
  formula = G4_SODIUM_NITRATE
  name = G4_SODIUM_NITRATE
  specific = 4
FEATURE [App::DocumentObjectGroupPython] C_element105  label="C_element : 059"  # scripted group (container) (typed FeaturePython)
  n = 14
  ref = C_element
FEATURE [App::DocumentObjectGroupPython] H_element096  label="H_element : 053"  # scripted group (container) (typed FeaturePython)
  n = 12
  ref = H_element
FEATURE [App::DocumentObjectGroupPython] G4_STILBENE  # scripted group (container) (typed FeaturePython)
  Dunit = g/cm3
  Dvalue = 0.9707
  Group = -> [C_element105,H_element096]
  conduct = 2
  density = 1
  expand = 3
  formula = G4_STILBENE
  name = G4_STILBENE
  specific = 4
FEATURE [App::DocumentObjectGroupPython] C_element106  label="C_element : 12"  # scripted group (container) (typed FeaturePython)
  n = 12
  ref = C_element
FEATURE [App::DocumentObjectGroupPython] H_element097  label="H_element : 22"  # scripted group (container) (typed FeaturePython)
  n = 22
  ref = H_element
FEATURE [App::DocumentObjectGroupPython] O_element092  label="O_element : 11"  # scripted group (container) (typed FeaturePython)
  n = 11
  ref = O_element
FEATURE [App::DocumentObjectGroupPython] G4_SUCROSE  # scripted group (container) (typed FeaturePython)
  Dunit = g/cm3
  Dvalue = 1.5805
  Group = -> [C_element106,H_element097,O_element092]
  conduct = 2
  density = 1
  expand = 3
  formula = G4_SUCROSE
  name = G4_SUCROSE
  specific = 4
FEATURE [App::DocumentObjectGroupPython] C_element107  label="C_element : 18"  # scripted group (container) (typed FeaturePython)
  n = 18
  ref = C_element
FEATURE [App::DocumentObjectGroupPython] H_element098  label="H_element : 054"  # scripted group (container) (typed FeaturePython)
  n = 14
  ref = H_element
FEATURE [App::DocumentObjectGroupPython] G4_TERPHENYL  # scripted group (container) (typed FeaturePython)
  Dunit = g/cm3
  Dvalue = 1.24
  Group = -> [C_element107,H_element098]
  conduct = 2
  density = 1
  expand = 3
  formula = G4_TERPHENYL
  name = G4_TERPHENYL
  specific = 4
FEATURE [App::DocumentObjectGroupPython] H_element099  label="H_element : 0.146"  # scripted group (container) (typed FeaturePython)
  n = 0.106
FEATURE [App::DocumentObjectGroupPython] C_element108  label="C_element : 0.883"  # scripted group (container) (typed FeaturePython)
  n = 0.099
FEATURE [App::DocumentObjectGroupPython] N_element041  label="N_element : 0.020"  # scripted group (container) (typed FeaturePython)
  n = 0.02
FEATURE [App::DocumentObjectGroupPython] O_element093  label="O_element : 0.766"  # scripted group (container) (typed FeaturePython)
  n = 0.766
FEATURE [App::DocumentObjectGroupPython] Na_element018  label="Na_element : 0.101"  # scripted group (container) (typed FeaturePython)
  n = 0.002
FEATURE [App::DocumentObjectGroupPython] P_element010  label="P_element : 0.108"  # scripted group (container) (typed FeaturePython)
  n = 0.001
FEATURE [App::DocumentObjectGroupPython] S_element021  label="S_element : 0.022"  # scripted group (container) (typed FeaturePython)
  n = 0.002
FEATURE [App::DocumentObjectGroupPython] Cl_element024  label="Cl_element : 0.002"  # scripted group (container) (typed FeaturePython)
  n = 0.002
FEATURE [App::DocumentObjectGroupPython] K_element011  label="K_element : 0.017"  # scripted group (container) (typed FeaturePython)
  n = 0.002
FEATURE [App::DocumentObjectGroupPython] G4_TESTIS_ICRP  # scripted group (container) (typed FeaturePython)
  Dunit = g/cm3
  Dvalue = 1.04
  Group = -> [H_element099,C_element108,N_element041,O_element093,Na_element018,P_element010,S_element021,Cl_element024,K_element011]
  conduct = 2
  density = 1
  expand = 3
  formula = G4_TESTIS_ICRP
  name = G4_TESTIS_ICRP
  specific = 4
FEATURE [App::DocumentObjectGroupPython] C_element109  label="C_element : 060"  # scripted group (container) (typed FeaturePython)
  n = 2
  ref = C_element
FEATURE [App::DocumentObjectGroupPython] Cl_element025  label="Cl_element : 012"  # scripted group (container) (typed FeaturePython)
  n = 4
  ref = Cl_element
FEATURE [App::DocumentObjectGroupPython] G4_TETRACHLOROETHYLENE  # scripted group (container) (typed FeaturePython)
  Dunit = g/cm3
  Dvalue = 1.625
  Group = -> [C_element109,Cl_element025]
  conduct = 2
  density = 1
  expand = 3
  formula = G4_TETRACHLOROETHYLENE
  name = G4_TETRACHLOROETHYLENE
  specific = 4
FEATURE [App::DocumentObjectGroupPython] Tl_element001  label="Tl_element : 1"  # scripted group (container) (typed FeaturePython)
  n = 1
  ref = Tl_element
FEATURE [App::DocumentObjectGroupPython] Cl_element026  label="Cl_element : 013"  # scripted group (container) (typed FeaturePython)
  n = 1
  ref = Cl_element
FEATURE [App::DocumentObjectGroupPython] G4_THALLIUM_CHLORIDE  # scripted group (container) (typed FeaturePython)
  Dunit = g/cm3
  Dvalue = 7.004
  Group = -> [Tl_element001,Cl_element026]
  conduct = 2
  density = 1
  expand = 3
  formula = G4_THALLIUM_CHLORIDE
  name = G4_THALLIUM_CHLORIDE
  specific = 4
FEATURE [App::DocumentObjectGroupPython] H_element100  label="H_element : 0.147"  # scripted group (container) (typed FeaturePython)
  n = 0.105
FEATURE [App::DocumentObjectGroupPython] C_element110  label="C_element : 0.256"  # scripted group (container) (typed FeaturePython)
  n = 0.256
FEATURE [App::DocumentObjectGroupPython] N_element042  label="N_element : 0.760"  # scripted group (container) (typed FeaturePython)
  n = 0.027
FEATURE [App::DocumentObjectGroupPython] O_element094  label="O_element : 0.602"  # scripted group (container) (typed FeaturePython)
  n = 0.602
FEATURE [App::DocumentObjectGroupPython] Na_element019  label="Na_element : 0.102"  # scripted group (container) (typed FeaturePython)
  n = 0.001
FEATURE [App::DocumentObjectGroupPython] P_element011  label="P_element : 0.109"  # scripted group (container) (typed FeaturePython)
  n = 0.002
FEATURE [App::DocumentObjectGroupPython] S_element022  label="S_element : 0.023"  # scripted group (container) (typed FeaturePython)
  n = 0.003
FEATURE [App::DocumentObjectGroupPython] Cl_element027  label="Cl_element : 0.591"  # scripted group (container) (typed FeaturePython)
  n = 0.002
FEATURE [App::DocumentObjectGroupPython] K_element012  label="K_element : 0.018"  # scripted group (container) (typed FeaturePython)
  n = 0.002
FEATURE [App::DocumentObjectGroupPython] G4_TISSUE_SOFT_ICRP  # scripted group (container) (typed FeaturePython)
  Dunit = g/cm3
  Dvalue = 1.03
  Group = -> [H_element100,C_element110,N_element042,O_element094,Na_element019,P_element011,S_element022,Cl_element027,K_element012]
  conduct = 2
  density = 1
  expand = 3
  formula = G4_TISSUE_SOFT_ICRP
  name = G4_TISSUE_SOFT_ICRP
  specific = 4
FEATURE [App::DocumentObjectGroupPython] H_element101  label="H_element : 0.148"  # scripted group (container) (typed FeaturePython)
  n = 0.101
FEATURE [App::DocumentObjectGroupPython] C_element111  label="C_element : 0.111"  # scripted group (container) (typed FeaturePython)
  n = 0.111
FEATURE [App::DocumentObjectGroupPython] N_element043  label="N_element : 0.026"  # scripted group (container) (typed FeaturePython)
  n = 0.026
FEATURE [App::DocumentObjectGroupPython] O_element095  label="O_element : 0.762"  # scripted group (container) (typed FeaturePython)
  n = 0.762
FEATURE [App::DocumentObjectGroupPython] G4_TISSUE_SOFT_ICRU_4  label="G4_TISSUE_SOFT_ICRU-4"  # scripted group (container) (typed FeaturePython)
  Dunit = g/cm3
  Dvalue = 1
  Group = -> [H_element101,C_element111,N_element043,O_element095]
  conduct = 2
  density = 1
  expand = 3
  formula = G4_TISSUE_SOFT_ICRU-4
  name = G4_TISSUE_SOFT_ICRU-4
  specific = 4
FEATURE [App::DocumentObjectGroupPython] H_element102  label="H_element : 0.149"  # scripted group (container) (typed FeaturePython)
  n = 0.101869
FEATURE [App::DocumentObjectGroupPython] C_element112  label="C_element : 0.456"  # scripted group (container) (typed FeaturePython)
  n = 0.456179
FEATURE [App::DocumentObjectGroupPython] N_element044  label="N_element : 0.761"  # scripted group (container) (typed FeaturePython)
  n = 0.035172
FEATURE [App::DocumentObjectGroupPython] O_element096  label="O_element : 0.407"  # scripted group (container) (typed FeaturePython)
  n = 0.40678
FEATURE [App::DocumentObjectGroupPython] G4_TISSUE_METHANE  label="G4_TISSUE-METHANE"  # scripted group (container) (typed FeaturePython)
  Dunit = g/cm3
  Dvalue = 0.00106409
  Group = -> [H_element102,C_element112,N_element044,O_element096]
  conduct = 2
  density = 1
  expand = 3
  formula = G4_TISSUE-METHANE
  name = G4_TISSUE-METHANE
  specific = 4
FEATURE [App::DocumentObjectGroupPython] H_element103  label="H_element : 0.103"  # scripted group (container) (typed FeaturePython)
  n = 0.102672
FEATURE [App::DocumentObjectGroupPython] C_element113  label="C_element : 0.569"  # scripted group (container) (typed FeaturePython)
  n = 0.56894
FEATURE [App::DocumentObjectGroupPython] N_element045  label="N_element : 0.762"  # scripted group (container) (typed FeaturePython)
  n = 0.035022
FEATURE [App::DocumentObjectGroupPython] O_element097  label="O_element : 0.293"  # scripted group (container) (typed FeaturePython)
  n = 0.293366
FEATURE [App::DocumentObjectGroupPython] G4_TISSUE_PROPANE  label="G4_TISSUE-PROPANE"  # scripted group (container) (typed FeaturePython)
  Dunit = g/cm3
  Dvalue = 0.00182628
  Group = -> [H_element103,C_element113,N_element045,O_element097]
  conduct = 2
  density = 1
  expand = 3
  formula = G4_TISSUE-PROPANE
  name = G4_TISSUE-PROPANE
  specific = 4
FEATURE [App::DocumentObjectGroupPython] Ti_element003  label="Ti_element : 1"  # scripted group (container) (typed FeaturePython)
  n = 1
  ref = Ti_element
FEATURE [App::DocumentObjectGroupPython] O_element098  label="O_element : 052"  # scripted group (container) (typed FeaturePython)
  n = 2
  ref = O_element
FEATURE [App::DocumentObjectGroupPython] G4_TITANIUM_DIOXIDE  # scripted group (container) (typed FeaturePython)
  Dunit = g/cm3
  Dvalue = 4.26
  Group = -> [Ti_element003,O_element098]
  conduct = 2
  density = 1
  expand = 3
  formula = G4_TITANIUM_DIOXIDE
  name = G4_TITANIUM_DIOXIDE
  specific = 4
FEATURE [App::DocumentObjectGroupPython] C_element114  label="C_element : 061"  # scripted group (container) (typed FeaturePython)
  n = 7
  ref = C_element
FEATURE [App::DocumentObjectGroupPython] H_element104  label="H_element : 055"  # scripted group (container) (typed FeaturePython)
  n = 8
  ref = H_element
FEATURE [App::DocumentObjectGroupPython] G4_TOLUENE  # scripted group (container) (typed FeaturePython)
  Dunit = g/cm3
  Dvalue = 0.8669
  Group = -> [C_element114,H_element104]
  conduct = 2
  density = 1
  expand = 3
  formula = G4_TOLUENE
  name = G4_TOLUENE
  specific = 4
FEATURE [App::DocumentObjectGroupPython] C_element115  label="C_element : 062"  # scripted group (container) (typed FeaturePython)
  n = 2
  ref = C_element
FEATURE [App::DocumentObjectGroupPython] H_element105  label="H_element : 056"  # scripted group (container) (typed FeaturePython)
  n = 1
  ref = H_element
FEATURE [App::DocumentObjectGroupPython] Cl_element028  label="Cl_element : 014"  # scripted group (container) (typed FeaturePython)
  n = 3
  ref = Cl_element
FEATURE [App::DocumentObjectGroupPython] G4_TRICHLOROETHYLENE  # scripted group (container) (typed FeaturePython)
  Dunit = g/cm3
  Dvalue = 1.46
  Group = -> [C_element115,H_element105,Cl_element028]
  conduct = 2
  density = 1
  expand = 3
  formula = G4_TRICHLOROETHYLENE
  name = G4_TRICHLOROETHYLENE
  specific = 4
FEATURE [App::DocumentObjectGroupPython] C_element116  label="C_element : 063"  # scripted group (container) (typed FeaturePython)
  n = 6
  ref = C_element
FEATURE [App::DocumentObjectGroupPython] H_element106  label="H_element : 15"  # scripted group (container) (typed FeaturePython)
  n = 15
  ref = H_element
FEATURE [App::DocumentObjectGroupPython] O_element099  label="O_element : 053"  # scripted group (container) (typed FeaturePython)
  n = 4
  ref = O_element
FEATURE [App::DocumentObjectGroupPython] P_element012  label="P_element : 1"  # scripted group (container) (typed FeaturePython)
  n = 1
  ref = P_element
FEATURE [App::DocumentObjectGroupPython] G4_TRIETHYL_PHOSPHATE  # scripted group (container) (typed FeaturePython)
  Dunit = g/cm3
  Dvalue = 1.07
  Group = -> [C_element116,H_element106,O_element099,P_element012]
  conduct = 2
  density = 1
  expand = 3
  formula = G4_TRIETHYL_PHOSPHATE
  name = G4_TRIETHYL_PHOSPHATE
  specific = 4
FEATURE [App::DocumentObjectGroupPython] W_element003  label="W_element : 003"  # scripted group (container) (typed FeaturePython)
  n = 1
  ref = W_element
FEATURE [App::DocumentObjectGroupPython] F_element017  label="F_element : 6"  # scripted group (container) (typed FeaturePython)
  n = 6
  ref = F_element
FEATURE [App::DocumentObjectGroupPython] G4_TUNGSTEN_HEXAFLUORIDE  # scripted group (container) (typed FeaturePython)
  Dunit = g/cm3
  Dvalue = 2.4
  Group = -> [W_element003,F_element017]
  conduct = 2
  density = 1
  expand = 3
  formula = G4_TUNGSTEN_HEXAFLUORIDE
  name = G4_TUNGSTEN_HEXAFLUORIDE
  specific = 4
FEATURE [App::DocumentObjectGroupPython] U_element001  label="U_element : 1"  # scripted group (container) (typed FeaturePython)
  n = 1
  ref = U_element
FEATURE [App::DocumentObjectGroupPython] C_element117  label="C_element : 064"  # scripted group (container) (typed FeaturePython)
  n = 2
  ref = C_element
FEATURE [App::DocumentObjectGroupPython] G4_URANIUM_DICARBIDE  # scripted group (container) (typed FeaturePython)
  Dunit = g/cm3
  Dvalue = 11.28
  Group = -> [U_element001,C_element117]
  conduct = 2
  density = 1
  expand = 3
  formula = G4_URANIUM_DICARBIDE
  name = G4_URANIUM_DICARBIDE
  specific = 4
FEATURE [App::DocumentObjectGroupPython] U_element002  label="U_element : 002"  # scripted group (container) (typed FeaturePython)
  n = 1
  ref = U_element
FEATURE [App::DocumentObjectGroupPython] C_element118  label="C_element : 065"  # scripted group (container) (typed FeaturePython)
  n = 1
  ref = C_element
FEATURE [App::DocumentObjectGroupPython] G4_URANIUM_MONOCARBIDE  # scripted group (container) (typed FeaturePython)
  Dunit = g/cm3
  Dvalue = 13.63
  Group = -> [U_element002,C_element118]
  conduct = 2
  density = 1
  expand = 3
  formula = G4_URANIUM_MONOCARBIDE
  name = G4_URANIUM_MONOCARBIDE
  specific = 4
FEATURE [App::DocumentObjectGroupPython] U_element003  label="U_element : 003"  # scripted group (container) (typed FeaturePython)
  n = 1
  ref = U_element
FEATURE [App::DocumentObjectGroupPython] O_element100  label="O_element : 054"  # scripted group (container) (typed FeaturePython)
  n = 2
  ref = O_element
FEATURE [App::DocumentObjectGroupPython] G4_URANIUM_OXIDE  # scripted group (container) (typed FeaturePython)
  Dunit = g/cm3
  Dvalue = 10.96
  Group = -> [U_element003,O_element100]
  conduct = 2
  density = 1
  expand = 3
  formula = G4_URANIUM_OXIDE
  name = G4_URANIUM_OXIDE
  specific = 4
FEATURE [App::DocumentObjectGroupPython] C_element119  label="C_element : 066"  # scripted group (container) (typed FeaturePython)
  n = 1
  ref = C_element
FEATURE [App::DocumentObjectGroupPython] H_element107  label="H_element : 057"  # scripted group (container) (typed FeaturePython)
  n = 4
  ref = H_element
FEATURE [App::DocumentObjectGroupPython] N_element046  label="N_element : 019"  # scripted group (container) (typed FeaturePython)
  n = 2
  ref = N_element
FEATURE [App::DocumentObjectGroupPython] O_element101  label="O_element : 055"  # scripted group (container) (typed FeaturePython)
  n = 1
  ref = O_element
FEATURE [App::DocumentObjectGroupPython] G4_UREA  # scripted group (container) (typed FeaturePython)
  Dunit = g/cm3
  Dvalue = 1.323
  Group = -> [C_element119,H_element107,N_element046,O_element101]
  conduct = 2
  density = 1
  expand = 3
  formula = G4_UREA
  name = G4_UREA
  specific = 4
FEATURE [App::DocumentObjectGroupPython] C_element120  label="C_element : 067"  # scripted group (container) (typed FeaturePython)
  n = 5
  ref = C_element
FEATURE [App::DocumentObjectGroupPython] H_element108  label="H_element : 058"  # scripted group (container) (typed FeaturePython)
  n = 11
  ref = H_element
FEATURE [App::DocumentObjectGroupPython] N_element047  label="N_element : 020"  # scripted group (container) (typed FeaturePython)
  n = 1
  ref = N_element
FEATURE [App::DocumentObjectGroupPython] O_element102  label="O_element : 056"  # scripted group (container) (typed FeaturePython)
  n = 2
  ref = O_element
FEATURE [App::DocumentObjectGroupPython] G4_VALINE  # scripted group (container) (typed FeaturePython)
  Dunit = g/cm3
  Dvalue = 1.23
  Group = -> [C_element120,H_element108,N_element047,O_element102]
  conduct = 2
  density = 1
  expand = 3
  formula = G4_VALINE
  name = G4_VALINE
  specific = 4
FEATURE [App::DocumentObjectGroupPython] H_element109  label="H_element : 0.009"  # scripted group (container) (typed FeaturePython)
  n = 0.009417
FEATURE [App::DocumentObjectGroupPython] C_element121  label="C_element : 0.281"  # scripted group (container) (typed FeaturePython)
  n = 0.280555
FEATURE [App::DocumentObjectGroupPython] F_element018  label="F_element : 0.710"  # scripted group (container) (typed FeaturePython)
  n = 0.710028
FEATURE [App::DocumentObjectGroupPython] G4_VITON  # scripted group (container) (typed FeaturePython)
  Dunit = g/cm3
  Dvalue = 1.8
  Group = -> [H_element109,C_element121,F_element018]
  conduct = 2
  density = 1
  expand = 3
  formula = G4_VITON
  name = G4_VITON
  specific = 4
FEATURE [App::DocumentObjectGroupPython] H_element110  label="H_element : 059"  # scripted group (container) (typed FeaturePython)
  n = 2
  ref = H_element
FEATURE [App::DocumentObjectGroupPython] O_element103  label="O_element : 057"  # scripted group (container) (typed FeaturePython)
  n = 1
  ref = O_element
FEATURE [App::DocumentObjectGroupPython] G4_WATER  # scripted group (container) (typed FeaturePython)
  Dunit = g/cm3
  Dvalue = 1
  Group = -> [H_element110,O_element103]
  conduct = 2
  density = 1
  expand = 3
  formula = G4_WATER
  name = G4_WATER
  specific = 4
FEATURE [App::DocumentObjectGroupPython] H_element111  label="H_element : 060"  # scripted group (container) (typed FeaturePython)
  n = 2
  ref = H_element
FEATURE [App::DocumentObjectGroupPython] O_element104  label="O_element : 058"  # scripted group (container) (typed FeaturePython)
  n = 1
  ref = O_element
FEATURE [App::DocumentObjectGroupPython] G4_WATER_VAPOR  # scripted group (container) (typed FeaturePython)
  Dunit = g/cm3
  Dvalue = 0.000756182
  Group = -> [H_element111,O_element104]
  conduct = 2
  density = 1
  expand = 3
  formula = G4_WATER_VAPOR
  name = G4_WATER_VAPOR
  specific = 4
FEATURE [App::DocumentObjectGroupPython] C_element122  label="C_element : 068"  # scripted group (container) (typed FeaturePython)
  n = 8
  ref = C_element
FEATURE [App::DocumentObjectGroupPython] H_element112  label="H_element : 061"  # scripted group (container) (typed FeaturePython)
  n = 10
  ref = H_element
FEATURE [App::DocumentObjectGroupPython] G4_XYLENE  # scripted group (container) (typed FeaturePython)
  Dunit = g/cm3
  Dvalue = 0.87
  Group = -> [C_element122,H_element112]
  conduct = 2
  density = 1
  expand = 3
  formula = G4_XYLENE
  name = G4_XYLENE
  specific = 4
FEATURE [App::DocumentObjectGroupPython] C_element123  label="C_element : 069"  # scripted group (container) (typed FeaturePython)
  n = 1
  ref = C_element
FEATURE [App::DocumentObjectGroupPython] G4_GRAPHITE  # scripted group (container) (typed FeaturePython)
  Dunit = g/cm3
  Dvalue = 2.21
  Group = -> [C_element123]
  conduct = 2
  density = 1
  expand = 3
  formula = G4_GRAPHITE
  name = G4_GRAPHITE
  specific = 4
FEATURE [App::DocumentObjectGroupPython] NIST  # scripted group (container) (typed FeaturePython)
  Group = -> [G4_A_150_TISSUE,G4_ACETONE,G4_ACETYLENE,G4_ADENINE,G4_ADIPOSE_TISSUE_ICRP,G4_AIR,G4_ALANINE,G4_ALUMINUM_OXIDE,G4_AMBER,G4_AMMONIA,G4_ANILINE,G4_ANTHRACENE,G4_B_100_BONE,G4_BAKELITE,G4_BARIUM_FLUORIDE,G4_BARIUM_SULFATE,G4_BENZENE,G4_BERYLLIUM_OXIDE,G4_BGO,G4_BLOOD_ICRP,G4_BONE_COMPACT_ICRU,G4_BONE_CORTICAL_ICRP,G4_BORON_CARBIDE,G4_BORON_OXIDE,G4_BRAIN_ICRP,G4_BUTANE,G4_N_BUTYL_ALCOHOL,G4_C_552,+152 more]
FEATURE [App::DocumentObjectGroupPython] H_element113  label="H_element : 062"  # scripted group (container) (typed FeaturePython)
  n = 1
  ref = H_element
FEATURE [App::DocumentObjectGroupPython] G4_H  # scripted group (container) (typed FeaturePython)
  Dunit = g/cm3
  Dvalue = 8.3748e-05
  Group = -> [H_element113]
  conduct = 2
  density = 1
  expand = 3
  formula = H
  name = G4_H
  specific = 4
FEATURE [App::DocumentObjectGroupPython] He_element001  label="He_element : 1"  # scripted group (container) (typed FeaturePython)
  n = 1
  ref = He_element
FEATURE [App::DocumentObjectGroupPython] G4_He  # scripted group (container) (typed FeaturePython)
  Dunit = g/cm3
  Dvalue = 0.000166322
  Group = -> [He_element001]
  conduct = 2
  density = 1
  expand = 3
  formula = He
  name = G4_He
  specific = 4
FEATURE [App::DocumentObjectGroupPython] Li_element008  label="Li_element : 008"  # scripted group (container) (typed FeaturePython)
  n = 1
  ref = Li_element
FEATURE [App::DocumentObjectGroupPython] G4_Li  # scripted group (container) (typed FeaturePython)
  Dunit = g/cm3
  Dvalue = 0.534
  Group = -> [Li_element008]
  conduct = 2
  density = 1
  expand = 3
  formula = Li
  name = G4_Li
  specific = 4
FEATURE [App::DocumentObjectGroupPython] Be_element002  label="Be_element : 002"  # scripted group (container) (typed FeaturePython)
  n = 1
  ref = Be_element
FEATURE [App::DocumentObjectGroupPython] G4_Be  # scripted group (container) (typed FeaturePython)
  Dunit = g/cm3
  Dvalue = 1.848
  Group = -> [Be_element002]
  conduct = 2
  density = 1
  expand = 3
  formula = Be
  name = G4_Be
  specific = 4
FEATURE [App::DocumentObjectGroupPython] B_element007  label="B_element : 007"  # scripted group (container) (typed FeaturePython)
  n = 1
  ref = B_element
FEATURE [App::DocumentObjectGroupPython] G4_B  # scripted group (container) (typed FeaturePython)
  Dunit = g/cm3
  Dvalue = 2.37
  Group = -> [B_element007]
  conduct = 2
  density = 1
  expand = 3
  formula = B
  name = G4_B
  specific = 4
FEATURE [App::DocumentObjectGroupPython] C_element124  label="C_element : 070"  # scripted group (container) (typed FeaturePython)
  n = 1
  ref = C_element
FEATURE [App::DocumentObjectGroupPython] G4_C  # scripted group (container) (typed FeaturePython)
  Dunit = g/cm3
  Dvalue = 2
  Group = -> [C_element124]
  conduct = 2
  density = 1
  expand = 3
  formula = C
  name = G4_C
  specific = 4
FEATURE [App::DocumentObjectGroupPython] N_element048  label="N_element : 021"  # scripted group (container) (typed FeaturePython)
  n = 1
  ref = N_element
FEATURE [App::DocumentObjectGroupPython] G4_N  # scripted group (container) (typed FeaturePython)
  Dunit = g/cm3
  Dvalue = 0.0011652
  Group = -> [N_element048]
  conduct = 2
  density = 1
  expand = 3
  formula = N
  name = G4_N
  specific = 4
FEATURE [App::DocumentObjectGroupPython] O_element105  label="O_element : 059"  # scripted group (container) (typed FeaturePython)
  n = 1
  ref = O_element
FEATURE [App::DocumentObjectGroupPython] G4_O  # scripted group (container) (typed FeaturePython)
  Dunit = g/cm3
  Dvalue = 0.00133151
  Group = -> [O_element105]
  conduct = 2
  density = 1
  expand = 3
  formula = O
  name = G4_O
  specific = 4
FEATURE [App::DocumentObjectGroupPython] F_element019  label="F_element : 008"  # scripted group (container) (typed FeaturePython)
  n = 1
  ref = F_element
FEATURE [App::DocumentObjectGroupPython] G4_F  # scripted group (container) (typed FeaturePython)
  Dunit = g/cm3
  Dvalue = 0.00158029
  Group = -> [F_element019]
  conduct = 2
  density = 1
  expand = 3
  formula = F
  name = G4_F
  specific = 4
FEATURE [App::DocumentObjectGroupPython] Ne_element001  label="Ne_element : 1"  # scripted group (container) (typed FeaturePython)
  n = 1
  ref = Ne_element
FEATURE [App::DocumentObjectGroupPython] G4_Ne  # scripted group (container) (typed FeaturePython)
  Dunit = g/cm3
  Dvalue = 0.000838505
  Group = -> [Ne_element001]
  conduct = 2
  density = 1
  expand = 3
  formula = Ne
  name = G4_Ne
  specific = 4
FEATURE [App::DocumentObjectGroupPython] Na_element020  label="Na_element : 005"  # scripted group (container) (typed FeaturePython)
  n = 1
  ref = Na_element
FEATURE [App::DocumentObjectGroupPython] G4_Na  # scripted group (container) (typed FeaturePython)
  Dunit = g/cm3
  Dvalue = 0.971
  Group = -> [Na_element020]
  conduct = 2
  density = 1
  expand = 3
  formula = Na
  name = G4_Na
  specific = 4
FEATURE [App::DocumentObjectGroupPython] Mg_element011  label="Mg_element : 005"  # scripted group (container) (typed FeaturePython)
  n = 1
  ref = Mg_element
FEATURE [App::DocumentObjectGroupPython] G4_Mg  # scripted group (container) (typed FeaturePython)
  Dunit = g/cm3
  Dvalue = 1.74
  Group = -> [Mg_element011]
  conduct = 2
  density = 1
  expand = 3
  formula = Mg
  name = G4_Mg
  specific = 4
FEATURE [App::DocumentObjectGroupPython] Al_element004  label="Al_element : 1"  # scripted group (container) (typed FeaturePython)
  n = 1
  ref = Al_element
FEATURE [App::DocumentObjectGroupPython] G4_Al  # scripted group (container) (typed FeaturePython)
  Dunit = g/cm3
  Dvalue = 2.699
  Group = -> [Al_element004]
  conduct = 2
  density = 1
  expand = 3
  formula = Al
  name = G4_Al
  specific = 4
FEATURE [App::DocumentObjectGroupPython] Si_element007  label="Si_element : 002"  # scripted group (container) (typed FeaturePython)
  n = 1
  ref = Si_element
FEATURE [App::DocumentObjectGroupPython] G4_Si  # scripted group (container) (typed FeaturePython)
  Dunit = g/cm3
  Dvalue = 2.33
  Group = -> [Si_element007]
  conduct = 2
  density = 1
  expand = 3
  formula = Si
  name = G4_Si
  specific = 4
FEATURE [App::DocumentObjectGroupPython] P_element013  label="P_element : 002"  # scripted group (container) (typed FeaturePython)
  n = 1
  ref = P_element
FEATURE [App::DocumentObjectGroupPython] G4_P  # scripted group (container) (typed FeaturePython)
  Dunit = g/cm3
  Dvalue = 2.2
  Group = -> [P_element013]
  conduct = 2
  density = 1
  expand = 3
  formula = P
  name = G4_P
  specific = 4
FEATURE [App::DocumentObjectGroupPython] S_element023  label="S_element : 007"  # scripted group (container) (typed FeaturePython)
  n = 1
  ref = S_element
FEATURE [App::DocumentObjectGroupPython] G4_S  # scripted group (container) (typed FeaturePython)
  Dunit = g/cm3
  Dvalue = 2
  Group = -> [S_element023]
  conduct = 2
  density = 1
  expand = 3
  formula = S
  name = G4_S
  specific = 4
FEATURE [App::DocumentObjectGroupPython] Cl_element029  label="Cl_element : 015"  # scripted group (container) (typed FeaturePython)
  n = 1
  ref = Cl_element
FEATURE [App::DocumentObjectGroupPython] G4_Cl  # scripted group (container) (typed FeaturePython)
  Dunit = g/cm3
  Dvalue = 0.00299473
  Group = -> [Cl_element029]
  conduct = 2
  density = 1
  expand = 3
  formula = Cl
  name = G4_Cl
  specific = 4
FEATURE [App::DocumentObjectGroupPython] Ar_element002  label="Ar_element : 1"  # scripted group (container) (typed FeaturePython)
  n = 1
  ref = Ar_element
FEATURE [App::DocumentObjectGroupPython] G4_Ar  # scripted group (container) (typed FeaturePython)
  Dunit = g/cm3
  Dvalue = 0.00166201
  Group = -> [Ar_element002]
  conduct = 2
  density = 1
  expand = 3
  formula = Ar
  name = G4_Ar
  specific = 4
FEATURE [App::DocumentObjectGroupPython] K_element013  label="K_element : 003"  # scripted group (container) (typed FeaturePython)
  n = 1
  ref = K_element
FEATURE [App::DocumentObjectGroupPython] G4_K  # scripted group (container) (typed FeaturePython)
  Dunit = g/cm3
  Dvalue = 0.862
  Group = -> [K_element013]
  conduct = 2
  density = 1
  expand = 3
  formula = K
  name = G4_K
  specific = 4
FEATURE [App::DocumentObjectGroupPython] Ca_element014  label="Ca_element : 007"  # scripted group (container) (typed FeaturePython)
  n = 1
  ref = Ca_element
FEATURE [App::DocumentObjectGroupPython] G4_Ca  # scripted group (container) (typed FeaturePython)
  Dunit = g/cm3
  Dvalue = 1.55
  Group = -> [Ca_element014]
  conduct = 2
  density = 1
  expand = 3
  formula = Ca
  name = G4_Ca
  specific = 4
FEATURE [App::DocumentObjectGroupPython] Sc_element001  label="Sc_element : 1"  # scripted group (container) (typed FeaturePython)
  n = 1
  ref = Sc_element
FEATURE [App::DocumentObjectGroupPython] G4_Sc  # scripted group (container) (typed FeaturePython)
  Dunit = g/cm3
  Dvalue = 2.989
  Group = -> [Sc_element001]
  conduct = 2
  density = 1
  expand = 3
  formula = Sc
  name = G4_Sc
  specific = 4
FEATURE [App::DocumentObjectGroupPython] Ti_element004  label="Ti_element : 002"  # scripted group (container) (typed FeaturePython)
  n = 1
  ref = Ti_element
FEATURE [App::DocumentObjectGroupPython] G4_Ti  # scripted group (container) (typed FeaturePython)
  Dunit = g/cm3
  Dvalue = 4.54
  Group = -> [Ti_element004]
  conduct = 2
  density = 1
  expand = 3
  formula = Ti
  name = G4_Ti
  specific = 4
FEATURE [App::DocumentObjectGroupPython] V_element001  label="V_element : 1"  # scripted group (container) (typed FeaturePython)
  n = 1
  ref = V_element
FEATURE [App::DocumentObjectGroupPython] G4_V  # scripted group (container) (typed FeaturePython)
  Dunit = g/cm3
  Dvalue = 6.11
  Group = -> [V_element001]
  conduct = 2
  density = 1
  expand = 3
  formula = V
  name = G4_V
  specific = 4
FEATURE [App::DocumentObjectGroupPython] Cr_element001  label="Cr_element : 1"  # scripted group (container) (typed FeaturePython)
  n = 1
  ref = Cr_element
FEATURE [App::DocumentObjectGroupPython] G4_Cr  # scripted group (container) (typed FeaturePython)
  Dunit = g/cm3
  Dvalue = 7.18
  Group = -> [Cr_element001]
  conduct = 2
  density = 1
  expand = 3
  formula = Cr
  name = G4_Cr
  specific = 4
FEATURE [App::DocumentObjectGroupPython] Mn_element001  label="Mn_element : 1"  # scripted group (container) (typed FeaturePython)
  n = 1
  ref = Mn_element
FEATURE [App::DocumentObjectGroupPython] G4_Mn  # scripted group (container) (typed FeaturePython)
  Dunit = g/cm3
  Dvalue = 7.44
  Group = -> [Mn_element001]
  conduct = 2
  density = 1
  expand = 3
  formula = Mn
  name = G4_Mn
  specific = 4
FEATURE [App::DocumentObjectGroupPython] Fe_element007  label="Fe_element : 004"  # scripted group (container) (typed FeaturePython)
  n = 1
  ref = Fe_element
FEATURE [App::DocumentObjectGroupPython] G4_Fe  # scripted group (container) (typed FeaturePython)
  Dunit = g/cm3
  Dvalue = 7.874
  Group = -> [Fe_element007]
  conduct = 2
  density = 1
  expand = 3
  formula = Fe
  name = G4_Fe
  specific = 4
FEATURE [App::DocumentObjectGroupPython] Co_element001  label="Co_element : 1"  # scripted group (container) (typed FeaturePython)
  n = 1
  ref = Co_element
FEATURE [App::DocumentObjectGroupPython] G4_Co  # scripted group (container) (typed FeaturePython)
  Dunit = g/cm3
  Dvalue = 8.9
  Group = -> [Co_element001]
  conduct = 2
  density = 1
  expand = 3
  formula = Co
  name = G4_Co
  specific = 4
FEATURE [App::DocumentObjectGroupPython] Ni_element001  label="Ni_element : 1"  # scripted group (container) (typed FeaturePython)
  n = 1
  ref = Ni_element
FEATURE [App::DocumentObjectGroupPython] G4_Ni  # scripted group (container) (typed FeaturePython)
  Dunit = g/cm3
  Dvalue = 8.902
  Group = -> [Ni_element001]
  conduct = 2
  density = 1
  expand = 3
  formula = Ni
  name = G4_Ni
  specific = 4
FEATURE [App::DocumentObjectGroupPython] Cu_element001  label="Cu_element : 1"  # scripted group (container) (typed FeaturePython)
  n = 1
  ref = Cu_element
FEATURE [App::DocumentObjectGroupPython] G4_Cu  # scripted group (container) (typed FeaturePython)
  Dunit = g/cm3
  Dvalue = 8.96
  Group = -> [Cu_element001]
  conduct = 2
  density = 1
  expand = 3
  formula = Cu
  name = G4_Cu
  specific = 4
FEATURE [App::DocumentObjectGroupPython] Zn_element001  label="Zn_element : 1"  # scripted group (container) (typed FeaturePython)
  n = 1
  ref = Zn_element
FEATURE [App::DocumentObjectGroupPython] G4_Zn  # scripted group (container) (typed FeaturePython)
  Dunit = g/cm3
  Dvalue = 7.133
  Group = -> [Zn_element001]
  conduct = 2
  density = 1
  expand = 3
  formula = Zn
  name = G4_Zn
  specific = 4
FEATURE [App::DocumentObjectGroupPython] Ga_element002  label="Ga_element : 002"  # scripted group (container) (typed FeaturePython)
  n = 1
  ref = Ga_element
FEATURE [App::DocumentObjectGroupPython] G4_Ga  # scripted group (container) (typed FeaturePython)
  Dunit = g/cm3
  Dvalue = 5.904
  Group = -> [Ga_element002]
  conduct = 2
  density = 1
  expand = 3
  formula = Ga
  name = G4_Ga
  specific = 4
FEATURE [App::DocumentObjectGroupPython] Ge_element002  label="Ge_element : 1"  # scripted group (container) (typed FeaturePython)
  n = 1
  ref = Ge_element
FEATURE [App::DocumentObjectGroupPython] G4_Ge  # scripted group (container) (typed FeaturePython)
  Dunit = g/cm3
  Dvalue = 5.323
  Group = -> [Ge_element002]
  conduct = 2
  density = 1
  expand = 3
  formula = Ge
  name = G4_Ge
  specific = 4
FEATURE [App::DocumentObjectGroupPython] As_element003  label="As_element : 002"  # scripted group (container) (typed FeaturePython)
  n = 1
  ref = As_element
FEATURE [App::DocumentObjectGroupPython] G4_As  # scripted group (container) (typed FeaturePython)
  Dunit = g/cm3
  Dvalue = 5.73
  Group = -> [As_element003]
  conduct = 2
  density = 1
  expand = 3
  formula = As
  name = G4_As
  specific = 4
FEATURE [App::DocumentObjectGroupPython] Se_element001  label="Se_element : 1"  # scripted group (container) (typed FeaturePython)
  n = 1
  ref = Se_element
FEATURE [App::DocumentObjectGroupPython] G4_Se  # scripted group (container) (typed FeaturePython)
  Dunit = g/cm3
  Dvalue = 4.5
  Group = -> [Se_element001]
  conduct = 2
  density = 1
  expand = 3
  formula = Se
  name = G4_Se
  specific = 4
FEATURE [App::DocumentObjectGroupPython] Br_element007  label="Br_element : 004"  # scripted group (container) (typed FeaturePython)
  n = 1
  ref = Br_element
FEATURE [App::DocumentObjectGroupPython] G4_Br  # scripted group (container) (typed FeaturePython)
  Dunit = g/cm3
  Dvalue = 0.0070721
  Group = -> [Br_element007]
  conduct = 2
  density = 1
  expand = 3
  formula = Br
  name = G4_Br
  specific = 4
FEATURE [App::DocumentObjectGroupPython] Kr_element001  label="Kr_element : 1"  # scripted group (container) (typed FeaturePython)
  n = 1
  ref = Kr_element
FEATURE [App::DocumentObjectGroupPython] G4_Kr  # scripted group (container) (typed FeaturePython)
  Dunit = g/cm3
  Dvalue = 0.00347832
  Group = -> [Kr_element001]
  conduct = 2
  density = 1
  expand = 3
  formula = Kr
  name = G4_Kr
  specific = 4
FEATURE [App::DocumentObjectGroupPython] Rb_element001  label="Rb_element : 1"  # scripted group (container) (typed FeaturePython)
  n = 1
  ref = Rb_element
FEATURE [App::DocumentObjectGroupPython] G4_Rb  # scripted group (container) (typed FeaturePython)
  Dunit = g/cm3
  Dvalue = 1.532
  Group = -> [Rb_element001]
  conduct = 2
  density = 1
  expand = 3
  formula = Rb
  name = G4_Rb
  specific = 4
FEATURE [App::DocumentObjectGroupPython] Sr_element001  label="Sr_element : 1"  # scripted group (container) (typed FeaturePython)
  n = 1
  ref = Sr_element
FEATURE [App::DocumentObjectGroupPython] G4_Sr  # scripted group (container) (typed FeaturePython)
  Dunit = g/cm3
  Dvalue = 2.54
  Group = -> [Sr_element001]
  conduct = 2
  density = 1
  expand = 3
  formula = Sr
  name = G4_Sr
  specific = 4
FEATURE [App::DocumentObjectGroupPython] Y_element001  label="Y_element : 1"  # scripted group (container) (typed FeaturePython)
  n = 1
  ref = Y_element
FEATURE [App::DocumentObjectGroupPython] G4_Y  # scripted group (container) (typed FeaturePython)
  Dunit = g/cm3
  Dvalue = 4.469
  Group = -> [Y_element001]
  conduct = 2
  density = 1
  expand = 3
  formula = Y
  name = G4_Y
  specific = 4
FEATURE [App::DocumentObjectGroupPython] Zr_element001  label="Zr_element : 1"  # scripted group (container) (typed FeaturePython)
  n = 1
  ref = Zr_element
FEATURE [App::DocumentObjectGroupPython] G4_Zr  # scripted group (container) (typed FeaturePython)
  Dunit = g/cm3
  Dvalue = 6.506
  Group = -> [Zr_element001]
  conduct = 2
  density = 1
  expand = 3
  formula = Zr
  name = G4_Zr
  specific = 4
FEATURE [App::DocumentObjectGroupPython] Nb_element001  label="Nb_element : 1"  # scripted group (container) (typed FeaturePython)
  n = 1
  ref = Nb_element
FEATURE [App::DocumentObjectGroupPython] G4_Nb  # scripted group (container) (typed FeaturePython)
  Dunit = g/cm3
  Dvalue = 8.57
  Group = -> [Nb_element001]
  conduct = 2
  density = 1
  expand = 3
  formula = Nb
  name = G4_Nb
  specific = 4
FEATURE [App::DocumentObjectGroupPython] Mo_element001  label="Mo_element : 1"  # scripted group (container) (typed FeaturePython)
  n = 1
  ref = Mo_element
FEATURE [App::DocumentObjectGroupPython] G4_Mo  # scripted group (container) (typed FeaturePython)
  Dunit = g/cm3
  Dvalue = 10.22
  Group = -> [Mo_element001]
  conduct = 2
  density = 1
  expand = 3
  formula = Mo
  name = G4_Mo
  specific = 4
FEATURE [App::DocumentObjectGroupPython] Tc_element001  label="Tc_element : 1"  # scripted group (container) (typed FeaturePython)
  n = 1
  ref = Tc_element
FEATURE [App::DocumentObjectGroupPython] G4_Tc  # scripted group (container) (typed FeaturePython)
  Dunit = g/cm3
  Dvalue = 11.5
  Group = -> [Tc_element001]
  conduct = 2
  density = 1
  expand = 3
  formula = Tc
  name = G4_Tc
  specific = 4
FEATURE [App::DocumentObjectGroupPython] Ru_element001  label="Ru_element : 1"  # scripted group (container) (typed FeaturePython)
  n = 1
  ref = Ru_element
FEATURE [App::DocumentObjectGroupPython] G4_Ru  # scripted group (container) (typed FeaturePython)
  Dunit = g/cm3
  Dvalue = 12.41
  Group = -> [Ru_element001]
  conduct = 2
  density = 1
  expand = 3
  formula = Ru
  name = G4_Ru
  specific = 4
FEATURE [App::DocumentObjectGroupPython] Rh_element001  label="Rh_element : 1"  # scripted group (container) (typed FeaturePython)
  n = 1
  ref = Rh_element
FEATURE [App::DocumentObjectGroupPython] G4_Rh  # scripted group (container) (typed FeaturePython)
  Dunit = g/cm3
  Dvalue = 12.41
  Group = -> [Rh_element001]
  conduct = 2
  density = 1
  expand = 3
  formula = Rh
  name = G4_Rh
  specific = 4
FEATURE [App::DocumentObjectGroupPython] Pd_element001  label="Pd_element : 1"  # scripted group (container) (typed FeaturePython)
  n = 1
  ref = Pd_element
FEATURE [App::DocumentObjectGroupPython] G4_Pd  # scripted group (container) (typed FeaturePython)
  Dunit = g/cm3
  Dvalue = 12.02
  Group = -> [Pd_element001]
  conduct = 2
  density = 1
  expand = 3
  formula = Pd
  name = G4_Pd
  specific = 4
FEATURE [App::DocumentObjectGroupPython] Ag_element006  label="Ag_element : 004"  # scripted group (container) (typed FeaturePython)
  n = 1
  ref = Ag_element
FEATURE [App::DocumentObjectGroupPython] G4_Ag  # scripted group (container) (typed FeaturePython)
  Dunit = g/cm3
  Dvalue = 10.5
  Group = -> [Ag_element006]
  conduct = 2
  density = 1
  expand = 3
  formula = Ag
  name = G4_Ag
  specific = 4
FEATURE [App::DocumentObjectGroupPython] Cd_element003  label="Cd_element : 003"  # scripted group (container) (typed FeaturePython)
  n = 1
  ref = Cd_element
FEATURE [App::DocumentObjectGroupPython] G4_Cd  # scripted group (container) (typed FeaturePython)
  Dunit = g/cm3
  Dvalue = 8.65
  Group = -> [Cd_element003]
  conduct = 2
  density = 1
  expand = 3
  formula = Cd
  name = G4_Cd
  specific = 4
FEATURE [App::DocumentObjectGroupPython] In_element001  label="In_element : 1"  # scripted group (container) (typed FeaturePython)
  n = 1
  ref = In_element
FEATURE [App::DocumentObjectGroupPython] G4_In  # scripted group (container) (typed FeaturePython)
  Dunit = g/cm3
  Dvalue = 7.31
  Group = -> [In_element001]
  conduct = 2
  density = 1
  expand = 3
  formula = In
  name = G4_In
  specific = 4
FEATURE [App::DocumentObjectGroupPython] Sn_element001  label="Sn_element : 1"  # scripted group (container) (typed FeaturePython)
  n = 1
  ref = Sn_element
FEATURE [App::DocumentObjectGroupPython] G4_Sn  # scripted group (container) (typed FeaturePython)
  Dunit = g/cm3
  Dvalue = 7.31
  Group = -> [Sn_element001]
  conduct = 2
  density = 1
  expand = 3
  formula = Sn
  name = G4_Sn
  specific = 4
FEATURE [App::DocumentObjectGroupPython] Sb_element001  label="Sb_element : 1"  # scripted group (container) (typed FeaturePython)
  n = 1
  ref = Sb_element
FEATURE [App::DocumentObjectGroupPython] G4_Sb  # scripted group (container) (typed FeaturePython)
  Dunit = g/cm3
  Dvalue = 6.691
  Group = -> [Sb_element001]
  conduct = 2
  density = 1
  expand = 3
  formula = Sb
  name = G4_Sb
  specific = 4
FEATURE [App::DocumentObjectGroupPython] Te_element002  label="Te_element : 002"  # scripted group (container) (typed FeaturePython)
  n = 1
  ref = Te_element
FEATURE [App::DocumentObjectGroupPython] G4_Te  # scripted group (container) (typed FeaturePython)
  Dunit = g/cm3
  Dvalue = 6.24
  Group = -> [Te_element002]
  conduct = 2
  density = 1
  expand = 3
  formula = Te
  name = G4_Te
  specific = 4
FEATURE [App::DocumentObjectGroupPython] I_element010  label="I_element : 006"  # scripted group (container) (typed FeaturePython)
  n = 1
  ref = I_element
FEATURE [App::DocumentObjectGroupPython] G4_I  # scripted group (container) (typed FeaturePython)
  Dunit = g/cm3
  Dvalue = 4.93
  Group = -> [I_element010]
  conduct = 2
  density = 1
  expand = 3
  formula = I
  name = G4_I
  specific = 4
FEATURE [App::DocumentObjectGroupPython] Xe_element001  label="Xe_element : 1"  # scripted group (container) (typed FeaturePython)
  n = 1
  ref = Xe_element
FEATURE [App::DocumentObjectGroupPython] G4_Xe  # scripted group (container) (typed FeaturePython)
  Dunit = g/cm3
  Dvalue = 0.00548536
  Group = -> [Xe_element001]
  conduct = 2
  density = 1
  expand = 3
  formula = Xe
  name = G4_Xe
  specific = 4
FEATURE [App::DocumentObjectGroupPython] Cs_element003  label="Cs_element : 003"  # scripted group (container) (typed FeaturePython)
  n = 1
  ref = Cs_element
FEATURE [App::DocumentObjectGroupPython] G4_Cs  # scripted group (container) (typed FeaturePython)
  Dunit = g/cm3
  Dvalue = 1.873
  Group = -> [Cs_element003]
  conduct = 2
  density = 1
  expand = 3
  formula = Cs
  name = G4_Cs
  specific = 4
FEATURE [App::DocumentObjectGroupPython] Ba_element003  label="Ba_element : 003"  # scripted group (container) (typed FeaturePython)
  n = 1
  ref = Ba_element
FEATURE [App::DocumentObjectGroupPython] G4_Ba  # scripted group (container) (typed FeaturePython)
  Dunit = g/cm3
  Dvalue = 3.5
  Group = -> [Ba_element003]
  conduct = 2
  density = 1
  expand = 3
  formula = Ba
  name = G4_Ba
  specific = 4
FEATURE [App::DocumentObjectGroupPython] La_element003  label="La_element : 003"  # scripted group (container) (typed FeaturePython)
  n = 1
  ref = La_element
FEATURE [App::DocumentObjectGroupPython] G4_La  # scripted group (container) (typed FeaturePython)
  Dunit = g/cm3
  Dvalue = 6.154
  Group = -> [La_element003]
  conduct = 2
  density = 1
  expand = 3
  formula = La
  name = G4_La
  specific = 4
FEATURE [App::DocumentObjectGroupPython] Ce_element002  label="Ce_element : 1"  # scripted group (container) (typed FeaturePython)
  n = 1
  ref = Ce_element
FEATURE [App::DocumentObjectGroupPython] G4_Ce  # scripted group (container) (typed FeaturePython)
  Dunit = g/cm3
  Dvalue = 6.657
  Group = -> [Ce_element002]
  conduct = 2
  density = 1
  expand = 3
  formula = Ce
  name = G4_Ce
  specific = 4
FEATURE [App::DocumentObjectGroupPython] Pr_element001  label="Pr_element : 1"  # scripted group (container) (typed FeaturePython)
  n = 1
  ref = Pr_element
FEATURE [App::DocumentObjectGroupPython] G4_Pr  # scripted group (container) (typed FeaturePython)
  Dunit = g/cm3
  Dvalue = 6.71
  Group = -> [Pr_element001]
  conduct = 2
  density = 1
  expand = 3
  formula = Pr
  name = G4_Pr
  specific = 4
FEATURE [App::DocumentObjectGroupPython] Nd_element001  label="Nd_element : 1"  # scripted group (container) (typed FeaturePython)
  n = 1
  ref = Nd_element
FEATURE [App::DocumentObjectGroupPython] G4_Nd  # scripted group (container) (typed FeaturePython)
  Dunit = g/cm3
  Dvalue = 6.9
  Group = -> [Nd_element001]
  conduct = 2
  density = 1
  expand = 3
  formula = Nd
  name = G4_Nd
  specific = 4
FEATURE [App::DocumentObjectGroupPython] Pm_element001  label="Pm_element : 1"  # scripted group (container) (typed FeaturePython)
  n = 1
  ref = Pm_element
FEATURE [App::DocumentObjectGroupPython] G4_Pm  # scripted group (container) (typed FeaturePython)
  Dunit = g/cm3
  Dvalue = 7.22
  Group = -> [Pm_element001]
  conduct = 2
  density = 1
  expand = 3
  formula = Pm
  name = G4_Pm
  specific = 4
FEATURE [App::DocumentObjectGroupPython] Sm_element001  label="Sm_element : 1"  # scripted group (container) (typed FeaturePython)
  n = 1
  ref = Sm_element
FEATURE [App::DocumentObjectGroupPython] G4_Sm  # scripted group (container) (typed FeaturePython)
  Dunit = g/cm3
  Dvalue = 7.46
  Group = -> [Sm_element001]
  conduct = 2
  density = 1
  expand = 3
  formula = Sm
  name = G4_Sm
  specific = 4
FEATURE [App::DocumentObjectGroupPython] Eu_element001  label="Eu_element : 1"  # scripted group (container) (typed FeaturePython)
  n = 1
  ref = Eu_element
FEATURE [App::DocumentObjectGroupPython] G4_Eu  # scripted group (container) (typed FeaturePython)
  Dunit = g/cm3
  Dvalue = 5.243
  Group = -> [Eu_element001]
  conduct = 2
  density = 1
  expand = 3
  formula = Eu
  name = G4_Eu
  specific = 4
FEATURE [App::DocumentObjectGroupPython] Gd_element002  label="Gd_element : 1"  # scripted group (container) (typed FeaturePython)
  n = 1
  ref = Gd_element
FEATURE [App::DocumentObjectGroupPython] G4_Gd  # scripted group (container) (typed FeaturePython)
  Dunit = g/cm3
  Dvalue = 7.9004
  Group = -> [Gd_element002]
  conduct = 2
  density = 1
  expand = 3
  formula = Gd
  name = G4_Gd
  specific = 4
FEATURE [App::DocumentObjectGroupPython] Tb_element001  label="Tb_element : 1"  # scripted group (container) (typed FeaturePython)
  n = 1
  ref = Tb_element
FEATURE [App::DocumentObjectGroupPython] G4_Tb  # scripted group (container) (typed FeaturePython)
  Dunit = g/cm3
  Dvalue = 8.229
  Group = -> [Tb_element001]
  conduct = 2
  density = 1
  expand = 3
  formula = Tb
  name = G4_Tb
  specific = 4
FEATURE [App::DocumentObjectGroupPython] Dy_element001  label="Dy_element : 1"  # scripted group (container) (typed FeaturePython)
  n = 1
  ref = Dy_element
FEATURE [App::DocumentObjectGroupPython] G4_Dy  # scripted group (container) (typed FeaturePython)
  Dunit = g/cm3
  Dvalue = 8.55
  Group = -> [Dy_element001]
  conduct = 2
  density = 1
  expand = 3
  formula = Dy
  name = G4_Dy
  specific = 4
FEATURE [App::DocumentObjectGroupPython] Ho_element001  label="Ho_element : 1"  # scripted group (container) (typed FeaturePython)
  n = 1
  ref = Ho_element
FEATURE [App::DocumentObjectGroupPython] G4_Ho  # scripted group (container) (typed FeaturePython)
  Dunit = g/cm3
  Dvalue = 8.795
  Group = -> [Ho_element001]
  conduct = 2
  density = 1
  expand = 3
  formula = Ho
  name = G4_Ho
  specific = 4
FEATURE [App::DocumentObjectGroupPython] Er_element001  label="Er_element : 1"  # scripted group (container) (typed FeaturePython)
  n = 1
  ref = Er_element
FEATURE [App::DocumentObjectGroupPython] G4_Er  # scripted group (container) (typed FeaturePython)
  Dunit = g/cm3
  Dvalue = 9.066
  Group = -> [Er_element001]
  conduct = 2
  density = 1
  expand = 3
  formula = Er
  name = G4_Er
  specific = 4
FEATURE [App::DocumentObjectGroupPython] Tm_element001  label="Tm_element : 1"  # scripted group (container) (typed FeaturePython)
  n = 1
  ref = Tm_element
FEATURE [App::DocumentObjectGroupPython] G4_Tm  # scripted group (container) (typed FeaturePython)
  Dunit = g/cm3
  Dvalue = 9.321
  Group = -> [Tm_element001]
  conduct = 2
  density = 1
  expand = 3
  formula = Tm
  name = G4_Tm
  specific = 4
FEATURE [App::DocumentObjectGroupPython] Yb_element001  label="Yb_element : 1"  # scripted group (container) (typed FeaturePython)
  n = 1
  ref = Yb_element
FEATURE [App::DocumentObjectGroupPython] G4_Yb  # scripted group (container) (typed FeaturePython)
  Dunit = g/cm3
  Dvalue = 6.73
  Group = -> [Yb_element001]
  conduct = 2
  density = 1
  expand = 3
  formula = Yb
  name = G4_Yb
  specific = 4
FEATURE [App::DocumentObjectGroupPython] Lu_element001  label="Lu_element : 1"  # scripted group (container) (typed FeaturePython)
  n = 1
  ref = Lu_element
FEATURE [App::DocumentObjectGroupPython] G4_Lu  # scripted group (container) (typed FeaturePython)
  Dunit = g/cm3
  Dvalue = 9.84
  Group = -> [Lu_element001]
  conduct = 2
  density = 1
  expand = 3
  formula = Lu
  name = G4_Lu
  specific = 4
FEATURE [App::DocumentObjectGroupPython] Hf_element001  label="Hf_element : 1"  # scripted group (container) (typed FeaturePython)
  n = 1
  ref = Hf_element
FEATURE [App::DocumentObjectGroupPython] G4_Hf  # scripted group (container) (typed FeaturePython)
  Dunit = g/cm3
  Dvalue = 13.31
  Group = -> [Hf_element001]
  conduct = 2
  density = 1
  expand = 3
  formula = Hf
  name = G4_Hf
  specific = 4
FEATURE [App::DocumentObjectGroupPython] Ta_element001  label="Ta_element : 1"  # scripted group (container) (typed FeaturePython)
  n = 1
  ref = Ta_element
FEATURE [App::DocumentObjectGroupPython] G4_Ta  # scripted group (container) (typed FeaturePython)
  Dunit = g/cm3
  Dvalue = 16.654
  Group = -> [Ta_element001]
  conduct = 2
  density = 1
  expand = 3
  formula = Ta
  name = G4_Ta
  specific = 4
FEATURE [App::DocumentObjectGroupPython] W_element004  label="W_element : 004"  # scripted group (container) (typed FeaturePython)
  n = 1
  ref = W_element
FEATURE [App::DocumentObjectGroupPython] G4_W  # scripted group (container) (typed FeaturePython)
  Dunit = g/cm3
  Dvalue = 19.3
  Group = -> [W_element004]
  conduct = 2
  density = 1
  expand = 3
  formula = W
  name = G4_W
  specific = 4
FEATURE [App::DocumentObjectGroupPython] Re_element001  label="Re_element : 1"  # scripted group (container) (typed FeaturePython)
  n = 1
  ref = Re_element
FEATURE [App::DocumentObjectGroupPython] G4_Re  # scripted group (container) (typed FeaturePython)
  Dunit = g/cm3
  Dvalue = 21.02
  Group = -> [Re_element001]
  conduct = 2
  density = 1
  expand = 3
  formula = Re
  name = G4_Re
  specific = 4
FEATURE [App::DocumentObjectGroupPython] Os_element001  label="Os_element : 1"  # scripted group (container) (typed FeaturePython)
  n = 1
  ref = Os_element
FEATURE [App::DocumentObjectGroupPython] G4_Os  # scripted group (container) (typed FeaturePython)
  Dunit = g/cm3
  Dvalue = 22.57
  Group = -> [Os_element001]
  conduct = 2
  density = 1
  expand = 3
  formula = Os
  name = G4_Os
  specific = 4
FEATURE [App::DocumentObjectGroupPython] Ir_element001  label="Ir_element : 1"  # scripted group (container) (typed FeaturePython)
  n = 1
  ref = Ir_element
FEATURE [App::DocumentObjectGroupPython] G4_Ir  # scripted group (container) (typed FeaturePython)
  Dunit = g/cm3
  Dvalue = 22.42
  Group = -> [Ir_element001]
  conduct = 2
  density = 1
  expand = 3
  formula = Ir
  name = G4_Ir
  specific = 4
FEATURE [App::DocumentObjectGroupPython] Pt_element001  label="Pt_element : 1"  # scripted group (container) (typed FeaturePython)
  n = 1
  ref = Pt_element
FEATURE [App::DocumentObjectGroupPython] G4_Pt  # scripted group (container) (typed FeaturePython)
  Dunit = g/cm3
  Dvalue = 21.45
  Group = -> [Pt_element001]
  conduct = 2
  density = 1
  expand = 3
  formula = Pt
  name = G4_Pt
  specific = 4
FEATURE [App::DocumentObjectGroupPython] Au_element001  label="Au_element : 1"  # scripted group (container) (typed FeaturePython)
  n = 1
  ref = Au_element
FEATURE [App::DocumentObjectGroupPython] G4_Au  # scripted group (container) (typed FeaturePython)
  Dunit = g/cm3
  Dvalue = 19.32
  Group = -> [Au_element001]
  conduct = 2
  density = 1
  expand = 3
  formula = Au
  name = G4_Au
  specific = 4
FEATURE [App::DocumentObjectGroupPython] Hg_element002  label="Hg_element : 002"  # scripted group (container) (typed FeaturePython)
  n = 1
  ref = Hg_element
FEATURE [App::DocumentObjectGroupPython] G4_Hg  # scripted group (container) (typed FeaturePython)
  Dunit = g/cm3
  Dvalue = 13.546
  Group = -> [Hg_element002]
  conduct = 2
  density = 1
  expand = 3
  formula = Hg
  name = G4_Hg
  specific = 4
FEATURE [App::DocumentObjectGroupPython] Tl_element002  label="Tl_element : 002"  # scripted group (container) (typed FeaturePython)
  n = 1
  ref = Tl_element
FEATURE [App::DocumentObjectGroupPython] G4_Tl  # scripted group (container) (typed FeaturePython)
  Dunit = g/cm3
  Dvalue = 11.72
  Group = -> [Tl_element002]
  conduct = 2
  density = 1
  expand = 3
  formula = Tl
  name = G4_Tl
  specific = 4
FEATURE [App::DocumentObjectGroupPython] Pb_element003  label="Pb_element : 1"  # scripted group (container) (typed FeaturePython)
  n = 1
  ref = Pb_element
FEATURE [App::DocumentObjectGroupPython] G4_Pb  # scripted group (container) (typed FeaturePython)
  Dunit = g/cm3
  Dvalue = 11.35
  Group = -> [Pb_element003]
  conduct = 2
  density = 1
  expand = 3
  formula = Pb
  name = G4_Pb
  specific = 4
FEATURE [App::DocumentObjectGroupPython] Bi_element002  label="Bi_element : 1"  # scripted group (container) (typed FeaturePython)
  n = 1
  ref = Bi_element
FEATURE [App::DocumentObjectGroupPython] G4_Bi  # scripted group (container) (typed FeaturePython)
  Dunit = g/cm3
  Dvalue = 9.747
  Group = -> [Bi_element002]
  conduct = 2
  density = 1
  expand = 3
  formula = Bi
  name = G4_Bi
  specific = 4
FEATURE [App::DocumentObjectGroupPython] Po_element001  label="Po_element : 1"  # scripted group (container) (typed FeaturePython)
  n = 1
  ref = Po_element
FEATURE [App::DocumentObjectGroupPython] G4_Po  # scripted group (container) (typed FeaturePython)
  Dunit = g/cm3
  Dvalue = 9.32
  Group = -> [Po_element001]
  conduct = 2
  density = 1
  expand = 3
  formula = Po
  name = G4_Po
  specific = 4
FEATURE [App::DocumentObjectGroupPython] At_element001  label="At_element : 1"  # scripted group (container) (typed FeaturePython)
  n = 1
  ref = At_element
FEATURE [App::DocumentObjectGroupPython] G4_At  # scripted group (container) (typed FeaturePython)
  Dunit = g/cm3
  Dvalue = 9.32
  Group = -> [At_element001]
  conduct = 2
  density = 1
  expand = 3
  formula = At
  name = G4_At
  specific = 4
FEATURE [App::DocumentObjectGroupPython] Rn_element001  label="Rn_element : 1"  # scripted group (container) (typed FeaturePython)
  n = 1
  ref = Rn_element
FEATURE [App::DocumentObjectGroupPython] G4_Rn  # scripted group (container) (typed FeaturePython)
  Dunit = g/cm3
  Dvalue = 0.00900662
  Group = -> [Rn_element001]
  conduct = 2
  density = 1
  expand = 3
  formula = Rn
  name = G4_Rn
  specific = 4
FEATURE [App::DocumentObjectGroupPython] Fr_element001  label="Fr_element : 1"  # scripted group (container) (typed FeaturePython)
  n = 1
  ref = Fr_element
FEATURE [App::DocumentObjectGroupPython] G4_Fr  # scripted group (container) (typed FeaturePython)
  Dunit = g/cm3
  Dvalue = 1
  Group = -> [Fr_element001]
  conduct = 2
  density = 1
  expand = 3
  formula = Fr
  name = G4_Fr
  specific = 4
FEATURE [App::DocumentObjectGroupPython] Ra_element001  label="Ra_element : 1"  # scripted group (container) (typed FeaturePython)
  n = 1
  ref = Ra_element
FEATURE [App::DocumentObjectGroupPython] G4_Ra  # scripted group (container) (typed FeaturePython)
  Dunit = g/cm3
  Dvalue = 5
  Group = -> [Ra_element001]
  conduct = 2
  density = 1
  expand = 3
  formula = Ra
  name = G4_Ra
  specific = 4
FEATURE [App::DocumentObjectGroupPython] Ac_element001  label="Ac_element : 1"  # scripted group (container) (typed FeaturePython)
  n = 1
  ref = Ac_element
FEATURE [App::DocumentObjectGroupPython] G4_Ac  # scripted group (container) (typed FeaturePython)
  Dunit = g/cm3
  Dvalue = 10.07
  Group = -> [Ac_element001]
  conduct = 2
  density = 1
  expand = 3
  formula = Ac
  name = G4_Ac
  specific = 4
FEATURE [App::DocumentObjectGroupPython] Th_element001  label="Th_element : 1"  # scripted group (container) (typed FeaturePython)
  n = 1
  ref = Th_element
FEATURE [App::DocumentObjectGroupPython] G4_Th  # scripted group (container) (typed FeaturePython)
  Dunit = g/cm3
  Dvalue = 11.72
  Group = -> [Th_element001]
  conduct = 2
  density = 1
  expand = 3
  formula = Th
  name = G4_Th
  specific = 4
FEATURE [App::DocumentObjectGroupPython] Pa_element001  label="Pa_element : 1"  # scripted group (container) (typed FeaturePython)
  n = 1
  ref = Pa_element
FEATURE [App::DocumentObjectGroupPython] G4_Pa  # scripted group (container) (typed FeaturePython)
  Dunit = g/cm3
  Dvalue = 15.37
  Group = -> [Pa_element001]
  conduct = 2
  density = 1
  expand = 3
  formula = Pa
  name = G4_Pa
  specific = 4
FEATURE [App::DocumentObjectGroupPython] U_element004  label="U_element : 004"  # scripted group (container) (typed FeaturePython)
  n = 1
  ref = U_element
FEATURE [App::DocumentObjectGroupPython] G4_U  # scripted group (container) (typed FeaturePython)
  Dunit = g/cm3
  Dvalue = 18.95
  Group = -> [U_element004]
  conduct = 2
  density = 1
  expand = 3
  formula = U
  name = G4_U
  specific = 4
FEATURE [App::DocumentObjectGroupPython] Np_element001  label="Np_element : 1"  # scripted group (container) (typed FeaturePython)
  n = 1
  ref = Np_element
FEATURE [App::DocumentObjectGroupPython] G4_Np  # scripted group (container) (typed FeaturePython)
  Dunit = g/cm3
  Dvalue = 20.25
  Group = -> [Np_element001]
  conduct = 2
  density = 1
  expand = 3
  formula = Np
  name = G4_Np
  specific = 4
FEATURE [App::DocumentObjectGroupPython] Pu_element002  label="Pu_element : 002"  # scripted group (container) (typed FeaturePython)
  n = 1
  ref = Pu_element
FEATURE [App::DocumentObjectGroupPython] G4_Pu  # scripted group (container) (typed FeaturePython)
  Dunit = g/cm3
  Dvalue = 19.84
  Group = -> [Pu_element002]
  conduct = 2
  density = 1
  expand = 3
  formula = Pu
  name = G4_Pu
  specific = 4
FEATURE [App::DocumentObjectGroupPython] Am_element001  label="Am_element : 1"  # scripted group (container) (typed FeaturePython)
  n = 1
  ref = Am_element
FEATURE [App::DocumentObjectGroupPython] G4_Am  # scripted group (container) (typed FeaturePython)
  Dunit = g/cm3
  Dvalue = 13.67
  Group = -> [Am_element001]
  conduct = 2
  density = 1
  expand = 3
  formula = Am
  name = G4_Am
  specific = 4
FEATURE [App::DocumentObjectGroupPython] Cm_element001  label="Cm_element : 1"  # scripted group (container) (typed FeaturePython)
  n = 1
  ref = Cm_element
FEATURE [App::DocumentObjectGroupPython] G4_Cm  # scripted group (container) (typed FeaturePython)
  Dunit = g/cm3
  Dvalue = 13.51
  Group = -> [Cm_element001]
  conduct = 2
  density = 1
  expand = 3
  formula = Cm
  name = G4_Cm
  specific = 4
FEATURE [App::DocumentObjectGroupPython] Bk_element001  label="Bk_element : 1"  # scripted group (container) (typed FeaturePython)
  n = 1
  ref = Bk_element
FEATURE [App::DocumentObjectGroupPython] G4_Bk  # scripted group (container) (typed FeaturePython)
  Dunit = g/cm3
  Dvalue = 14
  Group = -> [Bk_element001]
  conduct = 2
  density = 1
  expand = 3
  formula = Bk
  name = G4_Bk
  specific = 4
FEATURE [App::DocumentObjectGroupPython] Cf_element001  label="Cf_element : 1"  # scripted group (container) (typed FeaturePython)
  n = 1
  ref = Cf_element
FEATURE [App::DocumentObjectGroupPython] G4_Cf  # scripted group (container) (typed FeaturePython)
  Dunit = g/cm3
  Dvalue = 10
  Group = -> [Cf_element001]
  conduct = 2
  density = 1
  expand = 3
  formula = Cf
  name = G4_Cf
  specific = 4
FEATURE [App::DocumentObjectGroupPython] Element  # scripted group (container) (typed FeaturePython)
  Group = -> [G4_H,G4_He,G4_Li,G4_Be,G4_B,G4_C,G4_N,G4_O,G4_F,G4_Ne,G4_Na,G4_Mg,G4_Al,G4_Si,G4_P,G4_S,G4_Cl,G4_Ar,G4_K,G4_Ca,G4_Sc,G4_Ti,G4_V,G4_Cr,G4_Mn,G4_Fe,G4_Co,G4_Ni,G4_Cu,G4_Zn,G4_Ga,G4_Ge,G4_As,G4_Se,G4_Br,G4_Kr,G4_Rb,G4_Sr,G4_Y,G4_Zr,G4_Nb,G4_Mo,G4_Tc,G4_Ru,G4_Rh,G4_Pd,G4_Ag,G4_Cd,G4_In,G4_Sn,G4_Sb,G4_Te,G4_I,G4_Xe,G4_Cs,G4_Ba,G4_La,G4_Ce,G4_Pr,G4_Nd,G4_Pm,G4_Sm,G4_Eu,G4_Gd,G4_Tb,G4_Dy,G4_Ho,G4_Er,+30 more]
FEATURE [App::DocumentObjectGroupPython] H_element114  label="H_element : 063"  # scripted group (container) (typed FeaturePython)
  n = 2
  ref = H_element
FEATURE [App::DocumentObjectGroupPython] G4_lH2  # scripted group (container) (typed FeaturePython)
  Dunit = g/cm3
  Dvalue = 0.0708
  Group = -> [H_element114]
  conduct = 2
  density = 1
  expand = 3
  formula = G4_lH2
  name = G4_lH2
  specific = 4
FEATURE [App::DocumentObjectGroupPython] N_element049  label="N_element : 022"  # scripted group (container) (typed FeaturePython)
  n = 2
  ref = N_element
FEATURE [App::DocumentObjectGroupPython] G4_lN2  # scripted group (container) (typed FeaturePython)
  Dunit = g/cm3
  Dvalue = 0.807
  Group = -> [N_element049]
  conduct = 2
  density = 1
  expand = 3
  formula = G4_lN2
  name = G4_lN2
  specific = 4
FEATURE [App::DocumentObjectGroupPython] O_element106  label="O_element : 060"  # scripted group (container) (typed FeaturePython)
  n = 2
  ref = O_element
FEATURE [App::DocumentObjectGroupPython] G4_lO2  # scripted group (container) (typed FeaturePython)
  Dunit = g/cm3
  Dvalue = 1.141
  Group = -> [O_element106]
  conduct = 2
  density = 1
  expand = 3
  formula = G4_lO2
  name = G4_lO2
  specific = 4
FEATURE [App::DocumentObjectGroupPython] Ar  label="Ar : 1"  # scripted group (container) (typed FeaturePython)
  n = 1
  ref = Ar
FEATURE [App::DocumentObjectGroupPython] G4_lAr  # scripted group (container) (typed FeaturePython)
  Dunit = g/cm3
  Dvalue = 1.396
  Group = -> [Ar]
  conduct = 2
  density = 1
  expand = 3
  formula = G4_lAr
  name = G4_lAr
  specific = 4
FEATURE [App::DocumentObjectGroupPython] Br  label="Br : 1"  # scripted group (container) (typed FeaturePython)
  n = 1
  ref = Br
FEATURE [App::DocumentObjectGroupPython] G4_lBr  # scripted group (container) (typed FeaturePython)
  Dunit = g/cm3
  Dvalue = 3.1028
  Group = -> [Br]
  conduct = 2
  density = 1
  expand = 3
  formula = G4_lBr
  name = G4_lBr
  specific = 4
FEATURE [App::DocumentObjectGroupPython] Kr  label="Kr : 1"  # scripted group (container) (typed FeaturePython)
  n = 1
  ref = Kr
FEATURE [App::DocumentObjectGroupPython] G4_lKr  # scripted group (container) (typed FeaturePython)
  Dunit = g/cm3
  Dvalue = 2.418
  Group = -> [Kr]
  conduct = 2
  density = 1
  expand = 3
  formula = G4_lKr
  name = G4_lKr
  specific = 4
FEATURE [App::DocumentObjectGroupPython] Xe  label="Xe : 1"  # scripted group (container) (typed FeaturePython)
  n = 1
  ref = Xe
FEATURE [App::DocumentObjectGroupPython] G4_lXe  # scripted group (container) (typed FeaturePython)
  Dunit = g/cm3
  Dvalue = 2.953
  Group = -> [Xe]
  conduct = 2
  density = 1
  expand = 3
  formula = G4_lXe
  name = G4_lXe
  specific = 4
FEATURE [App::DocumentObjectGroupPython] O_element107  label="O_element : 061"  # scripted group (container) (typed FeaturePython)
  n = 4
  ref = O_element
FEATURE [App::DocumentObjectGroupPython] Pb_element004  label="Pb_element : 002"  # scripted group (container) (typed FeaturePython)
  n = 1
  ref = Pb_element
FEATURE [App::DocumentObjectGroupPython] W_element005  label="W_element : 005"  # scripted group (container) (typed FeaturePython)
  n = 1
  ref = W_element
FEATURE [App::DocumentObjectGroupPython] G4_PbWO4  # scripted group (container) (typed FeaturePython)
  Dunit = g/cm3
  Dvalue = 8.28
  Group = -> [O_element107,Pb_element004,W_element005]
  conduct = 2
  density = 1
  expand = 3
  formula = G4_PbWO4
  name = G4_PbWO4
  specific = 4
FEATURE [App::DocumentObjectGroupPython] alactic  label="alactic : 1"  # scripted group (container) (typed FeaturePython)
  n = 1
  ref = alactic
FEATURE [App::DocumentObjectGroupPython] G4_Galactic  # scripted group (container) (typed FeaturePython)
  Dunit = g/cm3
  Dvalue = 0
  Group = -> [alactic]
  conduct = 2
  density = 1
  expand = 3
  formula = G4_Galactic
  name = G4_Galactic
  specific = 4
FEATURE [App::DocumentObjectGroupPython] RAPHITE_POROUS  label="RAPHITE_POROUS : 1"  # scripted group (container) (typed FeaturePython)
  n = 1
  ref = RAPHITE_POROUS
FEATURE [App::DocumentObjectGroupPython] G4_GRAPHITE_POROUS  # scripted group (container) (typed FeaturePython)
  Dunit = g/cm3
  Dvalue = 1.7
  Group = -> [RAPHITE_POROUS]
  conduct = 2
  density = 1
  expand = 3
  formula = G4_GRAPHITE_POROUS
  name = G4_GRAPHITE_POROUS
  specific = 4
FEATURE [App::DocumentObjectGroupPython] H_element115  label="H_element : 0.150"  # scripted group (container) (typed FeaturePython)
  n = 0.080538
FEATURE [App::DocumentObjectGroupPython] C_element125  label="C_element : 0.600"  # scripted group (container) (typed FeaturePython)
  n = 0.599848
FEATURE [App::DocumentObjectGroupPython] O_element108  label="O_element : 0.320"  # scripted group (container) (typed FeaturePython)
  n = 0.319614
FEATURE [App::DocumentObjectGroupPython] G4_LUCITE  # scripted group (container) (typed FeaturePython)
  Dunit = g/cm3
  Dvalue = 1.19
  Group = -> [H_element115,C_element125,O_element108]
  conduct = 2
  density = 1
  expand = 3
  formula = G4_LUCITE
  name = G4_LUCITE
  specific = 4
FEATURE [App::DocumentObjectGroupPython] Cu_element002  label="Cu_element : 62"  # scripted group (container) (typed FeaturePython)
  n = 62
  ref = Cu_element
FEATURE [App::DocumentObjectGroupPython] Zn_element002  label="Zn_element : 35"  # scripted group (container) (typed FeaturePython)
  n = 35
  ref = Zn_element
FEATURE [App::DocumentObjectGroupPython] Pb_element005  label="Pb_element : 3"  # scripted group (container) (typed FeaturePython)
  n = 3
  ref = Pb_element
FEATURE [App::DocumentObjectGroupPython] G4_BRASS  # scripted group (container) (typed FeaturePython)
  Dunit = g/cm3
  Dvalue = 8.52
  Group = -> [Cu_element002,Zn_element002,Pb_element005]
  conduct = 2
  density = 1
  expand = 3
  formula = G4_BRASS
  name = G4_BRASS
  specific = 4
FEATURE [App::DocumentObjectGroupPython] Cu_element003  label="Cu_element : 89"  # scripted group (container) (typed FeaturePython)
  n = 89
  ref = Cu_element
FEATURE [App::DocumentObjectGroupPython] Zn_element003  label="Zn_element : 9"  # scripted group (container) (typed FeaturePython)
  n = 9
  ref = Zn_element
FEATURE [App::DocumentObjectGroupPython] Pb_element006  label="Pb_element : 2"  # scripted group (container) (typed FeaturePython)
  n = 2
  ref = Pb_element
FEATURE [App::DocumentObjectGroupPython] G4_BRONZE  # scripted group (container) (typed FeaturePython)
  Dunit = g/cm3
  Dvalue = 8.82
  Group = -> [Cu_element003,Zn_element003,Pb_element006]
  conduct = 2
  density = 1
  expand = 3
  formula = G4_BRONZE
  name = G4_BRONZE
  specific = 4
FEATURE [App::DocumentObjectGroupPython] Fe_element008  label="Fe_element : 74"  # scripted group (container) (typed FeaturePython)
  n = 74
  ref = Fe_element
FEATURE [App::DocumentObjectGroupPython] Cr_element002  label="Cr_element : 18"  # scripted group (container) (typed FeaturePython)
  n = 18
  ref = Cr_element
FEATURE [App::DocumentObjectGroupPython] Ni_element002  label="Ni_element : 8"  # scripted group (container) (typed FeaturePython)
  n = 8
  ref = Ni_element
FEATURE [App::DocumentObjectGroupPython] G4_STAINLESS_STEEL  label="G4_STAINLESS-STEEL"  # scripted group (container) (typed FeaturePython)
  Dunit = g/cm3
  Dvalue = 8
  Group = -> [Fe_element008,Cr_element002,Ni_element002]
  conduct = 2
  density = 1
  expand = 3
  formula = G4_STAINLESS-STEEL
  name = G4_STAINLESS-STEEL
  specific = 4
FEATURE [App::DocumentObjectGroupPython] H_element116  label="H_element : 064"  # scripted group (container) (typed FeaturePython)
  n = 18
  ref = H_element
FEATURE [App::DocumentObjectGroupPython] C_element126  label="C_element : 071"  # scripted group (container) (typed FeaturePython)
  n = 12
  ref = C_element
FEATURE [App::DocumentObjectGroupPython] O_element109  label="O_element : 062"  # scripted group (container) (typed FeaturePython)
  n = 7
  ref = O_element
FEATURE [App::DocumentObjectGroupPython] G4_CR39  # scripted group (container) (typed FeaturePython)
  Dunit = g/cm3
  Dvalue = 1.32
  Group = -> [H_element116,C_element126,O_element109]
  conduct = 2
  density = 1
  expand = 3
  formula = G4_CR39
  name = G4_CR39
  specific = 4
FEATURE [App::DocumentObjectGroupPython] H_element117  label="H_element : 38"  # scripted group (container) (typed FeaturePython)
  n = 38
  ref = H_element
FEATURE [App::DocumentObjectGroupPython] C_element127  label="C_element : 072"  # scripted group (container) (typed FeaturePython)
  n = 18
  ref = C_element
FEATURE [App::DocumentObjectGroupPython] O_element110  label="O_element : 063"  # scripted group (container) (typed FeaturePython)
  n = 1
  ref = O_element
FEATURE [App::DocumentObjectGroupPython] G4_OCTADECANOL  # scripted group (container) (typed FeaturePython)
  Dunit = g/cm3
  Dvalue = 0.812
  Group = -> [H_element117,C_element127,O_element110]
  conduct = 2
  density = 1
  expand = 3
  formula = G4_OCTADECANOL
  name = G4_OCTADECANOL
  specific = 4
FEATURE [App::DocumentObjectGroupPython] HEP  # scripted group (container) (typed FeaturePython)
  Group = -> [G4_lH2,G4_lN2,G4_lO2,G4_lAr,G4_lBr,G4_lKr,G4_lXe,G4_PbWO4,G4_Galactic,G4_GRAPHITE_POROUS,G4_LUCITE,G4_BRASS,G4_BRONZE,G4_STAINLESS_STEEL,G4_CR39,G4_OCTADECANOL]
FEATURE [App::DocumentObjectGroupPython] C_element128  label="C_element : 073"  # scripted group (container) (typed FeaturePython)
  n = 14
  ref = C_element
FEATURE [App::DocumentObjectGroupPython] H_element118  label="H_element : 065"  # scripted group (container) (typed FeaturePython)
  n = 10
  ref = H_element
FEATURE [App::DocumentObjectGroupPython] O_element111  label="O_element : 064"  # scripted group (container) (typed FeaturePython)
  n = 2
  ref = O_element
FEATURE [App::DocumentObjectGroupPython] N_element050  label="N_element : 023"  # scripted group (container) (typed FeaturePython)
  n = 2
  ref = N_element
FEATURE [App::DocumentObjectGroupPython] G4_KEVLAR  # scripted group (container) (typed FeaturePython)
  Dunit = g/cm3
  Dvalue = 1.44
  Group = -> [C_element128,H_element118,O_element111,N_element050]
  conduct = 2
  density = 1
  expand = 3
  formula = G4_KEVLAR
  name = G4_KEVLAR
  specific = 4
FEATURE [App::DocumentObjectGroupPython] C_element129  label="C_element : 074"  # scripted group (container) (typed FeaturePython)
  n = 10
  ref = C_element
FEATURE [App::DocumentObjectGroupPython] H_element119  label="H_element : 066"  # scripted group (container) (typed FeaturePython)
  n = 8
  ref = H_element
FEATURE [App::DocumentObjectGroupPython] O_element112  label="O_element : 065"  # scripted group (container) (typed FeaturePython)
  n = 4
  ref = O_element
FEATURE [App::DocumentObjectGroupPython] G4_DACRON  # scripted group (container) (typed FeaturePython)
  Dunit = g/cm3
  Dvalue = 1.4
  Group = -> [C_element129,H_element119,O_element112]
  conduct = 2
  density = 1
  expand = 3
  formula = G4_DACRON
  name = G4_DACRON
  specific = 4
FEATURE [App::DocumentObjectGroupPython] C_element130  label="C_element : 075"  # scripted group (container) (typed FeaturePython)
  n = 4
  ref = C_element
FEATURE [App::DocumentObjectGroupPython] H_element120  label="H_element : 067"  # scripted group (container) (typed FeaturePython)
  n = 5
  ref = H_element
FEATURE [App::DocumentObjectGroupPython] Cl_element030  label="Cl_element : 016"  # scripted group (container) (typed FeaturePython)
  n = 1
  ref = Cl_element
FEATURE [App::DocumentObjectGroupPython] G4_NEOPRENE  # scripted group (container) (typed FeaturePython)
  Dunit = g/cm3
  Dvalue = 1.23
  Group = -> [C_element130,H_element120,Cl_element030]
  conduct = 2
  density = 1
  expand = 3
  formula = G4_NEOPRENE
  name = G4_NEOPRENE
  specific = 4
FEATURE [App::DocumentObjectGroupPython] Space  # scripted group (container) (typed FeaturePython)
  Group = -> [G4_KEVLAR,G4_DACRON,G4_NEOPRENE]
FEATURE [App::DocumentObjectGroupPython] H_element121  label="H_element : 068"  # scripted group (container) (typed FeaturePython)
  n = 5
  ref = H_element
FEATURE [App::DocumentObjectGroupPython] C_element131  label="C_element : 076"  # scripted group (container) (typed FeaturePython)
  n = 4
  ref = C_element
FEATURE [App::DocumentObjectGroupPython] N_element051  label="N_element : 3"  # scripted group (container) (typed FeaturePython)
  n = 3
  ref = N_element
FEATURE [App::DocumentObjectGroupPython] O_element113  label="O_element : 066"  # scripted group (container) (typed FeaturePython)
  n = 1
  ref = O_element
FEATURE [App::DocumentObjectGroupPython] G4_CYTOSINE  # scripted group (container) (typed FeaturePython)
  Dunit = g/cm3
  Dvalue = 1.55
  Group = -> [H_element121,C_element131,N_element051,O_element113]
  conduct = 2
  density = 1
  expand = 3
  formula = G4_CYTOSINE
  name = G4_CYTOSINE
  specific = 4
FEATURE [App::DocumentObjectGroupPython] H_element122  label="H_element : 069"  # scripted group (container) (typed FeaturePython)
  n = 6
  ref = H_element
FEATURE [App::DocumentObjectGroupPython] C_element132  label="C_element : 077"  # scripted group (container) (typed FeaturePython)
  n = 5
  ref = C_element
FEATURE [App::DocumentObjectGroupPython] N_element052  label="N_element : 024"  # scripted group (container) (typed FeaturePython)
  n = 2
  ref = N_element
FEATURE [App::DocumentObjectGroupPython] O_element114  label="O_element : 067"  # scripted group (container) (typed FeaturePython)
  n = 2
  ref = O_element
FEATURE [App::DocumentObjectGroupPython] G4_THYMINE  # scripted group (container) (typed FeaturePython)
  Dunit = g/cm3
  Dvalue = 1.23
  Group = -> [H_element122,C_element132,N_element052,O_element114]
  conduct = 2
  density = 1
  expand = 3
  formula = G4_THYMINE
  name = G4_THYMINE
  specific = 4
FEATURE [App::DocumentObjectGroupPython] H_element123  label="H_element : 070"  # scripted group (container) (typed FeaturePython)
  n = 4
  ref = H_element
FEATURE [App::DocumentObjectGroupPython] C_element133  label="C_element : 078"  # scripted group (container) (typed FeaturePython)
  n = 4
  ref = C_element
FEATURE [App::DocumentObjectGroupPython] N_element053  label="N_element : 025"  # scripted group (container) (typed FeaturePython)
  n = 2
  ref = N_element
FEATURE [App::DocumentObjectGroupPython] O_element115  label="O_element : 068"  # scripted group (container) (typed FeaturePython)
  n = 2
  ref = O_element
FEATURE [App::DocumentObjectGroupPython] G4_URACIL  # scripted group (container) (typed FeaturePython)
  Dunit = g/cm3
  Dvalue = 1.32
  Group = -> [H_element123,C_element133,N_element053,O_element115]
  conduct = 2
  density = 1
  expand = 3
  formula = G4_URACIL
  name = G4_URACIL
  specific = 4
FEATURE [App::DocumentObjectGroupPython] H_element124  label="H_element : 071"  # scripted group (container) (typed FeaturePython)
  n = 4
  ref = H_element
FEATURE [App::DocumentObjectGroupPython] C_element134  label="C_element : 079"  # scripted group (container) (typed FeaturePython)
  n = 5
  ref = C_element
FEATURE [App::DocumentObjectGroupPython] N_element054  label="N_element : 026"  # scripted group (container) (typed FeaturePython)
  n = 5
  ref = N_element
FEATURE [App::DocumentObjectGroupPython] G4_DNA_ADENINE  # scripted group (container) (typed FeaturePython)
  Dunit = g/cm3
  Dvalue = 1
  Group = -> [H_element124,C_element134,N_element054]
  conduct = 2
  density = 1
  expand = 3
  formula = G4_DNA_ADENINE
  name = G4_DNA_ADENINE
  specific = 4
FEATURE [App::DocumentObjectGroupPython] H_element125  label="H_element : 072"  # scripted group (container) (typed FeaturePython)
  n = 4
  ref = H_element
FEATURE [App::DocumentObjectGroupPython] C_element135  label="C_element : 080"  # scripted group (container) (typed FeaturePython)
  n = 5
  ref = C_element
FEATURE [App::DocumentObjectGroupPython] N_element055  label="N_element : 027"  # scripted group (container) (typed FeaturePython)
  n = 5
  ref = N_element
FEATURE [App::DocumentObjectGroupPython] O_element116  label="O_element : 069"  # scripted group (container) (typed FeaturePython)
  n = 1
  ref = O_element
FEATURE [App::DocumentObjectGroupPython] G4_DNA_GUANINE  # scripted group (container) (typed FeaturePython)
  Dunit = g/cm3
  Dvalue = 1
  Group = -> [H_element125,C_element135,N_element055,O_element116]
  conduct = 2
  density = 1
  expand = 3
  formula = G4_DNA_GUANINE
  name = G4_DNA_GUANINE
  specific = 4
FEATURE [App::DocumentObjectGroupPython] H_element126  label="H_element : 073"  # scripted group (container) (typed FeaturePython)
  n = 4
  ref = H_element
FEATURE [App::DocumentObjectGroupPython] C_element136  label="C_element : 081"  # scripted group (container) (typed FeaturePython)
  n = 4
  ref = C_element
FEATURE [App::DocumentObjectGroupPython] N_element056  label="N_element : 028"  # scripted group (container) (typed FeaturePython)
  n = 3
  ref = N_element
FEATURE [App::DocumentObjectGroupPython] O_element117  label="O_element : 070"  # scripted group (container) (typed FeaturePython)
  n = 1
  ref = O_element
FEATURE [App::DocumentObjectGroupPython] G4_DNA_CYTOSINE  # scripted group (container) (typed FeaturePython)
  Dunit = g/cm3
  Dvalue = 1
  Group = -> [H_element126,C_element136,N_element056,O_element117]
  conduct = 2
  density = 1
  expand = 3
  formula = G4_DNA_CYTOSINE
  name = G4_DNA_CYTOSINE
  specific = 4
FEATURE [App::DocumentObjectGroupPython] H_element127  label="H_element : 074"  # scripted group (container) (typed FeaturePython)
  n = 5
  ref = H_element
FEATURE [App::DocumentObjectGroupPython] C_element137  label="C_element : 082"  # scripted group (container) (typed FeaturePython)
  n = 5
  ref = C_element
FEATURE [App::DocumentObjectGroupPython] N_element057  label="N_element : 029"  # scripted group (container) (typed FeaturePython)
  n = 2
  ref = N_element
FEATURE [App::DocumentObjectGroupPython] O_element118  label="O_element : 071"  # scripted group (container) (typed FeaturePython)
  n = 2
  ref = O_element
FEATURE [App::DocumentObjectGroupPython] G4_DNA_THYMINE  # scripted group (container) (typed FeaturePython)
  Dunit = g/cm3
  Dvalue = 1
  Group = -> [H_element127,C_element137,N_element057,O_element118]
  conduct = 2
  density = 1
  expand = 3
  formula = G4_DNA_THYMINE
  name = G4_DNA_THYMINE
  specific = 4
FEATURE [App::DocumentObjectGroupPython] H_element128  label="H_element : 075"  # scripted group (container) (typed FeaturePython)
  n = 3
  ref = H_element
FEATURE [App::DocumentObjectGroupPython] C_element138  label="C_element : 083"  # scripted group (container) (typed FeaturePython)
  n = 4
  ref = C_element
FEATURE [App::DocumentObjectGroupPython] N_element058  label="N_element : 030"  # scripted group (container) (typed FeaturePython)
  n = 2
  ref = N_element
FEATURE [App::DocumentObjectGroupPython] O_element119  label="O_element : 072"  # scripted group (container) (typed FeaturePython)
  n = 2
  ref = O_element
FEATURE [App::DocumentObjectGroupPython] G4_DNA_URACIL  # scripted group (container) (typed FeaturePython)
  Dunit = g/cm3
  Dvalue = 1
  Group = -> [H_element128,C_element138,N_element058,O_element119]
  conduct = 2
  density = 1
  expand = 3
  formula = G4_DNA_URACIL
  name = G4_DNA_URACIL
  specific = 4
FEATURE [App::DocumentObjectGroupPython] H_element129  label="H_element : 076"  # scripted group (container) (typed FeaturePython)
  n = 10
  ref = H_element
FEATURE [App::DocumentObjectGroupPython] C_element139  label="C_element : 084"  # scripted group (container) (typed FeaturePython)
  n = 10
  ref = C_element
FEATURE [App::DocumentObjectGroupPython] N_element059  label="N_element : 031"  # scripted group (container) (typed FeaturePython)
  n = 5
  ref = N_element
FEATURE [App::DocumentObjectGroupPython] O_element120  label="O_element : 073"  # scripted group (container) (typed FeaturePython)
  n = 4
  ref = O_element
FEATURE [App::DocumentObjectGroupPython] G4_DNA_ADENOSINE  # scripted group (container) (typed FeaturePython)
  Dunit = g/cm3
  Dvalue = 1
  Group = -> [H_element129,C_element139,N_element059,O_element120]
  conduct = 2
  density = 1
  expand = 3
  formula = G4_DNA_ADENOSINE
  name = G4_DNA_ADENOSINE
  specific = 4
FEATURE [App::DocumentObjectGroupPython] H_element130  label="H_element : 077"  # scripted group (container) (typed FeaturePython)
  n = 10
  ref = H_element
FEATURE [App::DocumentObjectGroupPython] C_element140  label="C_element : 085"  # scripted group (container) (typed FeaturePython)
  n = 10
  ref = C_element
FEATURE [App::DocumentObjectGroupPython] N_element060  label="N_element : 032"  # scripted group (container) (typed FeaturePython)
  n = 5
  ref = N_element
FEATURE [App::DocumentObjectGroupPython] O_element121  label="O_element : 074"  # scripted group (container) (typed FeaturePython)
  n = 5
  ref = O_element
FEATURE [App::DocumentObjectGroupPython] G4_DNA_GUANOSINE  # scripted group (container) (typed FeaturePython)
  Dunit = g/cm3
  Dvalue = 1
  Group = -> [H_element130,C_element140,N_element060,O_element121]
  conduct = 2
  density = 1
  expand = 3
  formula = G4_DNA_GUANOSINE
  name = G4_DNA_GUANOSINE
  specific = 4
FEATURE [App::DocumentObjectGroupPython] H_element131  label="H_element : 078"  # scripted group (container) (typed FeaturePython)
  n = 10
  ref = H_element
FEATURE [App::DocumentObjectGroupPython] C_element141  label="C_element : 086"  # scripted group (container) (typed FeaturePython)
  n = 9
  ref = C_element
FEATURE [App::DocumentObjectGroupPython] N_element061  label="N_element : 033"  # scripted group (container) (typed FeaturePython)
  n = 3
  ref = N_element
FEATURE [App::DocumentObjectGroupPython] O_element122  label="O_element : 075"  # scripted group (container) (typed FeaturePython)
  n = 5
  ref = O_element
FEATURE [App::DocumentObjectGroupPython] G4_DNA_CYTIDINE  # scripted group (container) (typed FeaturePython)
  Dunit = g/cm3
  Dvalue = 1
  Group = -> [H_element131,C_element141,N_element061,O_element122]
  conduct = 2
  density = 1
  expand = 3
  formula = G4_DNA_CYTIDINE
  name = G4_DNA_CYTIDINE
  specific = 4
FEATURE [App::DocumentObjectGroupPython] H_element132  label="H_element : 079"  # scripted group (container) (typed FeaturePython)
  n = 9
  ref = H_element
FEATURE [App::DocumentObjectGroupPython] C_element142  label="C_element : 087"  # scripted group (container) (typed FeaturePython)
  n = 9
  ref = C_element
FEATURE [App::DocumentObjectGroupPython] N_element062  label="N_element : 034"  # scripted group (container) (typed FeaturePython)
  n = 2
  ref = N_element
FEATURE [App::DocumentObjectGroupPython] O_element123  label="O_element : 076"  # scripted group (container) (typed FeaturePython)
  n = 6
  ref = O_element
FEATURE [App::DocumentObjectGroupPython] G4_DNA_URIDINE  # scripted group (container) (typed FeaturePython)
  Dunit = g/cm3
  Dvalue = 1
  Group = -> [H_element132,C_element142,N_element062,O_element123]
  conduct = 2
  density = 1
  expand = 3
  formula = G4_DNA_URIDINE
  name = G4_DNA_URIDINE
  specific = 4
FEATURE [App::DocumentObjectGroupPython] H_element133  label="H_element : 080"  # scripted group (container) (typed FeaturePython)
  n = 11
  ref = H_element
FEATURE [App::DocumentObjectGroupPython] C_element143  label="C_element : 088"  # scripted group (container) (typed FeaturePython)
  n = 10
  ref = C_element
FEATURE [App::DocumentObjectGroupPython] N_element063  label="N_element : 035"  # scripted group (container) (typed FeaturePython)
  n = 2
  ref = N_element
FEATURE [App::DocumentObjectGroupPython] O_element124  label="O_element : 077"  # scripted group (container) (typed FeaturePython)
  n = 6
  ref = O_element
FEATURE [App::DocumentObjectGroupPython] G4_DNA_METHYLURIDINE  # scripted group (container) (typed FeaturePython)
  Dunit = g/cm3
  Dvalue = 1
  Group = -> [H_element133,C_element143,N_element063,O_element124]
  conduct = 2
  density = 1
  expand = 3
  formula = G4_DNA_METHYLURIDINE
  name = G4_DNA_METHYLURIDINE
  specific = 4
FEATURE [App::DocumentObjectGroupPython] P_element014  label="P_element : 003"  # scripted group (container) (typed FeaturePython)
  n = 1
  ref = P_element
FEATURE [App::DocumentObjectGroupPython] O_element125  label="O_element : 078"  # scripted group (container) (typed FeaturePython)
  n = 3
  ref = O_element
FEATURE [App::DocumentObjectGroupPython] G4_DNA_MONOPHOSPHATE  # scripted group (container) (typed FeaturePython)
  Dunit = g/cm3
  Dvalue = 1
  Group = -> [P_element014,O_element125]
  conduct = 2
  density = 1
  expand = 3
  formula = G4_DNA_MONOPHOSPHATE
  name = G4_DNA_MONOPHOSPHATE
  specific = 4
FEATURE [App::DocumentObjectGroupPython] H_element134  label="H_element : 081"  # scripted group (container) (typed FeaturePython)
  n = 10
  ref = H_element
FEATURE [App::DocumentObjectGroupPython] C_element144  label="C_element : 089"  # scripted group (container) (typed FeaturePython)
  n = 10
  ref = C_element
FEATURE [App::DocumentObjectGroupPython] N_element064  label="N_element : 036"  # scripted group (container) (typed FeaturePython)
  n = 5
  ref = N_element
FEATURE [App::DocumentObjectGroupPython] O_element126  label="O_element : 079"  # scripted group (container) (typed FeaturePython)
  n = 7
  ref = O_element
FEATURE [App::DocumentObjectGroupPython] P_element015  label="P_element : 004"  # scripted group (container) (typed FeaturePython)
  n = 1
  ref = P_element
FEATURE [App::DocumentObjectGroupPython] G4_DNA_A  # scripted group (container) (typed FeaturePython)
  Dunit = g/cm3
  Dvalue = 1
  Group = -> [H_element134,C_element144,N_element064,O_element126,P_element015]
  conduct = 2
  density = 1
  expand = 3
  formula = G4_DNA_A
  name = G4_DNA_A
  specific = 4
FEATURE [App::DocumentObjectGroupPython] H_element135  label="H_element : 082"  # scripted group (container) (typed FeaturePython)
  n = 10
  ref = H_element
FEATURE [App::DocumentObjectGroupPython] C_element145  label="C_element : 090"  # scripted group (container) (typed FeaturePython)
  n = 10
  ref = C_element
FEATURE [App::DocumentObjectGroupPython] N_element065  label="N_element : 037"  # scripted group (container) (typed FeaturePython)
  n = 5
  ref = N_element
FEATURE [App::DocumentObjectGroupPython] O_element127  label="O_element : 8"  # scripted group (container) (typed FeaturePython)
  n = 8
  ref = O_element
FEATURE [App::DocumentObjectGroupPython] P_element016  label="P_element : 005"  # scripted group (container) (typed FeaturePython)
  n = 1
  ref = P_element
FEATURE [App::DocumentObjectGroupPython] G4_DNA_G  # scripted group (container) (typed FeaturePython)
  Dunit = g/cm3
  Dvalue = 1
  Group = -> [H_element135,C_element145,N_element065,O_element127,P_element016]
  conduct = 2
  density = 1
  expand = 3
  formula = G4_DNA_G
  name = G4_DNA_G
  specific = 4
FEATURE [App::DocumentObjectGroupPython] H_element136  label="H_element : 083"  # scripted group (container) (typed FeaturePython)
  n = 10
  ref = H_element
FEATURE [App::DocumentObjectGroupPython] C_element146  label="C_element : 091"  # scripted group (container) (typed FeaturePython)
  n = 9
  ref = C_element
FEATURE [App::DocumentObjectGroupPython] N_element066  label="N_element : 038"  # scripted group (container) (typed FeaturePython)
  n = 3
  ref = N_element
FEATURE [App::DocumentObjectGroupPython] O_element128  label="O_element : 080"  # scripted group (container) (typed FeaturePython)
  n = 8
  ref = O_element
FEATURE [App::DocumentObjectGroupPython] P_element017  label="P_element : 006"  # scripted group (container) (typed FeaturePython)
  n = 1
  ref = P_element
FEATURE [App::DocumentObjectGroupPython] G4_DNA_C  # scripted group (container) (typed FeaturePython)
  Dunit = g/cm3
  Dvalue = 1
  Group = -> [H_element136,C_element146,N_element066,O_element128,P_element017]
  conduct = 2
  density = 1
  expand = 3
  formula = G4_DNA_C
  name = G4_DNA_C
  specific = 4
FEATURE [App::DocumentObjectGroupPython] H_element137  label="H_element : 084"  # scripted group (container) (typed FeaturePython)
  n = 9
  ref = H_element
FEATURE [App::DocumentObjectGroupPython] C_element147  label="C_element : 092"  # scripted group (container) (typed FeaturePython)
  n = 9
  ref = C_element
FEATURE [App::DocumentObjectGroupPython] N_element067  label="N_element : 039"  # scripted group (container) (typed FeaturePython)
  n = 2
  ref = N_element
FEATURE [App::DocumentObjectGroupPython] O_element129  label="O_element : 9"  # scripted group (container) (typed FeaturePython)
  n = 9
  ref = O_element
FEATURE [App::DocumentObjectGroupPython] P_element018  label="P_element : 007"  # scripted group (container) (typed FeaturePython)
  n = 1
  ref = P_element
FEATURE [App::DocumentObjectGroupPython] G4_DNA_U  # scripted group (container) (typed FeaturePython)
  Dunit = g/cm3
  Dvalue = 1
  Group = -> [H_element137,C_element147,N_element067,O_element129,P_element018]
  conduct = 2
  density = 1
  expand = 3
  formula = G4_DNA_U
  name = G4_DNA_U
  specific = 4
FEATURE [App::DocumentObjectGroupPython] H_element138  label="H_element : 085"  # scripted group (container) (typed FeaturePython)
  n = 11
  ref = H_element
FEATURE [App::DocumentObjectGroupPython] C_element148  label="C_element : 093"  # scripted group (container) (typed FeaturePython)
  n = 10
  ref = C_element
FEATURE [App::DocumentObjectGroupPython] N_element068  label="N_element : 040"  # scripted group (container) (typed FeaturePython)
  n = 2
  ref = N_element
FEATURE [App::DocumentObjectGroupPython] O_element130  label="O_element : 081"  # scripted group (container) (typed FeaturePython)
  n = 9
  ref = O_element
FEATURE [App::DocumentObjectGroupPython] P_element019  label="P_element : 008"  # scripted group (container) (typed FeaturePython)
  n = 1
  ref = P_element
FEATURE [App::DocumentObjectGroupPython] G4_DNA_MU  # scripted group (container) (typed FeaturePython)
  Dunit = g/cm3
  Dvalue = 1
  Group = -> [H_element138,C_element148,N_element068,O_element130,P_element019]
  conduct = 2
  density = 1
  expand = 3
  formula = G4_DNA_MU
  name = G4_DNA_MU
  specific = 4
FEATURE [App::DocumentObjectGroupPython] BioChemical  # scripted group (container) (typed FeaturePython)
  Group = -> [G4_CYTOSINE,G4_THYMINE,G4_URACIL,G4_DNA_ADENINE,G4_DNA_GUANINE,G4_DNA_CYTOSINE,G4_DNA_THYMINE,G4_DNA_URACIL,G4_DNA_ADENOSINE,G4_DNA_GUANOSINE,G4_DNA_CYTIDINE,G4_DNA_URIDINE,G4_DNA_METHYLURIDINE,G4_DNA_MONOPHOSPHATE,G4_DNA_A,G4_DNA_G,G4_DNA_C,G4_DNA_U,G4_DNA_MU]
FEATURE [App::DocumentObjectGroupPython] G4Materials  # scripted group (container) (typed FeaturePython)
  Group = -> [NIST,Element,HEP,Space,BioChemical]
  version = 1
FEATURE [App::DocumentObjectGroupPython] Geant4  # scripted group (container) (typed FeaturePython)
  Group = -> [G4Isotopes,G4Elements,G4Materials]
FEATURE [App::DocumentObjectGroupPython] Materials  # scripted group (container) (typed FeaturePython)
  Group = -> [Geant4]
FEATURE [Part::FeaturePython] GDMLBox_WorldBox  # WARN: FeaturePython — macro-defined, semantics opaque (R4)
  lunit = 3
  material = 288
  x = 500
  y = 500
  z = 1200
FEATURE [Sketcher::SketchObject] Sketch001
  FullyConstrained = false
  MapMode = 5
  Placement = pos=(0,0,0) rot=(0.57735,0.57735,0.57735;2.0944rad)
  Support = -> [YZ_Plane001]
  sketch-geometry (36):
    g0: LineSegment StartX=345.196 StartY=1207.39 StartZ=0 EndX=345.196 EndY=4779.1 EndZ=0
    g1: LineSegment StartX=910.487 StartY=4896.42 StartZ=0 EndX=910.487 EndY=5006.42 EndZ=0
    g2: LineSegment StartX=435.196 StartY=4869.1 StartZ=0 EndX=445.196 EndY=4869.1 EndZ=0
    g3: LineSegment StartX=445.196 StartY=4869.1 StartZ=0 EndX=445.196 EndY=4896.42 EndZ=0
    g4: LineSegment StartX=445.196 StartY=4896.42 StartZ=0 EndX=910.487 EndY=4896.42 EndZ=0
    g5: LineSegment StartX=318.538 StartY=5006.42 StartZ=0 EndX=910.487 EndY=5006.42 EndZ=0
    g6: LineSegment StartX=175.531 StartY=1234.96 StartZ=0 EndX=318.538 EndY=1234.96 EndZ=0
    g7: LineSegment StartX=318.538 StartY=5006.42 StartZ=0 EndX=318.538 EndY=1234.96 EndZ=0
    g8: LineSegment StartX=0 StartY=39.215 StartZ=0 EndX=0 EndY=0 EndZ=0
    g9-g16: Circle x8 (B-spline internal-alignment scaffolding for g17; pole/knot coordinates omitted)
    g17: BSplineCurve PolesCount=8 KnotsCount=6 Degree=3 IsPeriodic=0
    g18-g23: GeomPoint x6 (B-spline internal-alignment scaffolding for g17; pole/knot coordinates omitted)
    g24: LineSegment StartX=175.531 StartY=1234.96 StartZ=0 EndX=175.531 EndY=838.896 EndZ=0
    g25-g29: Circle x5 (B-spline internal-alignment scaffolding for g30; pole/knot coordinates omitted)
    g30: BSplineCurve PolesCount=5 KnotsCount=3 Degree=3 IsPeriodic=0
    g31: GeomPoint X=175.531 Y=838.896 Z=0
    g32: GeomPoint X=165.058 Y=242.363 Z=0
    g33: GeomPoint X=0 Y=39.215 Z=0
    g34: ArcOfCircle CenterX=435.196 CenterY=4779.1 CenterZ=0 NormalX=0 NormalY=0 NormalZ=1 AngleXU=0 Radius=90 StartAngle=1.5708 EndAngle=3.14159
    g35: GeomPoint X=345.196 Y=4869.1 Z=0
  constraints (38):
    c: Vertical(g1)
    c: Horizontal(g2)
    c: Coincident(g2,g3)
    c: Vertical(g3)
    c: Coincident(g3,g4)
    c: Coincident(g4,g1)
    c: Horizontal(g4)
    c: Coincident(g5,g1)
    c: Horizontal(g5)
    c: Horizontal(g6)
    c: Coincident(g7,g5)
    c: Coincident(g7,g6)
    c: Vertical(g7)
    c: DistanceX(g35,g2) = 100
    c: Vertical(g8)
    c: Vertical(g0)
    c: Coincident(g17,g0)
    c: Weight(g9) = 1
    c: Equal(g9, g10-g16) x7
    c: Coincident(g17,g8)
    c: InternalAlignment(g9-g16 -> g17) x8
    c: InternalAlignment(g18-g23 -> g17) x6
    c: Coincident(g24,g6)
    c: Vertical(g24)
    c: Coincident(g30,g24)
    c: Weight(g25) = 1
    c: Equal(g25, g26-g29) x4
    c: Coincident(g30,g8)
    c: InternalAlignment(g25-g29 -> g30) x5
    c: InternalAlignment(g31,g30)
    c: InternalAlignment(g32,g30)
    c: InternalAlignment(g33,g30)
    c: Coincident(g8,g-1)
    c: PointOnObject(g35,g2)
    c: PointOnObject(g35,g0)
    c: Tangent(g2,g34) = 1.5708
    c: Tangent(g0,g34) = 1.5708
    c: Radius(g34) = 90
FEATURE [Part::Revolution] Revolve
  Angle = 360
  Axis = (0,0,1)
  Base = (0,0,0)
  FaceMakerClass = Part::FaceMakerBullseye
  Solid = true
  Source = -> Sketch001
  Symmetric = false
  material = 176
FEATURE [Part::Cylinder] Cylinder
  Angle = 360
  AttacherType = Attacher::AttachEngine3D
  FirstAngle = 0
  Height = 200
  Placement = pos=(474,0,4850) rot=(0,0,1;0rad)
  Radius = 60
  SecondAngle = 0
FEATURE [Part::Cut] Cut
  Base = -> Revolve
  Tool = -> Cylinder
FEATURE [App::Part] Bool_Cut
  Group = -> [Sketch001,Revolve,Cylinder,Cut]
  Origin = -> Origin004
FEATURE [App::Part] worldVOL
  Group = -> [GDMLBox_WorldBox,Bool_Cut]
  Origin = -> Origin
